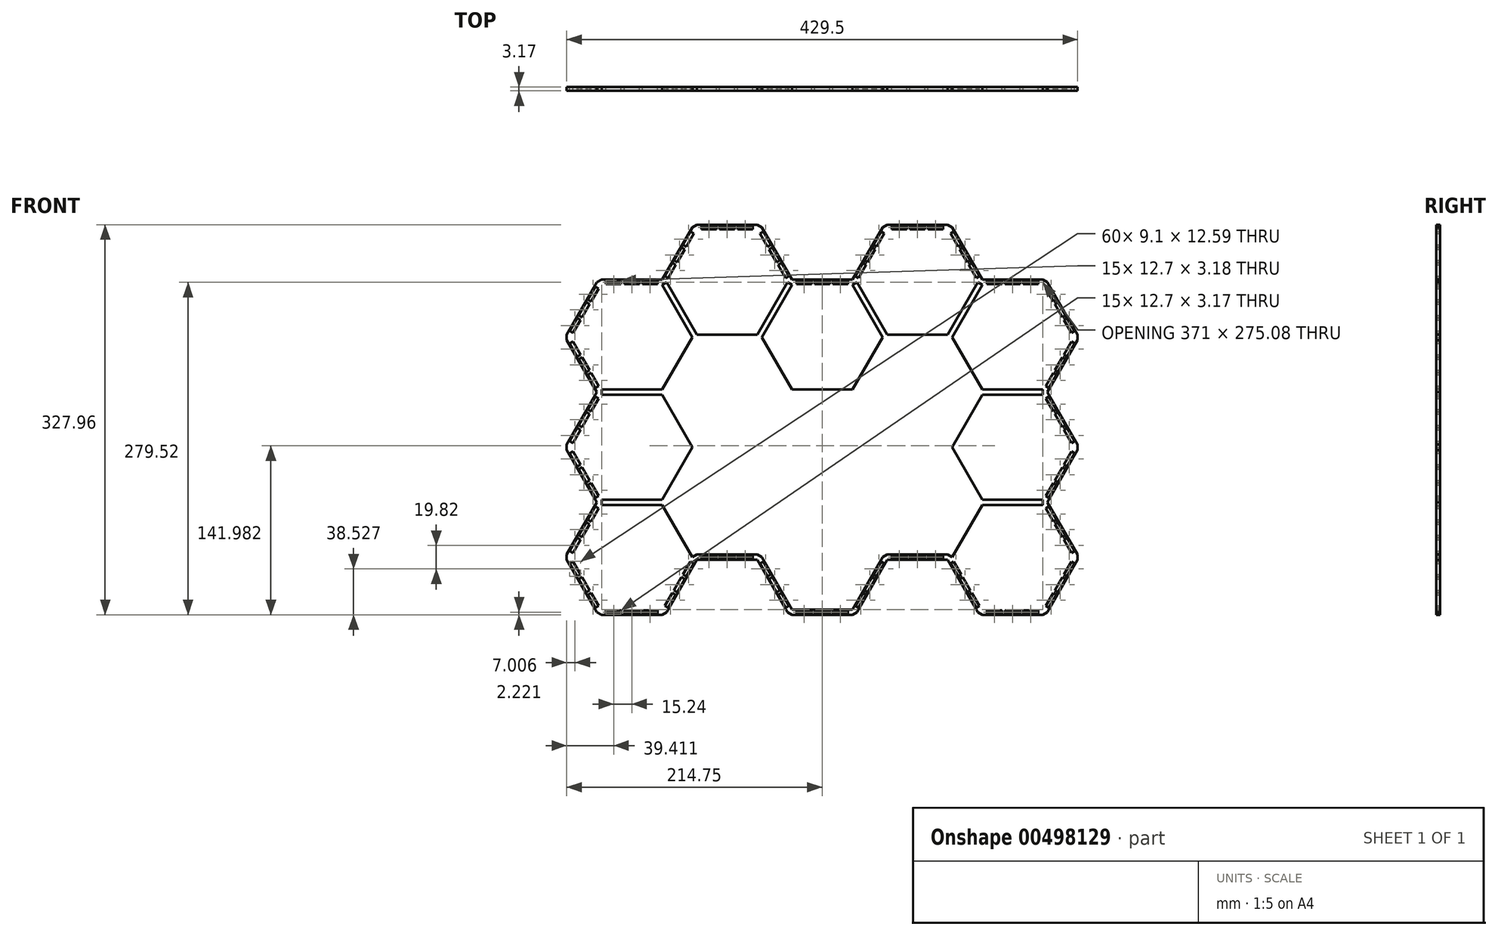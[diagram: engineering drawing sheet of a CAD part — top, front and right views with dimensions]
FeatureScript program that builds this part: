
annotation { "Feature Type Name" : "Feature", "Feature Type Description" : "" }
export const myFeature = defineFeature(function(context is Context, id is Id, definition is map)
    precondition{}
    {
        {
            var Q0;
            Q0=qCreatedBy(makeId("Front.planeOp"),FACE);
            var sketch = newSketch(context, id + "F0", { "sketchPlane" : qUnion([Q0])});
            skLineSegment(sketch, "E0", {"start": v(-1207.39, 88.12) * mm, "end": v(-1156.59, 88.12) * mm});
            skLineSegment(sketch, "E1", {"start": v(-1207.39, 92.57) * mm, "end": v(-1207.39, 88.12) * mm});
            skLineSegment(sketch, "E2", {"start": v(-1156.59, 92.57) * mm, "end": v(-1156.59, 88.12) * mm});
            skLineSegment(sketch, "E3", {"start": v(-1232.79, 44.13) * mm, "end": v(-1131.19, 44.13) * mm, "construction": true});
            skPoint(sketch, "E4.endSnap0", {"position": v(-1156.59, 90.34) * mm});
            skLineSegment(sketch, "E5", {"start": v(-1207.39, 90.34) * mm, "end": v(-1156.59, 90.34) * mm, "construction": true});
            skLineSegment(sketch, "E6", {"start": v(-1207.39, 92.57) * mm, "end": v(-1156.59, 92.57) * mm});
            skLineSegment(sketch, "E7", {"start": v(-1236.64, 46.35) * mm, "end": v(-1232.79, 44.13) * mm});
            skLineSegment(sketch, "E8.left", {"start": v(-1160.4, 88.76) * mm, "end": v(-1160.4, 91.93) * mm});
            skLineSegment(sketch, "E8.right", {"start": v(-1203.58, 88.76) * mm, "end": v(-1203.58, 91.93) * mm});
            skPoint(sketch, "E8.middle", {"position": v(-1181.99, 90.34) * mm});
            skLineSegment(sketch, "E9", {"start": v(-1181.99, 91.93) * mm, "end": v(-1181.99, 88.76) * mm, "construction": true});
            skLineSegment(sketch, "E10", {"start": v(-1190.88, 91.93) * mm, "end": v(-1190.88, 88.76) * mm});
            skLineSegment(sketch, "E11.MirrorCS", {"start": v(-1173.1, 91.93) * mm, "end": v(-1173.1, 88.76) * mm});
            skLineSegment(sketch, "E12", {"start": v(-1188.34, 91.93) * mm, "end": v(-1188.34, 88.76) * mm});
            skLineSegment(sketch, "E13.MirrorCS", {"start": v(-1175.64, 91.93) * mm, "end": v(-1175.64, 88.76) * mm});
            skLineSegment(sketch, "E14", {"start": v(-1203.58, 91.93) * mm, "end": v(-1190.88, 91.93) * mm});
            skLineSegment(sketch, "E15", {"start": v(-1203.58, 88.76) * mm, "end": v(-1190.88, 88.76) * mm});
            skLineSegment(sketch, "E16", {"start": v(-1188.34, 88.76) * mm, "end": v(-1181.99, 88.76) * mm});
            skLineSegment(sketch, "E17", {"start": v(-1188.34, 91.93) * mm, "end": v(-1181.99, 91.93) * mm});
            skLineSegment(sketch, "E18", {"start": v(-1181.99, 91.93) * mm, "end": v(-1175.64, 91.93) * mm});
            skLineSegment(sketch, "E19", {"start": v(-1181.99, 88.76) * mm, "end": v(-1175.64, 88.76) * mm});
            skLineSegment(sketch, "E20", {"start": v(-1173.1, 91.93) * mm, "end": v(-1160.4, 91.93) * mm});
            skLineSegment(sketch, "E21", {"start": v(-1173.1, 88.76) * mm, "end": v(-1160.4, 88.76) * mm});
            skLineSegment(sketch, "E22", {"start": v(-1156.59, 88.12) * mm, "end": v(-1131.19, 44.13) * mm});
            skLineSegment(sketch, "E23", {"start": v(-1152.74, 90.34) * mm, "end": v(-1156.59, 88.12) * mm});
            skPoint(sketch, "E24.endSnap0", {"position": v(-1129.26, 45.24) * mm});
            skLineSegment(sketch, "E25", {"start": v(-1152.74, 90.34) * mm, "end": v(-1127.34, 46.35) * mm});
            skLineSegment(sketch, "E26.left", {"start": v(-1132.54, 47.74) * mm, "end": v(-1129.8, 49.33) * mm});
            skLineSegment(sketch, "E26.right", {"start": v(-1154.13, 85.14) * mm, "end": v(-1151.38, 86.73) * mm});
            skPoint(sketch, "E26.middle", {"position": v(-1141.96, 67.24) * mm});
            skLineSegment(sketch, "E27", {"start": v(-1140.59, 68.03) * mm, "end": v(-1143.34, 66.44) * mm, "construction": true});
            skLineSegment(sketch, "E28", {"start": v(-1145.03, 75.73) * mm, "end": v(-1147.78, 74.14) * mm});
            skLineSegment(sketch, "E29.MirrorCS", {"start": v(-1136.14, 60.33) * mm, "end": v(-1138.9, 58.74) * mm});
            skLineSegment(sketch, "E30", {"start": v(-1143.76, 73.53) * mm, "end": v(-1146.51, 71.94) * mm});
            skLineSegment(sketch, "E31.MirrorCS", {"start": v(-1137.41, 62.53) * mm, "end": v(-1140.16, 60.94) * mm});
            skLineSegment(sketch, "E32", {"start": v(-1151.38, 86.73) * mm, "end": v(-1145.03, 75.73) * mm});
            skLineSegment(sketch, "E33", {"start": v(-1154.13, 85.14) * mm, "end": v(-1147.78, 74.14) * mm});
            skLineSegment(sketch, "E34", {"start": v(-1146.51, 71.94) * mm, "end": v(-1143.34, 66.44) * mm});
            skLineSegment(sketch, "E35", {"start": v(-1143.76, 73.53) * mm, "end": v(-1140.59, 68.03) * mm});
            skLineSegment(sketch, "E36", {"start": v(-1140.59, 68.03) * mm, "end": v(-1137.41, 62.53) * mm});
            skLineSegment(sketch, "E37", {"start": v(-1143.34, 66.44) * mm, "end": v(-1140.16, 60.94) * mm});
            skLineSegment(sketch, "E38", {"start": v(-1136.14, 60.33) * mm, "end": v(-1129.8, 49.33) * mm});
            skLineSegment(sketch, "E39", {"start": v(-1138.9, 58.74) * mm, "end": v(-1132.54, 47.74) * mm});
            skLineSegment(sketch, "E40", {"start": v(-1232.79, 44.13) * mm, "end": v(-1207.39, 88.12) * mm});
            skLineSegment(sketch, "E41", {"start": v(-1211.24, 90.34) * mm, "end": v(-1207.39, 88.12) * mm});
            skPoint(sketch, "E42.endSnap0", {"position": v(-1209.31, 89.23) * mm});
            skLineSegment(sketch, "E43", {"start": v(-1236.64, 46.35) * mm, "end": v(-1211.24, 90.34) * mm});
            skLineSegment(sketch, "E44.left", {"start": v(-1209.84, 85.14) * mm, "end": v(-1212.6, 86.73) * mm});
            skLineSegment(sketch, "E44.right", {"start": v(-1231.43, 47.74) * mm, "end": v(-1234.18, 49.33) * mm});
            skPoint(sketch, "E44.middle", {"position": v(-1222.01, 67.24) * mm});
            skLineSegment(sketch, "E45", {"start": v(-1223.39, 68.03) * mm, "end": v(-1220.64, 66.44) * mm, "construction": true});
            skLineSegment(sketch, "E46", {"start": v(-1227.83, 60.33) * mm, "end": v(-1225.08, 58.74) * mm});
            skLineSegment(sketch, "E47.MirrorCS", {"start": v(-1218.94, 75.73) * mm, "end": v(-1216.2, 74.14) * mm});
            skLineSegment(sketch, "E48", {"start": v(-1226.56, 62.53) * mm, "end": v(-1223.81, 60.94) * mm});
            skLineSegment(sketch, "E49.MirrorCS", {"start": v(-1220.21, 73.53) * mm, "end": v(-1217.46, 71.94) * mm});
            skLineSegment(sketch, "E50", {"start": v(-1234.18, 49.33) * mm, "end": v(-1227.83, 60.33) * mm});
            skLineSegment(sketch, "E51", {"start": v(-1231.43, 47.74) * mm, "end": v(-1225.08, 58.74) * mm});
            skLineSegment(sketch, "E52", {"start": v(-1223.81, 60.94) * mm, "end": v(-1220.64, 66.44) * mm});
            skLineSegment(sketch, "E53", {"start": v(-1226.56, 62.53) * mm, "end": v(-1223.39, 68.03) * mm});
            skLineSegment(sketch, "E54", {"start": v(-1223.39, 68.03) * mm, "end": v(-1220.21, 73.53) * mm});
            skLineSegment(sketch, "E55", {"start": v(-1220.64, 66.44) * mm, "end": v(-1217.46, 71.94) * mm});
            skLineSegment(sketch, "E56", {"start": v(-1218.94, 75.73) * mm, "end": v(-1212.6, 86.73) * mm});
            skLineSegment(sketch, "E57", {"start": v(-1216.2, 74.14) * mm, "end": v(-1209.84, 85.14) * mm});
            skLineSegment(sketch, "E58.0", {"start": v(-1207.39, 88.12) * mm, "end": v(-1211.24, 90.34) * mm, "construction": true});
            skLineSegment(sketch, "E59", {"start": v(-1131.19, 44.13) * mm, "end": v(-1127.34, 46.35) * mm});
            skLineSegment(sketch, "E60.MirrorCS", {"start": v(-1211.24, -2.09) * mm, "end": v(-1207.39, 0.13) * mm});
            skLineSegment(sketch, "E61.MirrorCS", {"start": v(-1140.59, 20.23) * mm, "end": v(-1143.34, 21.81) * mm, "construction": true});
            skLineSegment(sketch, "E62.MirrorCS", {"start": v(-1223.39, 20.23) * mm, "end": v(-1220.64, 21.81) * mm, "construction": true});
            skLineSegment(sketch, "E63.MirrorCS", {"start": v(-1181.99, -3.68) * mm, "end": v(-1181.99, -0.5) * mm, "construction": true});
            skLineSegment(sketch, "E64.MirrorCS", {"start": v(-1207.39, 0.13) * mm, "end": v(-1211.24, -2.09) * mm, "construction": true});
            skLineSegment(sketch, "E65.MirrorCS", {"start": v(-1152.74, -2.09) * mm, "end": v(-1156.59, 0.13) * mm});
            skLineSegment(sketch, "E66.MirrorCS", {"start": v(-1154.13, 3.12) * mm, "end": v(-1151.38, 1.53) * mm});
            skLineSegment(sketch, "E67.MirrorCS", {"start": v(-1220.21, 14.73) * mm, "end": v(-1217.46, 16.31) * mm});
            skLineSegment(sketch, "E68.MirrorCS", {"start": v(-1175.64, -3.68) * mm, "end": v(-1175.64, -0.5) * mm});
            skLineSegment(sketch, "E69.MirrorCS", {"start": v(-1156.59, -4.31) * mm, "end": v(-1156.59, 0.13) * mm});
            skLineSegment(sketch, "E70.MirrorCS", {"start": v(-1190.88, -3.68) * mm, "end": v(-1190.88, -0.5) * mm});
            skLineSegment(sketch, "E71.MirrorCS", {"start": v(-1145.03, 12.53) * mm, "end": v(-1147.78, 14.11) * mm});
            skLineSegment(sketch, "E72.MirrorCS", {"start": v(-1188.34, -3.68) * mm, "end": v(-1188.34, -0.5) * mm});
            skLineSegment(sketch, "E73.MirrorCS", {"start": v(-1209.84, 3.12) * mm, "end": v(-1212.6, 1.53) * mm});
            skLineSegment(sketch, "E74.MirrorCS", {"start": v(-1231.43, 40.51) * mm, "end": v(-1234.18, 38.92) * mm});
            skLineSegment(sketch, "E75.MirrorCS", {"start": v(-1226.56, 25.72) * mm, "end": v(-1223.81, 27.31) * mm});
            skLineSegment(sketch, "E76.MirrorCS", {"start": v(-1236.64, 41.9) * mm, "end": v(-1232.79, 44.13) * mm});
            skLineSegment(sketch, "E77.MirrorCS", {"start": v(-1143.76, 14.73) * mm, "end": v(-1146.51, 16.31) * mm});
            skLineSegment(sketch, "E78.MirrorCS", {"start": v(-1173.1, -3.68) * mm, "end": v(-1173.1, -0.5) * mm});
            skLineSegment(sketch, "E79.MirrorCS", {"start": v(-1227.83, 27.92) * mm, "end": v(-1225.08, 29.51) * mm});
            skLineSegment(sketch, "E80.MirrorCS", {"start": v(-1132.54, 40.51) * mm, "end": v(-1129.8, 38.92) * mm});
            skLineSegment(sketch, "E81.MirrorCS", {"start": v(-1203.58, -0.5) * mm, "end": v(-1203.58, -3.68) * mm});
            skLineSegment(sketch, "E82.MirrorCS", {"start": v(-1136.14, 27.92) * mm, "end": v(-1138.9, 29.51) * mm});
            skLineSegment(sketch, "E83.MirrorCS", {"start": v(-1131.19, 44.13) * mm, "end": v(-1127.34, 41.9) * mm});
            skLineSegment(sketch, "E84.MirrorCS", {"start": v(-1137.41, 25.72) * mm, "end": v(-1140.16, 27.31) * mm});
            skLineSegment(sketch, "E85.MirrorCS", {"start": v(-1218.94, 12.53) * mm, "end": v(-1216.2, 14.11) * mm});
            skLineSegment(sketch, "E86.MirrorCS", {"start": v(-1160.4, -0.5) * mm, "end": v(-1160.4, -3.68) * mm});
            skLineSegment(sketch, "E87.MirrorCS", {"start": v(-1146.51, 16.31) * mm, "end": v(-1143.34, 21.81) * mm});
            skLineSegment(sketch, "E88.MirrorCS", {"start": v(-1188.34, -0.5) * mm, "end": v(-1181.99, -0.5) * mm});
            skLineSegment(sketch, "E89.MirrorCS", {"start": v(-1223.81, 27.31) * mm, "end": v(-1220.64, 21.81) * mm});
            skLineSegment(sketch, "E90.MirrorCS", {"start": v(-1140.59, 20.23) * mm, "end": v(-1137.41, 25.72) * mm});
            skLineSegment(sketch, "E91.MirrorCS", {"start": v(-1207.39, -4.31) * mm, "end": v(-1207.39, 0.13) * mm});
            skLineSegment(sketch, "E92.MirrorCS", {"start": v(-1181.99, -3.68) * mm, "end": v(-1175.64, -3.68) * mm});
            skLineSegment(sketch, "E93.MirrorCS", {"start": v(-1143.34, 21.81) * mm, "end": v(-1140.16, 27.31) * mm});
            skPoint(sketch, "E94.MirrorP", {"position": v(-1181.99, -2.09) * mm});
            skLineSegment(sketch, "E95.MirrorCS", {"start": v(-1181.99, -0.5) * mm, "end": v(-1175.64, -0.5) * mm});
            skLineSegment(sketch, "E96.MirrorCS", {"start": v(-1143.76, 14.73) * mm, "end": v(-1140.59, 20.23) * mm});
            skLineSegment(sketch, "E97.MirrorCS", {"start": v(-1220.64, 21.81) * mm, "end": v(-1217.46, 16.31) * mm});
            skLineSegment(sketch, "E98.MirrorCS", {"start": v(-1188.34, -3.68) * mm, "end": v(-1181.99, -3.68) * mm});
            skLineSegment(sketch, "E99.MirrorCS", {"start": v(-1138.9, 29.51) * mm, "end": v(-1132.54, 40.51) * mm});
            skLineSegment(sketch, "E100.MirrorCS", {"start": v(-1236.64, 41.9) * mm, "end": v(-1211.24, -2.09) * mm});
            skLineSegment(sketch, "E101.MirrorCS", {"start": v(-1173.1, -3.68) * mm, "end": v(-1160.4, -3.68) * mm});
            skLineSegment(sketch, "E102.MirrorCS", {"start": v(-1156.59, 0.13) * mm, "end": v(-1131.19, 44.13) * mm});
            skLineSegment(sketch, "E103.MirrorCS", {"start": v(-1151.38, 1.53) * mm, "end": v(-1145.03, 12.53) * mm});
            skLineSegment(sketch, "E104.MirrorCS", {"start": v(-1231.43, 40.51) * mm, "end": v(-1225.08, 29.51) * mm});
            skLineSegment(sketch, "E105.MirrorCS", {"start": v(-1216.2, 14.11) * mm, "end": v(-1209.84, 3.12) * mm});
            skLineSegment(sketch, "E106.MirrorCS", {"start": v(-1173.1, -0.5) * mm, "end": v(-1160.4, -0.5) * mm});
            skPoint(sketch, "E107.MirrorP", {"position": v(-1141.96, 21.02) * mm});
            skLineSegment(sketch, "E108.MirrorCS", {"start": v(-1136.14, 27.92) * mm, "end": v(-1129.8, 38.92) * mm});
            skLineSegment(sketch, "E109.MirrorCS", {"start": v(-1207.39, 0.13) * mm, "end": v(-1156.59, 0.13) * mm});
            skPoint(sketch, "E110.MirrorP", {"position": v(-1156.59, -2.09) * mm});
            skPoint(sketch, "E111.MirrorP", {"position": v(-1209.31, -0.98) * mm});
            skLineSegment(sketch, "E112.MirrorCS", {"start": v(-1226.56, 25.72) * mm, "end": v(-1223.39, 20.23) * mm});
            skLineSegment(sketch, "E113.MirrorCS", {"start": v(-1207.39, -4.31) * mm, "end": v(-1156.59, -4.31) * mm});
            skLineSegment(sketch, "E114.MirrorCS", {"start": v(-1203.58, -0.5) * mm, "end": v(-1190.88, -0.5) * mm});
            skPoint(sketch, "E115.MirrorP", {"position": v(-1222.01, 21.02) * mm});
            skLineSegment(sketch, "E116.MirrorCS", {"start": v(-1207.39, -2.09) * mm, "end": v(-1156.59, -2.09) * mm, "construction": true});
            skLineSegment(sketch, "E117.MirrorCS", {"start": v(-1154.13, 3.12) * mm, "end": v(-1147.78, 14.11) * mm});
            skLineSegment(sketch, "E118.MirrorCS", {"start": v(-1152.74, -2.09) * mm, "end": v(-1127.34, 41.9) * mm});
            skLineSegment(sketch, "E119.MirrorCS", {"start": v(-1203.58, -3.68) * mm, "end": v(-1190.88, -3.68) * mm});
            skLineSegment(sketch, "E120.MirrorCS", {"start": v(-1232.79, 44.13) * mm, "end": v(-1207.39, 0.13) * mm});
            skLineSegment(sketch, "E121.MirrorCS", {"start": v(-1218.94, 12.53) * mm, "end": v(-1212.6, 1.53) * mm});
            skLineSegment(sketch, "E122.MirrorCS", {"start": v(-1234.18, 38.92) * mm, "end": v(-1227.83, 27.92) * mm});
            skLineSegment(sketch, "E123.MirrorCS", {"start": v(-1223.39, 20.23) * mm, "end": v(-1220.21, 14.73) * mm});
            skPoint(sketch, "E124.MirrorP", {"position": v(-1129.26, 43.02) * mm});
            skLineSegment(sketch, "E125", {"start": v(-1207.39, 180.55) * mm, "end": v(-1156.59, 180.55) * mm});
            skLineSegment(sketch, "E126", {"start": v(-1207.39, 185) * mm, "end": v(-1207.39, 180.55) * mm});
            skLineSegment(sketch, "E127", {"start": v(-1156.59, 185) * mm, "end": v(-1156.59, 180.55) * mm});
            skLineSegment(sketch, "E128", {"start": v(-1232.79, 136.56) * mm, "end": v(-1131.19, 136.56) * mm, "construction": true});
            skPoint(sketch, "E129.endSnap0", {"position": v(-1156.59, 182.78) * mm});
            skLineSegment(sketch, "E130", {"start": v(-1207.39, 182.78) * mm, "end": v(-1156.59, 182.78) * mm, "construction": true});
            skLineSegment(sketch, "E131", {"start": v(-1207.39, 185) * mm, "end": v(-1156.59, 185) * mm});
            skLineSegment(sketch, "E132", {"start": v(-1236.64, 138.78) * mm, "end": v(-1232.79, 136.56) * mm});
            skLineSegment(sketch, "E133.left", {"start": v(-1160.4, 181.19) * mm, "end": v(-1160.4, 184.36) * mm});
            skLineSegment(sketch, "E133.right", {"start": v(-1203.58, 181.19) * mm, "end": v(-1203.58, 184.36) * mm});
            skPoint(sketch, "E133.middle", {"position": v(-1181.99, 182.78) * mm});
            skLineSegment(sketch, "E134", {"start": v(-1181.99, 184.36) * mm, "end": v(-1181.99, 181.19) * mm, "construction": true});
            skLineSegment(sketch, "E135", {"start": v(-1190.88, 184.36) * mm, "end": v(-1190.88, 181.19) * mm});
            skLineSegment(sketch, "E136.MirrorCS", {"start": v(-1173.1, 184.36) * mm, "end": v(-1173.1, 181.19) * mm});
            skLineSegment(sketch, "E137", {"start": v(-1188.34, 184.36) * mm, "end": v(-1188.34, 181.19) * mm});
            skLineSegment(sketch, "E138.MirrorCS", {"start": v(-1175.64, 184.36) * mm, "end": v(-1175.64, 181.19) * mm});
            skLineSegment(sketch, "E139", {"start": v(-1203.58, 184.36) * mm, "end": v(-1190.88, 184.36) * mm});
            skLineSegment(sketch, "E140", {"start": v(-1203.58, 181.19) * mm, "end": v(-1190.88, 181.19) * mm});
            skLineSegment(sketch, "E141", {"start": v(-1188.34, 181.19) * mm, "end": v(-1181.99, 181.19) * mm});
            skLineSegment(sketch, "E142", {"start": v(-1188.34, 184.36) * mm, "end": v(-1181.99, 184.36) * mm});
            skLineSegment(sketch, "E143", {"start": v(-1181.99, 184.36) * mm, "end": v(-1175.64, 184.36) * mm});
            skLineSegment(sketch, "E144", {"start": v(-1181.99, 181.19) * mm, "end": v(-1175.64, 181.19) * mm});
            skLineSegment(sketch, "E145", {"start": v(-1173.1, 184.36) * mm, "end": v(-1160.4, 184.36) * mm});
            skLineSegment(sketch, "E146", {"start": v(-1173.1, 181.19) * mm, "end": v(-1160.4, 181.19) * mm});
            skLineSegment(sketch, "E147", {"start": v(-1156.59, 180.55) * mm, "end": v(-1131.19, 136.56) * mm});
            skLineSegment(sketch, "E148", {"start": v(-1152.74, 182.78) * mm, "end": v(-1156.59, 180.55) * mm});
            skPoint(sketch, "E149.endSnap0", {"position": v(-1129.26, 137.67) * mm});
            skLineSegment(sketch, "E150", {"start": v(-1152.74, 182.78) * mm, "end": v(-1127.34, 138.78) * mm});
            skLineSegment(sketch, "E151.left", {"start": v(-1132.54, 140.18) * mm, "end": v(-1129.8, 141.76) * mm});
            skLineSegment(sketch, "E151.right", {"start": v(-1154.13, 177.57) * mm, "end": v(-1151.38, 179.16) * mm});
            skPoint(sketch, "E151.middle", {"position": v(-1141.96, 159.67) * mm});
            skLineSegment(sketch, "E152", {"start": v(-1140.59, 160.46) * mm, "end": v(-1143.34, 158.87) * mm, "construction": true});
            skLineSegment(sketch, "E153", {"start": v(-1145.03, 168.16) * mm, "end": v(-1147.78, 166.57) * mm});
            skLineSegment(sketch, "E154.MirrorCS", {"start": v(-1136.14, 152.76) * mm, "end": v(-1138.9, 151.18) * mm});
            skLineSegment(sketch, "E155", {"start": v(-1143.76, 165.96) * mm, "end": v(-1146.51, 164.37) * mm});
            skLineSegment(sketch, "E156.MirrorCS", {"start": v(-1137.41, 154.96) * mm, "end": v(-1140.16, 153.38) * mm});
            skLineSegment(sketch, "E157", {"start": v(-1151.38, 179.16) * mm, "end": v(-1145.03, 168.16) * mm});
            skLineSegment(sketch, "E158", {"start": v(-1154.13, 177.57) * mm, "end": v(-1147.78, 166.57) * mm});
            skLineSegment(sketch, "E159", {"start": v(-1146.51, 164.37) * mm, "end": v(-1143.34, 158.87) * mm});
            skLineSegment(sketch, "E160", {"start": v(-1143.76, 165.96) * mm, "end": v(-1140.59, 160.46) * mm});
            skLineSegment(sketch, "E161", {"start": v(-1140.59, 160.46) * mm, "end": v(-1137.41, 154.96) * mm});
            skLineSegment(sketch, "E162", {"start": v(-1143.34, 158.87) * mm, "end": v(-1140.16, 153.38) * mm});
            skLineSegment(sketch, "E163", {"start": v(-1136.14, 152.76) * mm, "end": v(-1129.8, 141.76) * mm});
            skLineSegment(sketch, "E164", {"start": v(-1138.9, 151.18) * mm, "end": v(-1132.54, 140.18) * mm});
            skLineSegment(sketch, "E165", {"start": v(-1232.79, 136.56) * mm, "end": v(-1207.39, 180.55) * mm});
            skLineSegment(sketch, "E166", {"start": v(-1211.24, 182.78) * mm, "end": v(-1207.39, 180.55) * mm});
            skPoint(sketch, "E167.endSnap0", {"position": v(-1209.31, 181.67) * mm});
            skLineSegment(sketch, "E168", {"start": v(-1236.64, 138.78) * mm, "end": v(-1211.24, 182.78) * mm});
            skLineSegment(sketch, "E169.left", {"start": v(-1209.84, 177.57) * mm, "end": v(-1212.6, 179.16) * mm});
            skLineSegment(sketch, "E169.right", {"start": v(-1231.43, 140.18) * mm, "end": v(-1234.18, 141.76) * mm});
            skPoint(sketch, "E169.middle", {"position": v(-1222.01, 159.67) * mm});
            skLineSegment(sketch, "E170", {"start": v(-1223.39, 160.46) * mm, "end": v(-1220.64, 158.87) * mm, "construction": true});
            skLineSegment(sketch, "E171", {"start": v(-1227.83, 152.76) * mm, "end": v(-1225.08, 151.18) * mm});
            skLineSegment(sketch, "E172.MirrorCS", {"start": v(-1218.94, 168.16) * mm, "end": v(-1216.2, 166.57) * mm});
            skLineSegment(sketch, "E173", {"start": v(-1226.56, 154.96) * mm, "end": v(-1223.81, 153.38) * mm});
            skLineSegment(sketch, "E174.MirrorCS", {"start": v(-1220.21, 165.96) * mm, "end": v(-1217.46, 164.37) * mm});
            skLineSegment(sketch, "E175", {"start": v(-1234.18, 141.76) * mm, "end": v(-1227.83, 152.76) * mm});
            skLineSegment(sketch, "E176", {"start": v(-1231.43, 140.18) * mm, "end": v(-1225.08, 151.18) * mm});
            skLineSegment(sketch, "E177", {"start": v(-1223.81, 153.38) * mm, "end": v(-1220.64, 158.87) * mm});
            skLineSegment(sketch, "E178", {"start": v(-1226.56, 154.96) * mm, "end": v(-1223.39, 160.46) * mm});
            skLineSegment(sketch, "E179", {"start": v(-1223.39, 160.46) * mm, "end": v(-1220.21, 165.96) * mm});
            skLineSegment(sketch, "E180", {"start": v(-1220.64, 158.87) * mm, "end": v(-1217.46, 164.37) * mm});
            skLineSegment(sketch, "E181", {"start": v(-1218.94, 168.16) * mm, "end": v(-1212.6, 179.16) * mm});
            skLineSegment(sketch, "E182", {"start": v(-1216.2, 166.57) * mm, "end": v(-1209.84, 177.57) * mm});
            skLineSegment(sketch, "E183.0", {"start": v(-1207.39, 180.55) * mm, "end": v(-1211.24, 182.78) * mm, "construction": true});
            skLineSegment(sketch, "E184", {"start": v(-1131.19, 136.56) * mm, "end": v(-1127.34, 138.78) * mm});
            skLineSegment(sketch, "E185.MirrorCS", {"start": v(-1211.24, 90.34) * mm, "end": v(-1207.39, 92.57) * mm});
            skLineSegment(sketch, "E186.MirrorCS", {"start": v(-1140.59, 112.66) * mm, "end": v(-1143.34, 114.25) * mm, "construction": true});
            skLineSegment(sketch, "E187.MirrorCS", {"start": v(-1223.39, 112.66) * mm, "end": v(-1220.64, 114.25) * mm, "construction": true});
            skLineSegment(sketch, "E188.MirrorCS", {"start": v(-1181.99, 88.76) * mm, "end": v(-1181.99, 91.93) * mm, "construction": true});
            skLineSegment(sketch, "E189.MirrorCS", {"start": v(-1207.39, 92.57) * mm, "end": v(-1211.24, 90.34) * mm, "construction": true});
            skLineSegment(sketch, "E190.MirrorCS", {"start": v(-1152.74, 90.34) * mm, "end": v(-1156.59, 92.57) * mm});
            skLineSegment(sketch, "E191.MirrorCS", {"start": v(-1154.13, 95.55) * mm, "end": v(-1151.38, 93.96) * mm});
            skLineSegment(sketch, "E192.MirrorCS", {"start": v(-1220.21, 107.16) * mm, "end": v(-1217.46, 108.75) * mm});
            skLineSegment(sketch, "E193.MirrorCS", {"start": v(-1175.64, 88.76) * mm, "end": v(-1175.64, 91.93) * mm});
            skLineSegment(sketch, "E194.MirrorCS", {"start": v(-1156.59, 88.12) * mm, "end": v(-1156.59, 92.57) * mm});
            skLineSegment(sketch, "E195.MirrorCS", {"start": v(-1190.88, 88.76) * mm, "end": v(-1190.88, 91.93) * mm});
            skLineSegment(sketch, "E196.MirrorCS", {"start": v(-1145.03, 104.96) * mm, "end": v(-1147.78, 106.55) * mm});
            skLineSegment(sketch, "E197.MirrorCS", {"start": v(-1188.34, 88.76) * mm, "end": v(-1188.34, 91.93) * mm});
            skLineSegment(sketch, "E198.MirrorCS", {"start": v(-1209.84, 95.55) * mm, "end": v(-1212.6, 93.96) * mm});
            skLineSegment(sketch, "E199.MirrorCS", {"start": v(-1231.43, 132.94) * mm, "end": v(-1234.18, 131.36) * mm});
            skLineSegment(sketch, "E200.MirrorCS", {"start": v(-1226.56, 118.16) * mm, "end": v(-1223.81, 119.75) * mm});
            skLineSegment(sketch, "E201.MirrorCS", {"start": v(-1236.64, 134.34) * mm, "end": v(-1232.79, 136.56) * mm});
            skLineSegment(sketch, "E202.MirrorCS", {"start": v(-1143.76, 107.16) * mm, "end": v(-1146.51, 108.75) * mm});
            skLineSegment(sketch, "E203.MirrorCS", {"start": v(-1173.1, 88.76) * mm, "end": v(-1173.1, 91.93) * mm});
            skLineSegment(sketch, "E204.MirrorCS", {"start": v(-1227.83, 120.36) * mm, "end": v(-1225.08, 121.94) * mm});
            skLineSegment(sketch, "E205.MirrorCS", {"start": v(-1132.54, 132.94) * mm, "end": v(-1129.8, 131.36) * mm});
            skLineSegment(sketch, "E206.MirrorCS", {"start": v(-1203.58, 91.93) * mm, "end": v(-1203.58, 88.76) * mm});
            skLineSegment(sketch, "E207.MirrorCS", {"start": v(-1136.14, 120.36) * mm, "end": v(-1138.9, 121.94) * mm});
            skLineSegment(sketch, "E208.MirrorCS", {"start": v(-1131.19, 136.56) * mm, "end": v(-1127.34, 134.34) * mm});
            skLineSegment(sketch, "E209.MirrorCS", {"start": v(-1137.41, 118.16) * mm, "end": v(-1140.16, 119.75) * mm});
            skLineSegment(sketch, "E210.MirrorCS", {"start": v(-1218.94, 104.96) * mm, "end": v(-1216.2, 106.55) * mm});
            skLineSegment(sketch, "E211.MirrorCS", {"start": v(-1160.4, 91.93) * mm, "end": v(-1160.4, 88.76) * mm});
            skLineSegment(sketch, "E212.MirrorCS", {"start": v(-1146.51, 108.75) * mm, "end": v(-1143.34, 114.25) * mm});
            skLineSegment(sketch, "E213.MirrorCS", {"start": v(-1223.81, 119.75) * mm, "end": v(-1220.64, 114.25) * mm});
            skLineSegment(sketch, "E214.MirrorCS", {"start": v(-1140.59, 112.66) * mm, "end": v(-1137.41, 118.16) * mm});
            skLineSegment(sketch, "E215.MirrorCS", {"start": v(-1207.39, 88.12) * mm, "end": v(-1207.39, 92.57) * mm});
            skLineSegment(sketch, "E216.MirrorCS", {"start": v(-1143.34, 114.25) * mm, "end": v(-1140.16, 119.75) * mm});
            skLineSegment(sketch, "E217.MirrorCS", {"start": v(-1143.76, 107.16) * mm, "end": v(-1140.59, 112.66) * mm});
            skLineSegment(sketch, "E218.MirrorCS", {"start": v(-1220.64, 114.25) * mm, "end": v(-1217.46, 108.75) * mm});
            skLineSegment(sketch, "E219.MirrorCS", {"start": v(-1138.9, 121.94) * mm, "end": v(-1132.54, 132.94) * mm});
            skLineSegment(sketch, "E220.MirrorCS", {"start": v(-1236.64, 134.34) * mm, "end": v(-1211.24, 90.34) * mm});
            skLineSegment(sketch, "E221.MirrorCS", {"start": v(-1156.59, 92.57) * mm, "end": v(-1131.19, 136.56) * mm});
            skLineSegment(sketch, "E222.MirrorCS", {"start": v(-1151.38, 93.96) * mm, "end": v(-1145.03, 104.96) * mm});
            skLineSegment(sketch, "E223.MirrorCS", {"start": v(-1231.43, 132.94) * mm, "end": v(-1225.08, 121.94) * mm});
            skLineSegment(sketch, "E224.MirrorCS", {"start": v(-1216.2, 106.55) * mm, "end": v(-1209.84, 95.55) * mm});
            skPoint(sketch, "E225.MirrorP", {"position": v(-1141.96, 113.45) * mm});
            skLineSegment(sketch, "E226.MirrorCS", {"start": v(-1136.14, 120.36) * mm, "end": v(-1129.8, 131.36) * mm});
            skPoint(sketch, "E227.MirrorP", {"position": v(-1209.31, 91.45) * mm});
            skLineSegment(sketch, "E228.MirrorCS", {"start": v(-1226.56, 118.16) * mm, "end": v(-1223.39, 112.66) * mm});
            skPoint(sketch, "E229.MirrorP", {"position": v(-1222.01, 113.45) * mm});
            skLineSegment(sketch, "E230.MirrorCS", {"start": v(-1154.13, 95.55) * mm, "end": v(-1147.78, 106.55) * mm});
            skLineSegment(sketch, "E231.MirrorCS", {"start": v(-1152.74, 90.34) * mm, "end": v(-1127.34, 134.34) * mm});
            skLineSegment(sketch, "E232.MirrorCS", {"start": v(-1232.79, 136.56) * mm, "end": v(-1207.39, 92.57) * mm});
            skLineSegment(sketch, "E233.MirrorCS", {"start": v(-1218.94, 104.96) * mm, "end": v(-1212.6, 93.96) * mm});
            skLineSegment(sketch, "E234.MirrorCS", {"start": v(-1234.18, 131.36) * mm, "end": v(-1227.83, 120.36) * mm});
            skLineSegment(sketch, "E235.MirrorCS", {"start": v(-1223.39, 112.66) * mm, "end": v(-1220.21, 107.16) * mm});
            skPoint(sketch, "E236.MirrorP", {"position": v(-1129.26, 135.45) * mm});
            skLineSegment(sketch, "E237", {"start": v(-1207.39, 272.99) * mm, "end": v(-1156.59, 272.99) * mm});
            skLineSegment(sketch, "E238", {"start": v(-1207.39, 277.43) * mm, "end": v(-1207.39, 272.99) * mm});
            skLineSegment(sketch, "E239", {"start": v(-1156.59, 277.43) * mm, "end": v(-1156.59, 272.99) * mm});
            skLineSegment(sketch, "E240", {"start": v(-1232.79, 229) * mm, "end": v(-1131.19, 229) * mm, "construction": true});
            skPoint(sketch, "E241.endSnap0", {"position": v(-1156.59, 275.21) * mm});
            skLineSegment(sketch, "E242", {"start": v(-1207.39, 275.21) * mm, "end": v(-1156.59, 275.21) * mm, "construction": true});
            skLineSegment(sketch, "E243", {"start": v(-1207.39, 277.43) * mm, "end": v(-1156.59, 277.43) * mm});
            skLineSegment(sketch, "E244", {"start": v(-1236.64, 231.22) * mm, "end": v(-1232.79, 229) * mm});
            skLineSegment(sketch, "E245.left", {"start": v(-1160.4, 273.62) * mm, "end": v(-1160.4, 276.8) * mm});
            skLineSegment(sketch, "E245.right", {"start": v(-1203.58, 273.62) * mm, "end": v(-1203.58, 276.8) * mm});
            skPoint(sketch, "E245.middle", {"position": v(-1181.99, 275.21) * mm});
            skLineSegment(sketch, "E246", {"start": v(-1181.99, 276.8) * mm, "end": v(-1181.99, 273.62) * mm, "construction": true});
            skLineSegment(sketch, "E247", {"start": v(-1190.88, 276.8) * mm, "end": v(-1190.88, 273.62) * mm});
            skLineSegment(sketch, "E248.MirrorCS", {"start": v(-1173.1, 276.8) * mm, "end": v(-1173.1, 273.62) * mm});
            skLineSegment(sketch, "E249", {"start": v(-1188.34, 276.8) * mm, "end": v(-1188.34, 273.62) * mm});
            skLineSegment(sketch, "E250.MirrorCS", {"start": v(-1175.64, 276.8) * mm, "end": v(-1175.64, 273.62) * mm});
            skLineSegment(sketch, "E251", {"start": v(-1203.58, 276.8) * mm, "end": v(-1190.88, 276.8) * mm});
            skLineSegment(sketch, "E252", {"start": v(-1203.58, 273.62) * mm, "end": v(-1190.88, 273.62) * mm});
            skLineSegment(sketch, "E253", {"start": v(-1188.34, 273.62) * mm, "end": v(-1181.99, 273.62) * mm});
            skLineSegment(sketch, "E254", {"start": v(-1188.34, 276.8) * mm, "end": v(-1181.99, 276.8) * mm});
            skLineSegment(sketch, "E255", {"start": v(-1181.99, 276.8) * mm, "end": v(-1175.64, 276.8) * mm});
            skLineSegment(sketch, "E256", {"start": v(-1181.99, 273.62) * mm, "end": v(-1175.64, 273.62) * mm});
            skLineSegment(sketch, "E257", {"start": v(-1173.1, 276.8) * mm, "end": v(-1160.4, 276.8) * mm});
            skLineSegment(sketch, "E258", {"start": v(-1173.1, 273.62) * mm, "end": v(-1160.4, 273.62) * mm});
            skLineSegment(sketch, "E259", {"start": v(-1156.59, 272.99) * mm, "end": v(-1131.19, 229) * mm});
            skLineSegment(sketch, "E260", {"start": v(-1152.74, 275.21) * mm, "end": v(-1156.59, 272.99) * mm});
            skPoint(sketch, "E261.endSnap0", {"position": v(-1129.26, 230.1) * mm});
            skLineSegment(sketch, "E262", {"start": v(-1152.74, 275.21) * mm, "end": v(-1127.34, 231.22) * mm});
            skLineSegment(sketch, "E263.left", {"start": v(-1132.54, 232.61) * mm, "end": v(-1129.8, 234.2) * mm});
            skLineSegment(sketch, "E263.right", {"start": v(-1154.13, 270) * mm, "end": v(-1151.38, 271.6) * mm});
            skPoint(sketch, "E263.middle", {"position": v(-1141.96, 252.1) * mm});
            skLineSegment(sketch, "E264", {"start": v(-1140.59, 252.9) * mm, "end": v(-1143.34, 251.3) * mm, "construction": true});
            skLineSegment(sketch, "E265", {"start": v(-1145.03, 260.6) * mm, "end": v(-1147.78, 259) * mm});
            skLineSegment(sketch, "E266.MirrorCS", {"start": v(-1136.14, 245.2) * mm, "end": v(-1138.9, 243.6) * mm});
            skLineSegment(sketch, "E267", {"start": v(-1143.76, 258.4) * mm, "end": v(-1146.51, 256.8) * mm});
            skLineSegment(sketch, "E268.MirrorCS", {"start": v(-1137.41, 247.4) * mm, "end": v(-1140.16, 245.8) * mm});
            skLineSegment(sketch, "E269", {"start": v(-1151.38, 271.6) * mm, "end": v(-1145.03, 260.6) * mm});
            skLineSegment(sketch, "E270", {"start": v(-1154.13, 270) * mm, "end": v(-1147.78, 259) * mm});
            skLineSegment(sketch, "E271", {"start": v(-1146.51, 256.8) * mm, "end": v(-1143.34, 251.3) * mm});
            skLineSegment(sketch, "E272", {"start": v(-1143.76, 258.4) * mm, "end": v(-1140.59, 252.9) * mm});
            skLineSegment(sketch, "E273", {"start": v(-1140.59, 252.9) * mm, "end": v(-1137.41, 247.4) * mm});
            skLineSegment(sketch, "E274", {"start": v(-1143.34, 251.3) * mm, "end": v(-1140.16, 245.8) * mm});
            skLineSegment(sketch, "E275", {"start": v(-1136.14, 245.2) * mm, "end": v(-1129.8, 234.2) * mm});
            skLineSegment(sketch, "E276", {"start": v(-1138.9, 243.6) * mm, "end": v(-1132.54, 232.61) * mm});
            skLineSegment(sketch, "E277", {"start": v(-1232.79, 229) * mm, "end": v(-1207.39, 272.99) * mm});
            skLineSegment(sketch, "E278", {"start": v(-1211.24, 275.21) * mm, "end": v(-1207.39, 272.99) * mm});
            skPoint(sketch, "E279.endSnap0", {"position": v(-1209.31, 274.1) * mm});
            skLineSegment(sketch, "E280", {"start": v(-1236.64, 231.22) * mm, "end": v(-1211.24, 275.21) * mm});
            skLineSegment(sketch, "E281.left", {"start": v(-1209.84, 270) * mm, "end": v(-1212.6, 271.6) * mm});
            skLineSegment(sketch, "E281.right", {"start": v(-1231.43, 232.61) * mm, "end": v(-1234.18, 234.2) * mm});
            skPoint(sketch, "E281.middle", {"position": v(-1222.01, 252.1) * mm});
            skLineSegment(sketch, "E282", {"start": v(-1223.39, 252.9) * mm, "end": v(-1220.64, 251.3) * mm, "construction": true});
            skLineSegment(sketch, "E283", {"start": v(-1227.83, 245.2) * mm, "end": v(-1225.08, 243.6) * mm});
            skLineSegment(sketch, "E284.MirrorCS", {"start": v(-1218.94, 260.6) * mm, "end": v(-1216.2, 259) * mm});
            skLineSegment(sketch, "E285", {"start": v(-1226.56, 247.4) * mm, "end": v(-1223.81, 245.8) * mm});
            skLineSegment(sketch, "E286.MirrorCS", {"start": v(-1220.21, 258.4) * mm, "end": v(-1217.46, 256.8) * mm});
            skLineSegment(sketch, "E287", {"start": v(-1234.18, 234.2) * mm, "end": v(-1227.83, 245.2) * mm});
            skLineSegment(sketch, "E288", {"start": v(-1231.43, 232.61) * mm, "end": v(-1225.08, 243.6) * mm});
            skLineSegment(sketch, "E289", {"start": v(-1223.81, 245.8) * mm, "end": v(-1220.64, 251.3) * mm});
            skLineSegment(sketch, "E290", {"start": v(-1226.56, 247.4) * mm, "end": v(-1223.39, 252.9) * mm});
            skLineSegment(sketch, "E291", {"start": v(-1223.39, 252.9) * mm, "end": v(-1220.21, 258.4) * mm});
            skLineSegment(sketch, "E292", {"start": v(-1220.64, 251.3) * mm, "end": v(-1217.46, 256.8) * mm});
            skLineSegment(sketch, "E293", {"start": v(-1218.94, 260.6) * mm, "end": v(-1212.6, 271.6) * mm});
            skLineSegment(sketch, "E294", {"start": v(-1216.2, 259) * mm, "end": v(-1209.84, 270) * mm});
            skLineSegment(sketch, "E295.0", {"start": v(-1207.39, 272.99) * mm, "end": v(-1211.24, 275.21) * mm, "construction": true});
            skLineSegment(sketch, "E296", {"start": v(-1131.19, 229) * mm, "end": v(-1127.34, 231.22) * mm});
            skLineSegment(sketch, "E297.MirrorCS", {"start": v(-1211.24, 182.78) * mm, "end": v(-1207.39, 185) * mm});
            skLineSegment(sketch, "E298.MirrorCS", {"start": v(-1140.59, 205.1) * mm, "end": v(-1143.34, 206.68) * mm, "construction": true});
            skLineSegment(sketch, "E299.MirrorCS", {"start": v(-1223.39, 205.1) * mm, "end": v(-1220.64, 206.68) * mm, "construction": true});
            skLineSegment(sketch, "E300.MirrorCS", {"start": v(-1181.99, 181.19) * mm, "end": v(-1181.99, 184.36) * mm, "construction": true});
            skLineSegment(sketch, "E301.MirrorCS", {"start": v(-1207.39, 185) * mm, "end": v(-1211.24, 182.78) * mm, "construction": true});
            skLineSegment(sketch, "E302.MirrorCS", {"start": v(-1152.74, 182.78) * mm, "end": v(-1156.59, 185) * mm});
            skLineSegment(sketch, "E303.MirrorCS", {"start": v(-1154.13, 187.98) * mm, "end": v(-1151.38, 186.4) * mm});
            skLineSegment(sketch, "E304.MirrorCS", {"start": v(-1220.21, 199.6) * mm, "end": v(-1217.46, 201.18) * mm});
            skLineSegment(sketch, "E305.MirrorCS", {"start": v(-1175.64, 181.19) * mm, "end": v(-1175.64, 184.36) * mm});
            skLineSegment(sketch, "E306.MirrorCS", {"start": v(-1156.59, 180.55) * mm, "end": v(-1156.59, 185) * mm});
            skLineSegment(sketch, "E307.MirrorCS", {"start": v(-1190.88, 181.19) * mm, "end": v(-1190.88, 184.36) * mm});
            skLineSegment(sketch, "E308.MirrorCS", {"start": v(-1145.03, 197.4) * mm, "end": v(-1147.78, 198.98) * mm});
            skLineSegment(sketch, "E309.MirrorCS", {"start": v(-1188.34, 181.19) * mm, "end": v(-1188.34, 184.36) * mm});
            skLineSegment(sketch, "E310.MirrorCS", {"start": v(-1209.84, 187.98) * mm, "end": v(-1212.6, 186.4) * mm});
            skLineSegment(sketch, "E311.MirrorCS", {"start": v(-1231.43, 225.38) * mm, "end": v(-1234.18, 223.79) * mm});
            skLineSegment(sketch, "E312.MirrorCS", {"start": v(-1226.56, 210.6) * mm, "end": v(-1223.81, 212.18) * mm});
            skLineSegment(sketch, "E313.MirrorCS", {"start": v(-1236.64, 226.77) * mm, "end": v(-1232.79, 229) * mm});
            skLineSegment(sketch, "E314.MirrorCS", {"start": v(-1143.76, 199.6) * mm, "end": v(-1146.51, 201.18) * mm});
            skLineSegment(sketch, "E315.MirrorCS", {"start": v(-1173.1, 181.19) * mm, "end": v(-1173.1, 184.36) * mm});
            skLineSegment(sketch, "E316.MirrorCS", {"start": v(-1227.83, 212.8) * mm, "end": v(-1225.08, 214.38) * mm});
            skLineSegment(sketch, "E317.MirrorCS", {"start": v(-1132.54, 225.38) * mm, "end": v(-1129.8, 223.79) * mm});
            skLineSegment(sketch, "E318.MirrorCS", {"start": v(-1203.58, 184.36) * mm, "end": v(-1203.58, 181.19) * mm});
            skLineSegment(sketch, "E319.MirrorCS", {"start": v(-1136.14, 212.8) * mm, "end": v(-1138.9, 214.38) * mm});
            skLineSegment(sketch, "E320.MirrorCS", {"start": v(-1131.19, 229) * mm, "end": v(-1127.34, 226.77) * mm});
            skLineSegment(sketch, "E321.MirrorCS", {"start": v(-1137.41, 210.6) * mm, "end": v(-1140.16, 212.18) * mm});
            skLineSegment(sketch, "E322.MirrorCS", {"start": v(-1218.94, 197.4) * mm, "end": v(-1216.2, 198.98) * mm});
            skLineSegment(sketch, "E323.MirrorCS", {"start": v(-1160.4, 184.36) * mm, "end": v(-1160.4, 181.19) * mm});
            skLineSegment(sketch, "E324.MirrorCS", {"start": v(-1146.51, 201.18) * mm, "end": v(-1143.34, 206.68) * mm});
            skLineSegment(sketch, "E325.MirrorCS", {"start": v(-1223.81, 212.18) * mm, "end": v(-1220.64, 206.68) * mm});
            skLineSegment(sketch, "E326.MirrorCS", {"start": v(-1140.59, 205.1) * mm, "end": v(-1137.41, 210.6) * mm});
            skLineSegment(sketch, "E327.MirrorCS", {"start": v(-1207.39, 180.55) * mm, "end": v(-1207.39, 185) * mm});
            skLineSegment(sketch, "E328.MirrorCS", {"start": v(-1143.34, 206.68) * mm, "end": v(-1140.16, 212.18) * mm});
            skLineSegment(sketch, "E329.MirrorCS", {"start": v(-1143.76, 199.6) * mm, "end": v(-1140.59, 205.1) * mm});
            skLineSegment(sketch, "E330.MirrorCS", {"start": v(-1220.64, 206.68) * mm, "end": v(-1217.46, 201.18) * mm});
            skLineSegment(sketch, "E331.MirrorCS", {"start": v(-1138.9, 214.38) * mm, "end": v(-1132.54, 225.38) * mm});
            skLineSegment(sketch, "E332.MirrorCS", {"start": v(-1236.64, 226.77) * mm, "end": v(-1211.24, 182.78) * mm});
            skLineSegment(sketch, "E333.MirrorCS", {"start": v(-1156.59, 185) * mm, "end": v(-1131.19, 229) * mm});
            skLineSegment(sketch, "E334.MirrorCS", {"start": v(-1151.38, 186.4) * mm, "end": v(-1145.03, 197.4) * mm});
            skLineSegment(sketch, "E335.MirrorCS", {"start": v(-1231.43, 225.38) * mm, "end": v(-1225.08, 214.38) * mm});
            skLineSegment(sketch, "E336.MirrorCS", {"start": v(-1216.2, 198.98) * mm, "end": v(-1209.84, 187.98) * mm});
            skPoint(sketch, "E337.MirrorP", {"position": v(-1141.96, 205.89) * mm});
            skLineSegment(sketch, "E338.MirrorCS", {"start": v(-1136.14, 212.8) * mm, "end": v(-1129.8, 223.79) * mm});
            skPoint(sketch, "E339.MirrorP", {"position": v(-1209.31, 183.89) * mm});
            skLineSegment(sketch, "E340.MirrorCS", {"start": v(-1226.56, 210.6) * mm, "end": v(-1223.39, 205.1) * mm});
            skPoint(sketch, "E341.MirrorP", {"position": v(-1222.01, 205.89) * mm});
            skLineSegment(sketch, "E342.MirrorCS", {"start": v(-1154.13, 187.98) * mm, "end": v(-1147.78, 198.98) * mm});
            skLineSegment(sketch, "E343.MirrorCS", {"start": v(-1152.74, 182.78) * mm, "end": v(-1127.34, 226.77) * mm});
            skLineSegment(sketch, "E344.MirrorCS", {"start": v(-1232.79, 229) * mm, "end": v(-1207.39, 185) * mm});
            skLineSegment(sketch, "E345.MirrorCS", {"start": v(-1218.94, 197.4) * mm, "end": v(-1212.6, 186.4) * mm});
            skLineSegment(sketch, "E346.MirrorCS", {"start": v(-1234.18, 223.79) * mm, "end": v(-1227.83, 212.8) * mm});
            skLineSegment(sketch, "E347.MirrorCS", {"start": v(-1223.39, 205.1) * mm, "end": v(-1220.21, 199.6) * mm});
            skPoint(sketch, "E348.MirrorP", {"position": v(-1129.26, 227.88) * mm});
            skLineSegment(sketch, "E349", {"start": v(-1127.34, 134.34) * mm, "end": v(-1076.54, 134.34) * mm});
            skLineSegment(sketch, "E350", {"start": v(-1127.34, 138.78) * mm, "end": v(-1127.34, 134.34) * mm});
            skLineSegment(sketch, "E351", {"start": v(-1076.54, 138.78) * mm, "end": v(-1076.54, 134.34) * mm});
            skLineSegment(sketch, "E352", {"start": v(-1152.74, 90.34) * mm, "end": v(-1051.14, 90.34) * mm, "construction": true});
            skPoint(sketch, "E353.endSnap0", {"position": v(-1076.54, 136.56) * mm});
            skLineSegment(sketch, "E354", {"start": v(-1127.34, 136.56) * mm, "end": v(-1076.54, 136.56) * mm, "construction": true});
            skLineSegment(sketch, "E355", {"start": v(-1127.34, 138.78) * mm, "end": v(-1076.54, 138.78) * mm});
            skLineSegment(sketch, "E356", {"start": v(-1156.59, 92.57) * mm, "end": v(-1152.74, 90.34) * mm});
            skLineSegment(sketch, "E357.left", {"start": v(-1080.35, 134.97) * mm, "end": v(-1080.35, 138.15) * mm});
            skLineSegment(sketch, "E357.right", {"start": v(-1123.53, 134.97) * mm, "end": v(-1123.53, 138.15) * mm});
            skPoint(sketch, "E357.middle", {"position": v(-1101.94, 136.56) * mm});
            skLineSegment(sketch, "E358", {"start": v(-1101.94, 138.15) * mm, "end": v(-1101.94, 134.97) * mm, "construction": true});
            skLineSegment(sketch, "E359", {"start": v(-1110.83, 138.15) * mm, "end": v(-1110.83, 134.97) * mm});
            skLineSegment(sketch, "E360.MirrorCS", {"start": v(-1093.05, 138.15) * mm, "end": v(-1093.05, 134.97) * mm});
            skLineSegment(sketch, "E361", {"start": v(-1108.29, 138.15) * mm, "end": v(-1108.29, 134.97) * mm});
            skLineSegment(sketch, "E362.MirrorCS", {"start": v(-1095.59, 138.15) * mm, "end": v(-1095.59, 134.97) * mm});
            skLineSegment(sketch, "E363", {"start": v(-1123.53, 138.15) * mm, "end": v(-1110.83, 138.15) * mm});
            skLineSegment(sketch, "E364", {"start": v(-1123.53, 134.97) * mm, "end": v(-1110.83, 134.97) * mm});
            skLineSegment(sketch, "E365", {"start": v(-1108.29, 134.97) * mm, "end": v(-1101.94, 134.97) * mm});
            skLineSegment(sketch, "E366", {"start": v(-1108.29, 138.15) * mm, "end": v(-1101.94, 138.15) * mm});
            skLineSegment(sketch, "E367", {"start": v(-1101.94, 138.15) * mm, "end": v(-1095.59, 138.15) * mm});
            skLineSegment(sketch, "E368", {"start": v(-1101.94, 134.97) * mm, "end": v(-1095.59, 134.97) * mm});
            skLineSegment(sketch, "E369", {"start": v(-1093.05, 138.15) * mm, "end": v(-1080.35, 138.15) * mm});
            skLineSegment(sketch, "E370", {"start": v(-1093.05, 134.97) * mm, "end": v(-1080.35, 134.97) * mm});
            skLineSegment(sketch, "E371", {"start": v(-1076.54, 134.34) * mm, "end": v(-1051.14, 90.34) * mm});
            skLineSegment(sketch, "E372", {"start": v(-1072.69, 136.56) * mm, "end": v(-1076.54, 134.34) * mm});
            skPoint(sketch, "E373.endSnap0", {"position": v(-1049.21, 91.45) * mm});
            skLineSegment(sketch, "E374", {"start": v(-1072.69, 136.56) * mm, "end": v(-1047.29, 92.57) * mm});
            skLineSegment(sketch, "E375.left", {"start": v(-1052.5, 93.96) * mm, "end": v(-1049.74, 95.55) * mm});
            skLineSegment(sketch, "E375.right", {"start": v(-1074.08, 131.36) * mm, "end": v(-1071.33, 132.94) * mm});
            skPoint(sketch, "E375.middle", {"position": v(-1061.91, 113.45) * mm});
            skLineSegment(sketch, "E376", {"start": v(-1060.54, 114.25) * mm, "end": v(-1063.29, 112.66) * mm, "construction": true});
            skLineSegment(sketch, "E377", {"start": v(-1064.98, 121.94) * mm, "end": v(-1067.73, 120.36) * mm});
            skLineSegment(sketch, "E378.MirrorCS", {"start": v(-1056.1, 106.55) * mm, "end": v(-1058.84, 104.96) * mm});
            skLineSegment(sketch, "E379", {"start": v(-1063.71, 119.75) * mm, "end": v(-1066.46, 118.16) * mm});
            skLineSegment(sketch, "E380.MirrorCS", {"start": v(-1057.36, 108.75) * mm, "end": v(-1060.11, 107.16) * mm});
            skLineSegment(sketch, "E381", {"start": v(-1071.33, 132.94) * mm, "end": v(-1064.98, 121.94) * mm});
            skLineSegment(sketch, "E382", {"start": v(-1074.08, 131.36) * mm, "end": v(-1067.73, 120.36) * mm});
            skLineSegment(sketch, "E383", {"start": v(-1066.46, 118.16) * mm, "end": v(-1063.29, 112.66) * mm});
            skLineSegment(sketch, "E384", {"start": v(-1063.71, 119.75) * mm, "end": v(-1060.54, 114.25) * mm});
            skLineSegment(sketch, "E385", {"start": v(-1060.54, 114.25) * mm, "end": v(-1057.36, 108.75) * mm});
            skLineSegment(sketch, "E386", {"start": v(-1063.29, 112.66) * mm, "end": v(-1060.11, 107.16) * mm});
            skLineSegment(sketch, "E387", {"start": v(-1056.1, 106.55) * mm, "end": v(-1049.74, 95.55) * mm});
            skLineSegment(sketch, "E388", {"start": v(-1058.84, 104.96) * mm, "end": v(-1052.5, 93.96) * mm});
            skLineSegment(sketch, "E389.left", {"start": v(-1129.8, 131.36) * mm, "end": v(-1132.54, 132.94) * mm});
            skLineSegment(sketch, "E389.right", {"start": v(-1151.38, 93.96) * mm, "end": v(-1154.13, 95.55) * mm});
            skLineSegment(sketch, "E390", {"start": v(-1143.34, 114.25) * mm, "end": v(-1140.59, 112.66) * mm, "construction": true});
            skLineSegment(sketch, "E391", {"start": v(-1147.78, 106.55) * mm, "end": v(-1145.03, 104.96) * mm});
            skLineSegment(sketch, "E392.MirrorCS", {"start": v(-1138.9, 121.94) * mm, "end": v(-1136.14, 120.36) * mm});
            skLineSegment(sketch, "E393", {"start": v(-1146.51, 108.75) * mm, "end": v(-1143.76, 107.16) * mm});
            skLineSegment(sketch, "E394.MirrorCS", {"start": v(-1140.16, 119.75) * mm, "end": v(-1137.41, 118.16) * mm});
            skLineSegment(sketch, "E395.0", {"start": v(-1127.34, 134.34) * mm, "end": v(-1131.19, 136.56) * mm, "construction": true});
            skLineSegment(sketch, "E396", {"start": v(-1051.14, 90.34) * mm, "end": v(-1047.29, 92.57) * mm});
            skLineSegment(sketch, "E397.MirrorCS", {"start": v(-1060.54, 66.44) * mm, "end": v(-1063.29, 68.03) * mm, "construction": true});
            skLineSegment(sketch, "E398.MirrorCS", {"start": v(-1143.34, 66.44) * mm, "end": v(-1140.59, 68.03) * mm, "construction": true});
            skLineSegment(sketch, "E399.MirrorCS", {"start": v(-1101.94, 42.54) * mm, "end": v(-1101.94, 45.71) * mm, "construction": true});
            skLineSegment(sketch, "E400.MirrorCS", {"start": v(-1127.34, 46.35) * mm, "end": v(-1131.19, 44.13) * mm, "construction": true});
            skLineSegment(sketch, "E401.MirrorCS", {"start": v(-1072.69, 44.13) * mm, "end": v(-1076.54, 46.35) * mm});
            skLineSegment(sketch, "E402.MirrorCS", {"start": v(-1074.08, 49.33) * mm, "end": v(-1071.33, 47.74) * mm});
            skLineSegment(sketch, "E403.MirrorCS", {"start": v(-1140.16, 60.94) * mm, "end": v(-1137.41, 62.53) * mm});
            skLineSegment(sketch, "E404.MirrorCS", {"start": v(-1095.59, 42.54) * mm, "end": v(-1095.59, 45.71) * mm});
            skLineSegment(sketch, "E405.MirrorCS", {"start": v(-1076.54, 41.9) * mm, "end": v(-1076.54, 46.35) * mm});
            skLineSegment(sketch, "E406.MirrorCS", {"start": v(-1110.83, 42.54) * mm, "end": v(-1110.83, 45.71) * mm});
            skLineSegment(sketch, "E407.MirrorCS", {"start": v(-1064.98, 58.74) * mm, "end": v(-1067.73, 60.33) * mm});
            skLineSegment(sketch, "E408.MirrorCS", {"start": v(-1108.29, 42.54) * mm, "end": v(-1108.29, 45.71) * mm});
            skLineSegment(sketch, "E409.MirrorCS", {"start": v(-1129.8, 49.33) * mm, "end": v(-1132.54, 47.74) * mm});
            skLineSegment(sketch, "E410.MirrorCS", {"start": v(-1151.38, 86.73) * mm, "end": v(-1154.13, 85.14) * mm});
            skLineSegment(sketch, "E411.MirrorCS", {"start": v(-1146.51, 71.94) * mm, "end": v(-1143.76, 73.53) * mm});
            skLineSegment(sketch, "E412.MirrorCS", {"start": v(-1156.59, 88.12) * mm, "end": v(-1152.74, 90.34) * mm});
            skLineSegment(sketch, "E413.MirrorCS", {"start": v(-1063.71, 60.94) * mm, "end": v(-1066.46, 62.53) * mm});
            skLineSegment(sketch, "E414.MirrorCS", {"start": v(-1093.05, 42.54) * mm, "end": v(-1093.05, 45.71) * mm});
            skLineSegment(sketch, "E415.MirrorCS", {"start": v(-1147.78, 74.14) * mm, "end": v(-1145.03, 75.73) * mm});
            skLineSegment(sketch, "E416.MirrorCS", {"start": v(-1052.5, 86.73) * mm, "end": v(-1049.74, 85.14) * mm});
            skLineSegment(sketch, "E417.MirrorCS", {"start": v(-1123.53, 45.71) * mm, "end": v(-1123.53, 42.54) * mm});
            skLineSegment(sketch, "E418.MirrorCS", {"start": v(-1056.1, 74.14) * mm, "end": v(-1058.84, 75.73) * mm});
            skLineSegment(sketch, "E419.MirrorCS", {"start": v(-1051.14, 90.34) * mm, "end": v(-1047.29, 88.12) * mm});
            skLineSegment(sketch, "E420.MirrorCS", {"start": v(-1057.36, 71.94) * mm, "end": v(-1060.11, 73.53) * mm});
            skLineSegment(sketch, "E421.MirrorCS", {"start": v(-1138.9, 58.74) * mm, "end": v(-1136.14, 60.33) * mm});
            skLineSegment(sketch, "E422.MirrorCS", {"start": v(-1080.35, 45.71) * mm, "end": v(-1080.35, 42.54) * mm});
            skLineSegment(sketch, "E423.MirrorCS", {"start": v(-1066.46, 62.53) * mm, "end": v(-1063.29, 68.03) * mm});
            skLineSegment(sketch, "E424.MirrorCS", {"start": v(-1108.29, 45.71) * mm, "end": v(-1101.94, 45.71) * mm});
            skLineSegment(sketch, "E425.MirrorCS", {"start": v(-1060.54, 66.44) * mm, "end": v(-1057.36, 71.94) * mm});
            skLineSegment(sketch, "E426.MirrorCS", {"start": v(-1127.34, 41.9) * mm, "end": v(-1127.34, 46.35) * mm});
            skLineSegment(sketch, "E427.MirrorCS", {"start": v(-1101.94, 42.54) * mm, "end": v(-1095.59, 42.54) * mm});
            skLineSegment(sketch, "E428.MirrorCS", {"start": v(-1063.29, 68.03) * mm, "end": v(-1060.11, 73.53) * mm});
            skPoint(sketch, "E429.MirrorP", {"position": v(-1101.94, 44.13) * mm});
            skLineSegment(sketch, "E430.MirrorCS", {"start": v(-1101.94, 45.71) * mm, "end": v(-1095.59, 45.71) * mm});
            skLineSegment(sketch, "E431.MirrorCS", {"start": v(-1063.71, 60.94) * mm, "end": v(-1060.54, 66.44) * mm});
            skLineSegment(sketch, "E432.MirrorCS", {"start": v(-1108.29, 42.54) * mm, "end": v(-1101.94, 42.54) * mm});
            skLineSegment(sketch, "E433.MirrorCS", {"start": v(-1058.84, 75.73) * mm, "end": v(-1052.5, 86.73) * mm});
            skLineSegment(sketch, "E434.MirrorCS", {"start": v(-1093.05, 42.54) * mm, "end": v(-1080.35, 42.54) * mm});
            skLineSegment(sketch, "E435.MirrorCS", {"start": v(-1076.54, 46.35) * mm, "end": v(-1051.14, 90.34) * mm});
            skLineSegment(sketch, "E436.MirrorCS", {"start": v(-1071.33, 47.74) * mm, "end": v(-1064.98, 58.74) * mm});
            skLineSegment(sketch, "E437.MirrorCS", {"start": v(-1093.05, 45.71) * mm, "end": v(-1080.35, 45.71) * mm});
            skPoint(sketch, "E438.MirrorP", {"position": v(-1061.91, 67.24) * mm});
            skLineSegment(sketch, "E439.MirrorCS", {"start": v(-1056.1, 74.14) * mm, "end": v(-1049.74, 85.14) * mm});
            skLineSegment(sketch, "E440.MirrorCS", {"start": v(-1127.34, 46.35) * mm, "end": v(-1076.54, 46.35) * mm});
            skPoint(sketch, "E441.MirrorP", {"position": v(-1076.54, 44.13) * mm});
            skLineSegment(sketch, "E442.MirrorCS", {"start": v(-1127.34, 41.9) * mm, "end": v(-1076.54, 41.9) * mm});
            skLineSegment(sketch, "E443.MirrorCS", {"start": v(-1123.53, 45.71) * mm, "end": v(-1110.83, 45.71) * mm});
            skLineSegment(sketch, "E444.MirrorCS", {"start": v(-1127.34, 44.13) * mm, "end": v(-1076.54, 44.13) * mm, "construction": true});
            skLineSegment(sketch, "E445.MirrorCS", {"start": v(-1074.08, 49.33) * mm, "end": v(-1067.73, 60.33) * mm});
            skLineSegment(sketch, "E446.MirrorCS", {"start": v(-1072.69, 44.13) * mm, "end": v(-1047.29, 88.12) * mm});
            skLineSegment(sketch, "E447.MirrorCS", {"start": v(-1123.53, 42.54) * mm, "end": v(-1110.83, 42.54) * mm});
            skPoint(sketch, "E448.MirrorP", {"position": v(-1049.21, 89.23) * mm});
            skLineSegment(sketch, "E449", {"start": v(-1127.34, 226.77) * mm, "end": v(-1076.54, 226.77) * mm});
            skLineSegment(sketch, "E450", {"start": v(-1127.34, 231.22) * mm, "end": v(-1127.34, 226.77) * mm});
            skLineSegment(sketch, "E451", {"start": v(-1076.54, 231.22) * mm, "end": v(-1076.54, 226.77) * mm});
            skLineSegment(sketch, "E452", {"start": v(-1152.74, 182.78) * mm, "end": v(-1051.14, 182.78) * mm, "construction": true});
            skPoint(sketch, "E453.endSnap0", {"position": v(-1076.54, 229) * mm});
            skLineSegment(sketch, "E454", {"start": v(-1127.34, 229) * mm, "end": v(-1076.54, 229) * mm, "construction": true});
            skLineSegment(sketch, "E455", {"start": v(-1127.34, 231.22) * mm, "end": v(-1076.54, 231.22) * mm});
            skLineSegment(sketch, "E456", {"start": v(-1156.59, 185) * mm, "end": v(-1152.74, 182.78) * mm});
            skLineSegment(sketch, "E457.left", {"start": v(-1080.35, 227.4) * mm, "end": v(-1080.35, 230.58) * mm});
            skLineSegment(sketch, "E457.right", {"start": v(-1123.53, 227.4) * mm, "end": v(-1123.53, 230.58) * mm});
            skPoint(sketch, "E457.middle", {"position": v(-1101.94, 229) * mm});
            skLineSegment(sketch, "E458", {"start": v(-1101.94, 230.58) * mm, "end": v(-1101.94, 227.4) * mm, "construction": true});
            skLineSegment(sketch, "E459", {"start": v(-1110.83, 230.58) * mm, "end": v(-1110.83, 227.4) * mm});
            skLineSegment(sketch, "E460.MirrorCS", {"start": v(-1093.05, 230.58) * mm, "end": v(-1093.05, 227.4) * mm});
            skLineSegment(sketch, "E461", {"start": v(-1108.29, 230.58) * mm, "end": v(-1108.29, 227.4) * mm});
            skLineSegment(sketch, "E462.MirrorCS", {"start": v(-1095.59, 230.58) * mm, "end": v(-1095.59, 227.4) * mm});
            skLineSegment(sketch, "E463", {"start": v(-1123.53, 230.58) * mm, "end": v(-1110.83, 230.58) * mm});
            skLineSegment(sketch, "E464", {"start": v(-1123.53, 227.4) * mm, "end": v(-1110.83, 227.4) * mm});
            skLineSegment(sketch, "E465", {"start": v(-1108.29, 227.4) * mm, "end": v(-1101.94, 227.4) * mm});
            skLineSegment(sketch, "E466", {"start": v(-1108.29, 230.58) * mm, "end": v(-1101.94, 230.58) * mm});
            skLineSegment(sketch, "E467", {"start": v(-1101.94, 230.58) * mm, "end": v(-1095.59, 230.58) * mm});
            skLineSegment(sketch, "E468", {"start": v(-1101.94, 227.4) * mm, "end": v(-1095.59, 227.4) * mm});
            skLineSegment(sketch, "E469", {"start": v(-1093.05, 230.58) * mm, "end": v(-1080.35, 230.58) * mm});
            skLineSegment(sketch, "E470", {"start": v(-1093.05, 227.4) * mm, "end": v(-1080.35, 227.4) * mm});
            skLineSegment(sketch, "E471", {"start": v(-1076.54, 226.77) * mm, "end": v(-1051.14, 182.78) * mm});
            skLineSegment(sketch, "E472", {"start": v(-1072.69, 229) * mm, "end": v(-1076.54, 226.77) * mm});
            skPoint(sketch, "E473.endSnap0", {"position": v(-1049.21, 183.89) * mm});
            skLineSegment(sketch, "E474", {"start": v(-1072.69, 229) * mm, "end": v(-1047.29, 185) * mm});
            skLineSegment(sketch, "E475.left", {"start": v(-1052.5, 186.4) * mm, "end": v(-1049.74, 187.98) * mm});
            skLineSegment(sketch, "E475.right", {"start": v(-1074.08, 223.79) * mm, "end": v(-1071.33, 225.38) * mm});
            skPoint(sketch, "E475.middle", {"position": v(-1061.91, 205.89) * mm});
            skLineSegment(sketch, "E476", {"start": v(-1060.54, 206.68) * mm, "end": v(-1063.29, 205.1) * mm, "construction": true});
            skLineSegment(sketch, "E477", {"start": v(-1064.98, 214.38) * mm, "end": v(-1067.73, 212.8) * mm});
            skLineSegment(sketch, "E478.MirrorCS", {"start": v(-1056.1, 198.98) * mm, "end": v(-1058.84, 197.4) * mm});
            skLineSegment(sketch, "E479", {"start": v(-1063.71, 212.18) * mm, "end": v(-1066.46, 210.6) * mm});
            skLineSegment(sketch, "E480.MirrorCS", {"start": v(-1057.36, 201.18) * mm, "end": v(-1060.11, 199.6) * mm});
            skLineSegment(sketch, "E481", {"start": v(-1071.33, 225.38) * mm, "end": v(-1064.98, 214.38) * mm});
            skLineSegment(sketch, "E482", {"start": v(-1074.08, 223.79) * mm, "end": v(-1067.73, 212.8) * mm});
            skLineSegment(sketch, "E483", {"start": v(-1066.46, 210.6) * mm, "end": v(-1063.29, 205.1) * mm});
            skLineSegment(sketch, "E484", {"start": v(-1063.71, 212.18) * mm, "end": v(-1060.54, 206.68) * mm});
            skLineSegment(sketch, "E485", {"start": v(-1060.54, 206.68) * mm, "end": v(-1057.36, 201.18) * mm});
            skLineSegment(sketch, "E486", {"start": v(-1063.29, 205.1) * mm, "end": v(-1060.11, 199.6) * mm});
            skLineSegment(sketch, "E487", {"start": v(-1056.1, 198.98) * mm, "end": v(-1049.74, 187.98) * mm});
            skLineSegment(sketch, "E488", {"start": v(-1058.84, 197.4) * mm, "end": v(-1052.5, 186.4) * mm});
            skLineSegment(sketch, "E489.left", {"start": v(-1129.8, 223.79) * mm, "end": v(-1132.54, 225.38) * mm});
            skLineSegment(sketch, "E489.right", {"start": v(-1151.38, 186.4) * mm, "end": v(-1154.13, 187.98) * mm});
            skLineSegment(sketch, "E490", {"start": v(-1143.34, 206.68) * mm, "end": v(-1140.59, 205.1) * mm, "construction": true});
            skLineSegment(sketch, "E491", {"start": v(-1147.78, 198.98) * mm, "end": v(-1145.03, 197.4) * mm});
            skLineSegment(sketch, "E492.MirrorCS", {"start": v(-1138.9, 214.38) * mm, "end": v(-1136.14, 212.8) * mm});
            skLineSegment(sketch, "E493", {"start": v(-1146.51, 201.18) * mm, "end": v(-1143.76, 199.6) * mm});
            skLineSegment(sketch, "E494.MirrorCS", {"start": v(-1140.16, 212.18) * mm, "end": v(-1137.41, 210.6) * mm});
            skLineSegment(sketch, "E495.0", {"start": v(-1127.34, 226.77) * mm, "end": v(-1131.19, 229) * mm, "construction": true});
            skLineSegment(sketch, "E496", {"start": v(-1051.14, 182.78) * mm, "end": v(-1047.29, 185) * mm});
            skLineSegment(sketch, "E497.MirrorCS", {"start": v(-1060.54, 158.87) * mm, "end": v(-1063.29, 160.46) * mm, "construction": true});
            skLineSegment(sketch, "E498.MirrorCS", {"start": v(-1143.34, 158.87) * mm, "end": v(-1140.59, 160.46) * mm, "construction": true});
            skLineSegment(sketch, "E499.MirrorCS", {"start": v(-1101.94, 134.97) * mm, "end": v(-1101.94, 138.15) * mm, "construction": true});
            skLineSegment(sketch, "E500.MirrorCS", {"start": v(-1127.34, 138.78) * mm, "end": v(-1131.19, 136.56) * mm, "construction": true});
            skLineSegment(sketch, "E501.MirrorCS", {"start": v(-1072.69, 136.56) * mm, "end": v(-1076.54, 138.78) * mm});
            skLineSegment(sketch, "E502.MirrorCS", {"start": v(-1074.08, 141.76) * mm, "end": v(-1071.33, 140.18) * mm});
            skLineSegment(sketch, "E503.MirrorCS", {"start": v(-1140.16, 153.38) * mm, "end": v(-1137.41, 154.96) * mm});
            skLineSegment(sketch, "E504.MirrorCS", {"start": v(-1095.59, 134.97) * mm, "end": v(-1095.59, 138.15) * mm});
            skLineSegment(sketch, "E505.MirrorCS", {"start": v(-1076.54, 134.34) * mm, "end": v(-1076.54, 138.78) * mm});
            skLineSegment(sketch, "E506.MirrorCS", {"start": v(-1110.83, 134.97) * mm, "end": v(-1110.83, 138.15) * mm});
            skLineSegment(sketch, "E507.MirrorCS", {"start": v(-1064.98, 151.18) * mm, "end": v(-1067.73, 152.76) * mm});
            skLineSegment(sketch, "E508.MirrorCS", {"start": v(-1108.29, 134.97) * mm, "end": v(-1108.29, 138.15) * mm});
            skLineSegment(sketch, "E509.MirrorCS", {"start": v(-1129.8, 141.76) * mm, "end": v(-1132.54, 140.18) * mm});
            skLineSegment(sketch, "E510.MirrorCS", {"start": v(-1151.38, 179.16) * mm, "end": v(-1154.13, 177.57) * mm});
            skLineSegment(sketch, "E511.MirrorCS", {"start": v(-1146.51, 164.37) * mm, "end": v(-1143.76, 165.96) * mm});
            skLineSegment(sketch, "E512.MirrorCS", {"start": v(-1156.59, 180.55) * mm, "end": v(-1152.74, 182.78) * mm});
            skLineSegment(sketch, "E513.MirrorCS", {"start": v(-1063.71, 153.38) * mm, "end": v(-1066.46, 154.96) * mm});
            skLineSegment(sketch, "E514.MirrorCS", {"start": v(-1093.05, 134.97) * mm, "end": v(-1093.05, 138.15) * mm});
            skLineSegment(sketch, "E515.MirrorCS", {"start": v(-1147.78, 166.57) * mm, "end": v(-1145.03, 168.16) * mm});
            skLineSegment(sketch, "E516.MirrorCS", {"start": v(-1052.5, 179.16) * mm, "end": v(-1049.74, 177.57) * mm});
            skLineSegment(sketch, "E517.MirrorCS", {"start": v(-1123.53, 138.15) * mm, "end": v(-1123.53, 134.97) * mm});
            skLineSegment(sketch, "E518.MirrorCS", {"start": v(-1056.1, 166.57) * mm, "end": v(-1058.84, 168.16) * mm});
            skLineSegment(sketch, "E519.MirrorCS", {"start": v(-1051.14, 182.78) * mm, "end": v(-1047.29, 180.55) * mm});
            skLineSegment(sketch, "E520.MirrorCS", {"start": v(-1057.36, 164.37) * mm, "end": v(-1060.11, 165.96) * mm});
            skLineSegment(sketch, "E521.MirrorCS", {"start": v(-1138.9, 151.18) * mm, "end": v(-1136.14, 152.76) * mm});
            skLineSegment(sketch, "E522.MirrorCS", {"start": v(-1080.35, 138.15) * mm, "end": v(-1080.35, 134.97) * mm});
            skLineSegment(sketch, "E523.MirrorCS", {"start": v(-1066.46, 154.96) * mm, "end": v(-1063.29, 160.46) * mm});
            skLineSegment(sketch, "E524.MirrorCS", {"start": v(-1060.54, 158.87) * mm, "end": v(-1057.36, 164.37) * mm});
            skLineSegment(sketch, "E525.MirrorCS", {"start": v(-1127.34, 134.34) * mm, "end": v(-1127.34, 138.78) * mm});
            skLineSegment(sketch, "E526.MirrorCS", {"start": v(-1063.29, 160.46) * mm, "end": v(-1060.11, 165.96) * mm});
            skLineSegment(sketch, "E527.MirrorCS", {"start": v(-1063.71, 153.38) * mm, "end": v(-1060.54, 158.87) * mm});
            skLineSegment(sketch, "E528.MirrorCS", {"start": v(-1058.84, 168.16) * mm, "end": v(-1052.5, 179.16) * mm});
            skLineSegment(sketch, "E529.MirrorCS", {"start": v(-1076.54, 138.78) * mm, "end": v(-1051.14, 182.78) * mm});
            skLineSegment(sketch, "E530.MirrorCS", {"start": v(-1071.33, 140.18) * mm, "end": v(-1064.98, 151.18) * mm});
            skPoint(sketch, "E531.MirrorP", {"position": v(-1061.91, 159.67) * mm});
            skLineSegment(sketch, "E532.MirrorCS", {"start": v(-1056.1, 166.57) * mm, "end": v(-1049.74, 177.57) * mm});
            skLineSegment(sketch, "E533.MirrorCS", {"start": v(-1074.08, 141.76) * mm, "end": v(-1067.73, 152.76) * mm});
            skLineSegment(sketch, "E534.MirrorCS", {"start": v(-1072.69, 136.56) * mm, "end": v(-1047.29, 180.55) * mm});
            skPoint(sketch, "E535.MirrorP", {"position": v(-1049.21, 181.67) * mm});
            skLineSegment(sketch, "E536", {"start": v(-1127.34, 319.2) * mm, "end": v(-1076.54, 319.2) * mm});
            skLineSegment(sketch, "E537", {"start": v(-1127.34, 323.65) * mm, "end": v(-1127.34, 319.2) * mm});
            skLineSegment(sketch, "E538", {"start": v(-1076.54, 323.65) * mm, "end": v(-1076.54, 319.2) * mm});
            skLineSegment(sketch, "E539", {"start": v(-1152.74, 275.21) * mm, "end": v(-1051.14, 275.21) * mm, "construction": true});
            skPoint(sketch, "E540.endSnap0", {"position": v(-1076.54, 321.43) * mm});
            skLineSegment(sketch, "E541", {"start": v(-1127.34, 321.43) * mm, "end": v(-1076.54, 321.43) * mm, "construction": true});
            skLineSegment(sketch, "E542", {"start": v(-1127.34, 323.65) * mm, "end": v(-1076.54, 323.65) * mm});
            skLineSegment(sketch, "E543", {"start": v(-1156.59, 277.43) * mm, "end": v(-1152.74, 275.21) * mm});
            skLineSegment(sketch, "E544.left", {"start": v(-1080.35, 319.84) * mm, "end": v(-1080.35, 323.01) * mm});
            skLineSegment(sketch, "E544.right", {"start": v(-1123.53, 319.84) * mm, "end": v(-1123.53, 323.01) * mm});
            skPoint(sketch, "E544.middle", {"position": v(-1101.94, 321.43) * mm});
            skLineSegment(sketch, "E545", {"start": v(-1101.94, 323.01) * mm, "end": v(-1101.94, 319.84) * mm, "construction": true});
            skLineSegment(sketch, "E546", {"start": v(-1110.83, 323.01) * mm, "end": v(-1110.83, 319.84) * mm});
            skLineSegment(sketch, "E547.MirrorCS", {"start": v(-1093.05, 323.01) * mm, "end": v(-1093.05, 319.84) * mm});
            skLineSegment(sketch, "E548", {"start": v(-1108.29, 323.01) * mm, "end": v(-1108.29, 319.84) * mm});
            skLineSegment(sketch, "E549.MirrorCS", {"start": v(-1095.59, 323.01) * mm, "end": v(-1095.59, 319.84) * mm});
            skLineSegment(sketch, "E550", {"start": v(-1123.53, 323.01) * mm, "end": v(-1110.83, 323.01) * mm});
            skLineSegment(sketch, "E551", {"start": v(-1123.53, 319.84) * mm, "end": v(-1110.83, 319.84) * mm});
            skLineSegment(sketch, "E552", {"start": v(-1108.29, 319.84) * mm, "end": v(-1101.94, 319.84) * mm});
            skLineSegment(sketch, "E553", {"start": v(-1108.29, 323.01) * mm, "end": v(-1101.94, 323.01) * mm});
            skLineSegment(sketch, "E554", {"start": v(-1101.94, 323.01) * mm, "end": v(-1095.59, 323.01) * mm});
            skLineSegment(sketch, "E555", {"start": v(-1101.94, 319.84) * mm, "end": v(-1095.59, 319.84) * mm});
            skLineSegment(sketch, "E556", {"start": v(-1093.05, 323.01) * mm, "end": v(-1080.35, 323.01) * mm});
            skLineSegment(sketch, "E557", {"start": v(-1093.05, 319.84) * mm, "end": v(-1080.35, 319.84) * mm});
            skLineSegment(sketch, "E558", {"start": v(-1076.54, 319.2) * mm, "end": v(-1051.14, 275.21) * mm});
            skLineSegment(sketch, "E559", {"start": v(-1072.69, 321.43) * mm, "end": v(-1076.54, 319.2) * mm});
            skPoint(sketch, "E560.endSnap0", {"position": v(-1049.21, 276.32) * mm});
            skLineSegment(sketch, "E561", {"start": v(-1072.69, 321.43) * mm, "end": v(-1047.29, 277.43) * mm});
            skLineSegment(sketch, "E562.left", {"start": v(-1052.5, 278.83) * mm, "end": v(-1049.74, 280.41) * mm});
            skLineSegment(sketch, "E562.right", {"start": v(-1074.08, 316.22) * mm, "end": v(-1071.33, 317.8) * mm});
            skPoint(sketch, "E562.middle", {"position": v(-1061.91, 298.32) * mm});
            skLineSegment(sketch, "E563", {"start": v(-1060.54, 299.11) * mm, "end": v(-1063.29, 297.52) * mm, "construction": true});
            skLineSegment(sketch, "E564", {"start": v(-1064.98, 306.81) * mm, "end": v(-1067.73, 305.22) * mm});
            skLineSegment(sketch, "E565.MirrorCS", {"start": v(-1056.1, 291.41) * mm, "end": v(-1058.84, 289.83) * mm});
            skLineSegment(sketch, "E566", {"start": v(-1063.71, 304.61) * mm, "end": v(-1066.46, 303.02) * mm});
            skLineSegment(sketch, "E567.MirrorCS", {"start": v(-1057.36, 293.61) * mm, "end": v(-1060.11, 292.03) * mm});
            skLineSegment(sketch, "E568", {"start": v(-1071.33, 317.8) * mm, "end": v(-1064.98, 306.81) * mm});
            skLineSegment(sketch, "E569", {"start": v(-1074.08, 316.22) * mm, "end": v(-1067.73, 305.22) * mm});
            skLineSegment(sketch, "E570", {"start": v(-1066.46, 303.02) * mm, "end": v(-1063.29, 297.52) * mm});
            skLineSegment(sketch, "E571", {"start": v(-1063.71, 304.61) * mm, "end": v(-1060.54, 299.11) * mm});
            skLineSegment(sketch, "E572", {"start": v(-1060.54, 299.11) * mm, "end": v(-1057.36, 293.61) * mm});
            skLineSegment(sketch, "E573", {"start": v(-1063.29, 297.52) * mm, "end": v(-1060.11, 292.03) * mm});
            skLineSegment(sketch, "E574", {"start": v(-1056.1, 291.41) * mm, "end": v(-1049.74, 280.41) * mm});
            skLineSegment(sketch, "E575", {"start": v(-1058.84, 289.83) * mm, "end": v(-1052.5, 278.83) * mm});
            skLineSegment(sketch, "E576", {"start": v(-1152.74, 275.21) * mm, "end": v(-1127.34, 319.2) * mm});
            skLineSegment(sketch, "E577", {"start": v(-1131.19, 321.43) * mm, "end": v(-1127.34, 319.2) * mm});
            skPoint(sketch, "E578.endSnap0", {"position": v(-1129.26, 320.32) * mm});
            skLineSegment(sketch, "E579", {"start": v(-1156.59, 277.43) * mm, "end": v(-1131.19, 321.43) * mm});
            skLineSegment(sketch, "E580.left", {"start": v(-1129.8, 316.22) * mm, "end": v(-1132.54, 317.8) * mm});
            skLineSegment(sketch, "E580.right", {"start": v(-1151.38, 278.83) * mm, "end": v(-1154.13, 280.41) * mm});
            skPoint(sketch, "E580.middle", {"position": v(-1141.96, 298.32) * mm});
            skLineSegment(sketch, "E581", {"start": v(-1143.34, 299.11) * mm, "end": v(-1140.59, 297.52) * mm, "construction": true});
            skLineSegment(sketch, "E582", {"start": v(-1147.78, 291.41) * mm, "end": v(-1145.03, 289.83) * mm});
            skLineSegment(sketch, "E583.MirrorCS", {"start": v(-1138.9, 306.81) * mm, "end": v(-1136.14, 305.22) * mm});
            skLineSegment(sketch, "E584", {"start": v(-1146.51, 293.61) * mm, "end": v(-1143.76, 292.03) * mm});
            skLineSegment(sketch, "E585.MirrorCS", {"start": v(-1140.16, 304.61) * mm, "end": v(-1137.41, 303.02) * mm});
            skLineSegment(sketch, "E586", {"start": v(-1154.13, 280.41) * mm, "end": v(-1147.78, 291.41) * mm});
            skLineSegment(sketch, "E587", {"start": v(-1151.38, 278.83) * mm, "end": v(-1145.03, 289.83) * mm});
            skLineSegment(sketch, "E588", {"start": v(-1143.76, 292.03) * mm, "end": v(-1140.59, 297.52) * mm});
            skLineSegment(sketch, "E589", {"start": v(-1146.51, 293.61) * mm, "end": v(-1143.34, 299.11) * mm});
            skLineSegment(sketch, "E590", {"start": v(-1143.34, 299.11) * mm, "end": v(-1140.16, 304.61) * mm});
            skLineSegment(sketch, "E591", {"start": v(-1140.59, 297.52) * mm, "end": v(-1137.41, 303.02) * mm});
            skLineSegment(sketch, "E592", {"start": v(-1138.9, 306.81) * mm, "end": v(-1132.54, 317.8) * mm});
            skLineSegment(sketch, "E593", {"start": v(-1136.14, 305.22) * mm, "end": v(-1129.8, 316.22) * mm});
            skLineSegment(sketch, "E594.0", {"start": v(-1127.34, 319.2) * mm, "end": v(-1131.19, 321.43) * mm, "construction": true});
            skLineSegment(sketch, "E595", {"start": v(-1051.14, 275.21) * mm, "end": v(-1047.29, 277.43) * mm});
            skLineSegment(sketch, "E596.MirrorCS", {"start": v(-1060.54, 251.3) * mm, "end": v(-1063.29, 252.9) * mm, "construction": true});
            skLineSegment(sketch, "E597.MirrorCS", {"start": v(-1143.34, 251.3) * mm, "end": v(-1140.59, 252.9) * mm, "construction": true});
            skLineSegment(sketch, "E598.MirrorCS", {"start": v(-1101.94, 227.4) * mm, "end": v(-1101.94, 230.58) * mm, "construction": true});
            skLineSegment(sketch, "E599.MirrorCS", {"start": v(-1127.34, 231.22) * mm, "end": v(-1131.19, 229) * mm, "construction": true});
            skLineSegment(sketch, "E600.MirrorCS", {"start": v(-1072.69, 229) * mm, "end": v(-1076.54, 231.22) * mm});
            skLineSegment(sketch, "E601.MirrorCS", {"start": v(-1074.08, 234.2) * mm, "end": v(-1071.33, 232.61) * mm});
            skLineSegment(sketch, "E602.MirrorCS", {"start": v(-1140.16, 245.8) * mm, "end": v(-1137.41, 247.4) * mm});
            skLineSegment(sketch, "E603.MirrorCS", {"start": v(-1095.59, 227.4) * mm, "end": v(-1095.59, 230.58) * mm});
            skLineSegment(sketch, "E604.MirrorCS", {"start": v(-1076.54, 226.77) * mm, "end": v(-1076.54, 231.22) * mm});
            skLineSegment(sketch, "E605.MirrorCS", {"start": v(-1110.83, 227.4) * mm, "end": v(-1110.83, 230.58) * mm});
            skLineSegment(sketch, "E606.MirrorCS", {"start": v(-1064.98, 243.6) * mm, "end": v(-1067.73, 245.2) * mm});
            skLineSegment(sketch, "E607.MirrorCS", {"start": v(-1108.29, 227.4) * mm, "end": v(-1108.29, 230.58) * mm});
            skLineSegment(sketch, "E608.MirrorCS", {"start": v(-1129.8, 234.2) * mm, "end": v(-1132.54, 232.61) * mm});
            skLineSegment(sketch, "E609.MirrorCS", {"start": v(-1151.38, 271.6) * mm, "end": v(-1154.13, 270) * mm});
            skLineSegment(sketch, "E610.MirrorCS", {"start": v(-1146.51, 256.8) * mm, "end": v(-1143.76, 258.4) * mm});
            skLineSegment(sketch, "E611.MirrorCS", {"start": v(-1156.59, 272.99) * mm, "end": v(-1152.74, 275.21) * mm});
            skLineSegment(sketch, "E612.MirrorCS", {"start": v(-1063.71, 245.8) * mm, "end": v(-1066.46, 247.4) * mm});
            skLineSegment(sketch, "E613.MirrorCS", {"start": v(-1093.05, 227.4) * mm, "end": v(-1093.05, 230.58) * mm});
            skLineSegment(sketch, "E614.MirrorCS", {"start": v(-1147.78, 259) * mm, "end": v(-1145.03, 260.6) * mm});
            skLineSegment(sketch, "E615.MirrorCS", {"start": v(-1052.5, 271.6) * mm, "end": v(-1049.74, 270) * mm});
            skLineSegment(sketch, "E616.MirrorCS", {"start": v(-1123.53, 230.58) * mm, "end": v(-1123.53, 227.4) * mm});
            skLineSegment(sketch, "E617.MirrorCS", {"start": v(-1056.1, 259) * mm, "end": v(-1058.84, 260.6) * mm});
            skLineSegment(sketch, "E618.MirrorCS", {"start": v(-1051.14, 275.21) * mm, "end": v(-1047.29, 272.99) * mm});
            skLineSegment(sketch, "E619.MirrorCS", {"start": v(-1057.36, 256.8) * mm, "end": v(-1060.11, 258.4) * mm});
            skLineSegment(sketch, "E620.MirrorCS", {"start": v(-1138.9, 243.6) * mm, "end": v(-1136.14, 245.2) * mm});
            skLineSegment(sketch, "E621.MirrorCS", {"start": v(-1080.35, 230.58) * mm, "end": v(-1080.35, 227.4) * mm});
            skLineSegment(sketch, "E622.MirrorCS", {"start": v(-1066.46, 247.4) * mm, "end": v(-1063.29, 252.9) * mm});
            skLineSegment(sketch, "E623.MirrorCS", {"start": v(-1060.54, 251.3) * mm, "end": v(-1057.36, 256.8) * mm});
            skLineSegment(sketch, "E624.MirrorCS", {"start": v(-1127.34, 226.77) * mm, "end": v(-1127.34, 231.22) * mm});
            skLineSegment(sketch, "E625.MirrorCS", {"start": v(-1063.29, 252.9) * mm, "end": v(-1060.11, 258.4) * mm});
            skLineSegment(sketch, "E626.MirrorCS", {"start": v(-1063.71, 245.8) * mm, "end": v(-1060.54, 251.3) * mm});
            skLineSegment(sketch, "E627.MirrorCS", {"start": v(-1058.84, 260.6) * mm, "end": v(-1052.5, 271.6) * mm});
            skLineSegment(sketch, "E628.MirrorCS", {"start": v(-1076.54, 231.22) * mm, "end": v(-1051.14, 275.21) * mm});
            skLineSegment(sketch, "E629.MirrorCS", {"start": v(-1071.33, 232.61) * mm, "end": v(-1064.98, 243.6) * mm});
            skPoint(sketch, "E630.MirrorP", {"position": v(-1061.91, 252.1) * mm});
            skLineSegment(sketch, "E631.MirrorCS", {"start": v(-1056.1, 259) * mm, "end": v(-1049.74, 270) * mm});
            skLineSegment(sketch, "E632.MirrorCS", {"start": v(-1074.08, 234.2) * mm, "end": v(-1067.73, 245.2) * mm});
            skLineSegment(sketch, "E633.MirrorCS", {"start": v(-1072.69, 229) * mm, "end": v(-1047.29, 272.99) * mm});
            skPoint(sketch, "E634.MirrorP", {"position": v(-1049.21, 274.1) * mm});
            skLineSegment(sketch, "E635", {"start": v(-1047.29, 88.12) * mm, "end": v(-996.49, 88.12) * mm});
            skLineSegment(sketch, "E636", {"start": v(-1047.29, 92.57) * mm, "end": v(-1047.29, 88.12) * mm});
            skLineSegment(sketch, "E637", {"start": v(-996.49, 92.57) * mm, "end": v(-996.49, 88.12) * mm});
            skLineSegment(sketch, "E638", {"start": v(-1072.69, 44.13) * mm, "end": v(-971.09, 44.13) * mm, "construction": true});
            skPoint(sketch, "E639.endSnap0", {"position": v(-996.49, 90.34) * mm});
            skLineSegment(sketch, "E640", {"start": v(-1047.29, 90.34) * mm, "end": v(-996.49, 90.34) * mm, "construction": true});
            skLineSegment(sketch, "E641", {"start": v(-1047.29, 92.57) * mm, "end": v(-996.49, 92.57) * mm});
            skLineSegment(sketch, "E642", {"start": v(-1076.54, 46.35) * mm, "end": v(-1072.69, 44.13) * mm});
            skLineSegment(sketch, "E643.left", {"start": v(-1000.3, 88.76) * mm, "end": v(-1000.3, 91.93) * mm});
            skLineSegment(sketch, "E643.right", {"start": v(-1043.48, 88.76) * mm, "end": v(-1043.48, 91.93) * mm});
            skPoint(sketch, "E643.middle", {"position": v(-1021.89, 90.34) * mm});
            skLineSegment(sketch, "E644", {"start": v(-1021.89, 91.93) * mm, "end": v(-1021.89, 88.76) * mm, "construction": true});
            skLineSegment(sketch, "E645", {"start": v(-1030.78, 91.93) * mm, "end": v(-1030.78, 88.76) * mm});
            skLineSegment(sketch, "E646.MirrorCS", {"start": v(-1013, 91.93) * mm, "end": v(-1013, 88.76) * mm});
            skLineSegment(sketch, "E647", {"start": v(-1028.24, 91.93) * mm, "end": v(-1028.24, 88.76) * mm});
            skLineSegment(sketch, "E648.MirrorCS", {"start": v(-1015.54, 91.93) * mm, "end": v(-1015.54, 88.76) * mm});
            skLineSegment(sketch, "E649", {"start": v(-1043.48, 91.93) * mm, "end": v(-1030.78, 91.93) * mm});
            skLineSegment(sketch, "E650", {"start": v(-1043.48, 88.76) * mm, "end": v(-1030.78, 88.76) * mm});
            skLineSegment(sketch, "E651", {"start": v(-1028.24, 88.76) * mm, "end": v(-1021.89, 88.76) * mm});
            skLineSegment(sketch, "E652", {"start": v(-1028.24, 91.93) * mm, "end": v(-1021.89, 91.93) * mm});
            skLineSegment(sketch, "E653", {"start": v(-1021.89, 91.93) * mm, "end": v(-1015.54, 91.93) * mm});
            skLineSegment(sketch, "E654", {"start": v(-1021.89, 88.76) * mm, "end": v(-1015.54, 88.76) * mm});
            skLineSegment(sketch, "E655", {"start": v(-1013, 91.93) * mm, "end": v(-1000.3, 91.93) * mm});
            skLineSegment(sketch, "E656", {"start": v(-1013, 88.76) * mm, "end": v(-1000.3, 88.76) * mm});
            skLineSegment(sketch, "E657", {"start": v(-996.49, 88.12) * mm, "end": v(-971.09, 44.13) * mm});
            skLineSegment(sketch, "E658", {"start": v(-992.64, 90.34) * mm, "end": v(-996.49, 88.12) * mm});
            skPoint(sketch, "E659.endSnap0", {"position": v(-969.17, 45.24) * mm});
            skLineSegment(sketch, "E660", {"start": v(-992.64, 90.34) * mm, "end": v(-967.24, 46.35) * mm});
            skLineSegment(sketch, "E661.left", {"start": v(-972.44, 47.74) * mm, "end": v(-969.7, 49.33) * mm});
            skLineSegment(sketch, "E661.right", {"start": v(-994.03, 85.14) * mm, "end": v(-991.29, 86.73) * mm});
            skPoint(sketch, "E661.middle", {"position": v(-981.87, 67.24) * mm});
            skLineSegment(sketch, "E662", {"start": v(-980.5, 68.03) * mm, "end": v(-983.24, 66.44) * mm, "construction": true});
            skLineSegment(sketch, "E663", {"start": v(-984.94, 75.73) * mm, "end": v(-987.68, 74.14) * mm});
            skLineSegment(sketch, "E664.MirrorCS", {"start": v(-976.05, 60.33) * mm, "end": v(-978.8, 58.74) * mm});
            skLineSegment(sketch, "E665", {"start": v(-983.67, 73.53) * mm, "end": v(-986.41, 71.94) * mm});
            skLineSegment(sketch, "E666.MirrorCS", {"start": v(-977.32, 62.53) * mm, "end": v(-980.06, 60.94) * mm});
            skLineSegment(sketch, "E667", {"start": v(-991.29, 86.73) * mm, "end": v(-984.94, 75.73) * mm});
            skLineSegment(sketch, "E668", {"start": v(-994.03, 85.14) * mm, "end": v(-987.68, 74.14) * mm});
            skLineSegment(sketch, "E669", {"start": v(-986.41, 71.94) * mm, "end": v(-983.24, 66.44) * mm});
            skLineSegment(sketch, "E670", {"start": v(-983.67, 73.53) * mm, "end": v(-980.5, 68.03) * mm});
            skLineSegment(sketch, "E671", {"start": v(-980.5, 68.03) * mm, "end": v(-977.32, 62.53) * mm});
            skLineSegment(sketch, "E672", {"start": v(-983.24, 66.44) * mm, "end": v(-980.06, 60.94) * mm});
            skLineSegment(sketch, "E673", {"start": v(-976.05, 60.33) * mm, "end": v(-969.7, 49.33) * mm});
            skLineSegment(sketch, "E674", {"start": v(-978.8, 58.74) * mm, "end": v(-972.44, 47.74) * mm});
            skLineSegment(sketch, "E675.left", {"start": v(-1049.74, 85.14) * mm, "end": v(-1052.5, 86.73) * mm});
            skLineSegment(sketch, "E675.right", {"start": v(-1071.33, 47.74) * mm, "end": v(-1074.08, 49.33) * mm});
            skLineSegment(sketch, "E676", {"start": v(-1063.29, 68.03) * mm, "end": v(-1060.54, 66.44) * mm, "construction": true});
            skLineSegment(sketch, "E677", {"start": v(-1067.73, 60.33) * mm, "end": v(-1064.98, 58.74) * mm});
            skLineSegment(sketch, "E678.MirrorCS", {"start": v(-1058.84, 75.73) * mm, "end": v(-1056.1, 74.14) * mm});
            skLineSegment(sketch, "E679", {"start": v(-1066.46, 62.53) * mm, "end": v(-1063.71, 60.94) * mm});
            skLineSegment(sketch, "E680.MirrorCS", {"start": v(-1060.11, 73.53) * mm, "end": v(-1057.36, 71.94) * mm});
            skLineSegment(sketch, "E681.0", {"start": v(-1047.29, 88.12) * mm, "end": v(-1051.14, 90.34) * mm, "construction": true});
            skLineSegment(sketch, "E682", {"start": v(-971.09, 44.13) * mm, "end": v(-967.24, 46.35) * mm});
            skLineSegment(sketch, "E683.MirrorCS", {"start": v(-1051.14, -2.09) * mm, "end": v(-1047.29, 0.13) * mm});
            skLineSegment(sketch, "E684.MirrorCS", {"start": v(-980.5, 20.23) * mm, "end": v(-983.24, 21.81) * mm, "construction": true});
            skLineSegment(sketch, "E685.MirrorCS", {"start": v(-1063.29, 20.23) * mm, "end": v(-1060.54, 21.81) * mm, "construction": true});
            skLineSegment(sketch, "E686.MirrorCS", {"start": v(-1021.89, -3.68) * mm, "end": v(-1021.89, -0.5) * mm, "construction": true});
            skLineSegment(sketch, "E687.MirrorCS", {"start": v(-1047.29, 0.13) * mm, "end": v(-1051.14, -2.09) * mm, "construction": true});
            skLineSegment(sketch, "E688.MirrorCS", {"start": v(-992.64, -2.09) * mm, "end": v(-996.49, 0.13) * mm});
            skLineSegment(sketch, "E689.MirrorCS", {"start": v(-994.03, 3.12) * mm, "end": v(-991.29, 1.53) * mm});
            skLineSegment(sketch, "E690.MirrorCS", {"start": v(-1060.11, 14.73) * mm, "end": v(-1057.36, 16.31) * mm});
            skLineSegment(sketch, "E691.MirrorCS", {"start": v(-1015.54, -3.68) * mm, "end": v(-1015.54, -0.5) * mm});
            skLineSegment(sketch, "E692.MirrorCS", {"start": v(-996.49, -4.31) * mm, "end": v(-996.49, 0.13) * mm});
            skLineSegment(sketch, "E693.MirrorCS", {"start": v(-1030.78, -3.68) * mm, "end": v(-1030.78, -0.5) * mm});
            skLineSegment(sketch, "E694.MirrorCS", {"start": v(-984.94, 12.53) * mm, "end": v(-987.68, 14.11) * mm});
            skLineSegment(sketch, "E695.MirrorCS", {"start": v(-1028.24, -3.68) * mm, "end": v(-1028.24, -0.5) * mm});
            skLineSegment(sketch, "E696.MirrorCS", {"start": v(-1049.74, 3.12) * mm, "end": v(-1052.5, 1.53) * mm});
            skLineSegment(sketch, "E697.MirrorCS", {"start": v(-1071.33, 40.51) * mm, "end": v(-1074.08, 38.92) * mm});
            skLineSegment(sketch, "E698.MirrorCS", {"start": v(-1066.46, 25.72) * mm, "end": v(-1063.71, 27.31) * mm});
            skLineSegment(sketch, "E699.MirrorCS", {"start": v(-1076.54, 41.9) * mm, "end": v(-1072.69, 44.13) * mm});
            skLineSegment(sketch, "E700.MirrorCS", {"start": v(-983.67, 14.73) * mm, "end": v(-986.41, 16.31) * mm});
            skLineSegment(sketch, "E701.MirrorCS", {"start": v(-1013, -3.68) * mm, "end": v(-1013, -0.5) * mm});
            skLineSegment(sketch, "E702.MirrorCS", {"start": v(-1067.73, 27.92) * mm, "end": v(-1064.98, 29.51) * mm});
            skLineSegment(sketch, "E703.MirrorCS", {"start": v(-972.44, 40.51) * mm, "end": v(-969.7, 38.92) * mm});
            skLineSegment(sketch, "E704.MirrorCS", {"start": v(-1043.48, -0.5) * mm, "end": v(-1043.48, -3.68) * mm});
            skLineSegment(sketch, "E705.MirrorCS", {"start": v(-976.05, 27.92) * mm, "end": v(-978.8, 29.51) * mm});
            skLineSegment(sketch, "E706.MirrorCS", {"start": v(-971.09, 44.13) * mm, "end": v(-967.24, 41.9) * mm});
            skLineSegment(sketch, "E707.MirrorCS", {"start": v(-977.32, 25.72) * mm, "end": v(-980.06, 27.31) * mm});
            skLineSegment(sketch, "E708.MirrorCS", {"start": v(-1058.84, 12.53) * mm, "end": v(-1056.1, 14.11) * mm});
            skLineSegment(sketch, "E709.MirrorCS", {"start": v(-1000.3, -0.5) * mm, "end": v(-1000.3, -3.68) * mm});
            skLineSegment(sketch, "E710.MirrorCS", {"start": v(-986.41, 16.31) * mm, "end": v(-983.24, 21.81) * mm});
            skLineSegment(sketch, "E711.MirrorCS", {"start": v(-1028.24, -0.5) * mm, "end": v(-1021.89, -0.5) * mm});
            skLineSegment(sketch, "E712.MirrorCS", {"start": v(-1063.71, 27.31) * mm, "end": v(-1060.54, 21.81) * mm});
            skLineSegment(sketch, "E713.MirrorCS", {"start": v(-980.5, 20.23) * mm, "end": v(-977.32, 25.72) * mm});
            skLineSegment(sketch, "E714.MirrorCS", {"start": v(-1047.29, -4.31) * mm, "end": v(-1047.29, 0.13) * mm});
            skLineSegment(sketch, "E715.MirrorCS", {"start": v(-1021.89, -3.68) * mm, "end": v(-1015.54, -3.68) * mm});
            skLineSegment(sketch, "E716.MirrorCS", {"start": v(-983.24, 21.81) * mm, "end": v(-980.06, 27.31) * mm});
            skPoint(sketch, "E717.MirrorP", {"position": v(-1021.89, -2.09) * mm});
            skLineSegment(sketch, "E718.MirrorCS", {"start": v(-1021.89, -0.5) * mm, "end": v(-1015.54, -0.5) * mm});
            skLineSegment(sketch, "E719.MirrorCS", {"start": v(-983.67, 14.73) * mm, "end": v(-980.5, 20.23) * mm});
            skLineSegment(sketch, "E720.MirrorCS", {"start": v(-1060.54, 21.81) * mm, "end": v(-1057.36, 16.31) * mm});
            skLineSegment(sketch, "E721.MirrorCS", {"start": v(-1028.24, -3.68) * mm, "end": v(-1021.89, -3.68) * mm});
            skLineSegment(sketch, "E722.MirrorCS", {"start": v(-978.8, 29.51) * mm, "end": v(-972.44, 40.51) * mm});
            skLineSegment(sketch, "E723.MirrorCS", {"start": v(-1076.54, 41.9) * mm, "end": v(-1051.14, -2.09) * mm});
            skLineSegment(sketch, "E724.MirrorCS", {"start": v(-1013, -3.68) * mm, "end": v(-1000.3, -3.68) * mm});
            skLineSegment(sketch, "E725.MirrorCS", {"start": v(-996.49, 0.13) * mm, "end": v(-971.09, 44.13) * mm});
            skLineSegment(sketch, "E726.MirrorCS", {"start": v(-991.29, 1.53) * mm, "end": v(-984.94, 12.53) * mm});
            skLineSegment(sketch, "E727.MirrorCS", {"start": v(-1071.33, 40.51) * mm, "end": v(-1064.98, 29.51) * mm});
            skLineSegment(sketch, "E728.MirrorCS", {"start": v(-1056.1, 14.11) * mm, "end": v(-1049.74, 3.12) * mm});
            skLineSegment(sketch, "E729.MirrorCS", {"start": v(-1013, -0.5) * mm, "end": v(-1000.3, -0.5) * mm});
            skPoint(sketch, "E730.MirrorP", {"position": v(-981.87, 21.02) * mm});
            skLineSegment(sketch, "E731.MirrorCS", {"start": v(-976.05, 27.92) * mm, "end": v(-969.7, 38.92) * mm});
            skLineSegment(sketch, "E732.MirrorCS", {"start": v(-1047.29, 0.13) * mm, "end": v(-996.49, 0.13) * mm});
            skPoint(sketch, "E733.MirrorP", {"position": v(-996.49, -2.09) * mm});
            skPoint(sketch, "E734.MirrorP", {"position": v(-1049.21, -0.98) * mm});
            skLineSegment(sketch, "E735.MirrorCS", {"start": v(-1066.46, 25.72) * mm, "end": v(-1063.29, 20.23) * mm});
            skLineSegment(sketch, "E736.MirrorCS", {"start": v(-1047.29, -4.31) * mm, "end": v(-996.49, -4.31) * mm});
            skLineSegment(sketch, "E737.MirrorCS", {"start": v(-1043.48, -0.5) * mm, "end": v(-1030.78, -0.5) * mm});
            skPoint(sketch, "E738.MirrorP", {"position": v(-1061.91, 21.02) * mm});
            skLineSegment(sketch, "E739.MirrorCS", {"start": v(-1047.29, -2.09) * mm, "end": v(-996.49, -2.09) * mm, "construction": true});
            skLineSegment(sketch, "E740.MirrorCS", {"start": v(-994.03, 3.12) * mm, "end": v(-987.68, 14.11) * mm});
            skLineSegment(sketch, "E741.MirrorCS", {"start": v(-992.64, -2.09) * mm, "end": v(-967.24, 41.9) * mm});
            skLineSegment(sketch, "E742.MirrorCS", {"start": v(-1043.48, -3.68) * mm, "end": v(-1030.78, -3.68) * mm});
            skLineSegment(sketch, "E743.MirrorCS", {"start": v(-1072.69, 44.13) * mm, "end": v(-1047.29, 0.13) * mm});
            skLineSegment(sketch, "E744.MirrorCS", {"start": v(-1058.84, 12.53) * mm, "end": v(-1052.5, 1.53) * mm});
            skLineSegment(sketch, "E745.MirrorCS", {"start": v(-1074.08, 38.92) * mm, "end": v(-1067.73, 27.92) * mm});
            skLineSegment(sketch, "E746.MirrorCS", {"start": v(-1063.29, 20.23) * mm, "end": v(-1060.11, 14.73) * mm});
            skPoint(sketch, "E747.MirrorP", {"position": v(-969.17, 43.02) * mm});
            skLineSegment(sketch, "E748", {"start": v(-1047.29, 180.55) * mm, "end": v(-996.49, 180.55) * mm});
            skLineSegment(sketch, "E749", {"start": v(-1047.29, 185) * mm, "end": v(-1047.29, 180.55) * mm});
            skLineSegment(sketch, "E750", {"start": v(-996.49, 185) * mm, "end": v(-996.49, 180.55) * mm});
            skLineSegment(sketch, "E751", {"start": v(-1072.69, 136.56) * mm, "end": v(-971.09, 136.56) * mm, "construction": true});
            skPoint(sketch, "E752.endSnap0", {"position": v(-996.49, 182.78) * mm});
            skLineSegment(sketch, "E753", {"start": v(-1047.29, 182.78) * mm, "end": v(-996.49, 182.78) * mm, "construction": true});
            skLineSegment(sketch, "E754", {"start": v(-1047.29, 185) * mm, "end": v(-996.49, 185) * mm});
            skLineSegment(sketch, "E755", {"start": v(-1076.54, 138.78) * mm, "end": v(-1072.69, 136.56) * mm});
            skLineSegment(sketch, "E756.left", {"start": v(-1000.3, 181.19) * mm, "end": v(-1000.3, 184.36) * mm});
            skLineSegment(sketch, "E756.right", {"start": v(-1043.48, 181.19) * mm, "end": v(-1043.48, 184.36) * mm});
            skPoint(sketch, "E756.middle", {"position": v(-1021.89, 182.78) * mm});
            skLineSegment(sketch, "E757", {"start": v(-1021.89, 184.36) * mm, "end": v(-1021.89, 181.19) * mm, "construction": true});
            skLineSegment(sketch, "E758", {"start": v(-1030.78, 184.36) * mm, "end": v(-1030.78, 181.19) * mm});
            skLineSegment(sketch, "E759.MirrorCS", {"start": v(-1013, 184.36) * mm, "end": v(-1013, 181.19) * mm});
            skLineSegment(sketch, "E760", {"start": v(-1028.24, 184.36) * mm, "end": v(-1028.24, 181.19) * mm});
            skLineSegment(sketch, "E761.MirrorCS", {"start": v(-1015.54, 184.36) * mm, "end": v(-1015.54, 181.19) * mm});
            skLineSegment(sketch, "E762", {"start": v(-1043.48, 184.36) * mm, "end": v(-1030.78, 184.36) * mm});
            skLineSegment(sketch, "E763", {"start": v(-1043.48, 181.19) * mm, "end": v(-1030.78, 181.19) * mm});
            skLineSegment(sketch, "E764", {"start": v(-1028.24, 181.19) * mm, "end": v(-1021.89, 181.19) * mm});
            skLineSegment(sketch, "E765", {"start": v(-1028.24, 184.36) * mm, "end": v(-1021.89, 184.36) * mm});
            skLineSegment(sketch, "E766", {"start": v(-1021.89, 184.36) * mm, "end": v(-1015.54, 184.36) * mm});
            skLineSegment(sketch, "E767", {"start": v(-1021.89, 181.19) * mm, "end": v(-1015.54, 181.19) * mm});
            skLineSegment(sketch, "E768", {"start": v(-1013, 184.36) * mm, "end": v(-1000.3, 184.36) * mm});
            skLineSegment(sketch, "E769", {"start": v(-1013, 181.19) * mm, "end": v(-1000.3, 181.19) * mm});
            skLineSegment(sketch, "E770", {"start": v(-996.49, 180.55) * mm, "end": v(-971.09, 136.56) * mm});
            skLineSegment(sketch, "E771", {"start": v(-992.64, 182.78) * mm, "end": v(-996.49, 180.55) * mm});
            skPoint(sketch, "E772.endSnap0", {"position": v(-969.17, 137.67) * mm});
            skLineSegment(sketch, "E773", {"start": v(-992.64, 182.78) * mm, "end": v(-967.24, 138.78) * mm});
            skLineSegment(sketch, "E774.left", {"start": v(-972.44, 140.18) * mm, "end": v(-969.7, 141.76) * mm});
            skLineSegment(sketch, "E774.right", {"start": v(-994.03, 177.57) * mm, "end": v(-991.29, 179.16) * mm});
            skPoint(sketch, "E774.middle", {"position": v(-981.87, 159.67) * mm});
            skLineSegment(sketch, "E775", {"start": v(-980.5, 160.46) * mm, "end": v(-983.24, 158.87) * mm, "construction": true});
            skLineSegment(sketch, "E776", {"start": v(-984.94, 168.16) * mm, "end": v(-987.68, 166.57) * mm});
            skLineSegment(sketch, "E777.MirrorCS", {"start": v(-976.05, 152.76) * mm, "end": v(-978.8, 151.18) * mm});
            skLineSegment(sketch, "E778", {"start": v(-983.67, 165.96) * mm, "end": v(-986.41, 164.37) * mm});
            skLineSegment(sketch, "E779.MirrorCS", {"start": v(-977.32, 154.96) * mm, "end": v(-980.06, 153.38) * mm});
            skLineSegment(sketch, "E780", {"start": v(-991.29, 179.16) * mm, "end": v(-984.94, 168.16) * mm});
            skLineSegment(sketch, "E781", {"start": v(-994.03, 177.57) * mm, "end": v(-987.68, 166.57) * mm});
            skLineSegment(sketch, "E782", {"start": v(-986.41, 164.37) * mm, "end": v(-983.24, 158.87) * mm});
            skLineSegment(sketch, "E783", {"start": v(-983.67, 165.96) * mm, "end": v(-980.5, 160.46) * mm});
            skLineSegment(sketch, "E784", {"start": v(-980.5, 160.46) * mm, "end": v(-977.32, 154.96) * mm});
            skLineSegment(sketch, "E785", {"start": v(-983.24, 158.87) * mm, "end": v(-980.06, 153.38) * mm});
            skLineSegment(sketch, "E786", {"start": v(-976.05, 152.76) * mm, "end": v(-969.7, 141.76) * mm});
            skLineSegment(sketch, "E787", {"start": v(-978.8, 151.18) * mm, "end": v(-972.44, 140.18) * mm});
            skLineSegment(sketch, "E788.left", {"start": v(-1049.74, 177.57) * mm, "end": v(-1052.5, 179.16) * mm});
            skLineSegment(sketch, "E788.right", {"start": v(-1071.33, 140.18) * mm, "end": v(-1074.08, 141.76) * mm});
            skLineSegment(sketch, "E789", {"start": v(-1063.29, 160.46) * mm, "end": v(-1060.54, 158.87) * mm, "construction": true});
            skLineSegment(sketch, "E790", {"start": v(-1067.73, 152.76) * mm, "end": v(-1064.98, 151.18) * mm});
            skLineSegment(sketch, "E791.MirrorCS", {"start": v(-1058.84, 168.16) * mm, "end": v(-1056.1, 166.57) * mm});
            skLineSegment(sketch, "E792", {"start": v(-1066.46, 154.96) * mm, "end": v(-1063.71, 153.38) * mm});
            skLineSegment(sketch, "E793.MirrorCS", {"start": v(-1060.11, 165.96) * mm, "end": v(-1057.36, 164.37) * mm});
            skLineSegment(sketch, "E794.0", {"start": v(-1047.29, 180.55) * mm, "end": v(-1051.14, 182.78) * mm, "construction": true});
            skLineSegment(sketch, "E795", {"start": v(-971.09, 136.56) * mm, "end": v(-967.24, 138.78) * mm});
            skLineSegment(sketch, "E796.MirrorCS", {"start": v(-980.5, 112.66) * mm, "end": v(-983.24, 114.25) * mm, "construction": true});
            skLineSegment(sketch, "E797.MirrorCS", {"start": v(-1063.29, 112.66) * mm, "end": v(-1060.54, 114.25) * mm, "construction": true});
            skLineSegment(sketch, "E798.MirrorCS", {"start": v(-1021.89, 88.76) * mm, "end": v(-1021.89, 91.93) * mm, "construction": true});
            skLineSegment(sketch, "E799.MirrorCS", {"start": v(-1047.29, 92.57) * mm, "end": v(-1051.14, 90.34) * mm, "construction": true});
            skLineSegment(sketch, "E800.MirrorCS", {"start": v(-992.64, 90.34) * mm, "end": v(-996.49, 92.57) * mm});
            skLineSegment(sketch, "E801.MirrorCS", {"start": v(-994.03, 95.55) * mm, "end": v(-991.29, 93.96) * mm});
            skLineSegment(sketch, "E802.MirrorCS", {"start": v(-1060.11, 107.16) * mm, "end": v(-1057.36, 108.75) * mm});
            skLineSegment(sketch, "E803.MirrorCS", {"start": v(-1015.54, 88.76) * mm, "end": v(-1015.54, 91.93) * mm});
            skLineSegment(sketch, "E804.MirrorCS", {"start": v(-996.49, 88.12) * mm, "end": v(-996.49, 92.57) * mm});
            skLineSegment(sketch, "E805.MirrorCS", {"start": v(-1030.78, 88.76) * mm, "end": v(-1030.78, 91.93) * mm});
            skLineSegment(sketch, "E806.MirrorCS", {"start": v(-984.94, 104.96) * mm, "end": v(-987.68, 106.55) * mm});
            skLineSegment(sketch, "E807.MirrorCS", {"start": v(-1028.24, 88.76) * mm, "end": v(-1028.24, 91.93) * mm});
            skLineSegment(sketch, "E808.MirrorCS", {"start": v(-1049.74, 95.55) * mm, "end": v(-1052.5, 93.96) * mm});
            skLineSegment(sketch, "E809.MirrorCS", {"start": v(-1071.33, 132.94) * mm, "end": v(-1074.08, 131.36) * mm});
            skLineSegment(sketch, "E810.MirrorCS", {"start": v(-1066.46, 118.16) * mm, "end": v(-1063.71, 119.75) * mm});
            skLineSegment(sketch, "E811.MirrorCS", {"start": v(-1076.54, 134.34) * mm, "end": v(-1072.69, 136.56) * mm});
            skLineSegment(sketch, "E812.MirrorCS", {"start": v(-983.67, 107.16) * mm, "end": v(-986.41, 108.75) * mm});
            skLineSegment(sketch, "E813.MirrorCS", {"start": v(-1013, 88.76) * mm, "end": v(-1013, 91.93) * mm});
            skLineSegment(sketch, "E814.MirrorCS", {"start": v(-1067.73, 120.36) * mm, "end": v(-1064.98, 121.94) * mm});
            skLineSegment(sketch, "E815.MirrorCS", {"start": v(-972.44, 132.94) * mm, "end": v(-969.7, 131.36) * mm});
            skLineSegment(sketch, "E816.MirrorCS", {"start": v(-1043.48, 91.93) * mm, "end": v(-1043.48, 88.76) * mm});
            skLineSegment(sketch, "E817.MirrorCS", {"start": v(-976.05, 120.36) * mm, "end": v(-978.8, 121.94) * mm});
            skLineSegment(sketch, "E818.MirrorCS", {"start": v(-971.09, 136.56) * mm, "end": v(-967.24, 134.34) * mm});
            skLineSegment(sketch, "E819.MirrorCS", {"start": v(-977.32, 118.16) * mm, "end": v(-980.06, 119.75) * mm});
            skLineSegment(sketch, "E820.MirrorCS", {"start": v(-1058.84, 104.96) * mm, "end": v(-1056.1, 106.55) * mm});
            skLineSegment(sketch, "E821.MirrorCS", {"start": v(-1000.3, 91.93) * mm, "end": v(-1000.3, 88.76) * mm});
            skLineSegment(sketch, "E822.MirrorCS", {"start": v(-986.41, 108.75) * mm, "end": v(-983.24, 114.25) * mm});
            skLineSegment(sketch, "E823.MirrorCS", {"start": v(-980.5, 112.66) * mm, "end": v(-977.32, 118.16) * mm});
            skLineSegment(sketch, "E824.MirrorCS", {"start": v(-1047.29, 88.12) * mm, "end": v(-1047.29, 92.57) * mm});
            skLineSegment(sketch, "E825.MirrorCS", {"start": v(-983.24, 114.25) * mm, "end": v(-980.06, 119.75) * mm});
            skLineSegment(sketch, "E826.MirrorCS", {"start": v(-983.67, 107.16) * mm, "end": v(-980.5, 112.66) * mm});
            skLineSegment(sketch, "E827.MirrorCS", {"start": v(-978.8, 121.94) * mm, "end": v(-972.44, 132.94) * mm});
            skLineSegment(sketch, "E828.MirrorCS", {"start": v(-996.49, 92.57) * mm, "end": v(-971.09, 136.56) * mm});
            skLineSegment(sketch, "E829.MirrorCS", {"start": v(-991.29, 93.96) * mm, "end": v(-984.94, 104.96) * mm});
            skPoint(sketch, "E830.MirrorP", {"position": v(-981.87, 113.45) * mm});
            skLineSegment(sketch, "E831.MirrorCS", {"start": v(-976.05, 120.36) * mm, "end": v(-969.7, 131.36) * mm});
            skLineSegment(sketch, "E832.MirrorCS", {"start": v(-994.03, 95.55) * mm, "end": v(-987.68, 106.55) * mm});
            skLineSegment(sketch, "E833.MirrorCS", {"start": v(-992.64, 90.34) * mm, "end": v(-967.24, 134.34) * mm});
            skPoint(sketch, "E834.MirrorP", {"position": v(-969.17, 135.45) * mm});
            skLineSegment(sketch, "E835", {"start": v(-1047.29, 272.99) * mm, "end": v(-996.49, 272.99) * mm});
            skLineSegment(sketch, "E836", {"start": v(-1047.29, 277.43) * mm, "end": v(-1047.29, 272.99) * mm});
            skLineSegment(sketch, "E837", {"start": v(-996.49, 277.43) * mm, "end": v(-996.49, 272.99) * mm});
            skLineSegment(sketch, "E838", {"start": v(-1072.69, 229) * mm, "end": v(-971.09, 229) * mm, "construction": true});
            skPoint(sketch, "E839.endSnap0", {"position": v(-996.49, 275.21) * mm});
            skLineSegment(sketch, "E840", {"start": v(-1047.29, 275.21) * mm, "end": v(-996.49, 275.21) * mm, "construction": true});
            skLineSegment(sketch, "E841", {"start": v(-1047.29, 277.43) * mm, "end": v(-996.49, 277.43) * mm});
            skLineSegment(sketch, "E842", {"start": v(-1076.54, 231.22) * mm, "end": v(-1072.69, 229) * mm});
            skLineSegment(sketch, "E843.left", {"start": v(-1000.3, 273.62) * mm, "end": v(-1000.3, 276.8) * mm});
            skLineSegment(sketch, "E843.right", {"start": v(-1043.48, 273.62) * mm, "end": v(-1043.48, 276.8) * mm});
            skPoint(sketch, "E843.middle", {"position": v(-1021.89, 275.21) * mm});
            skLineSegment(sketch, "E844", {"start": v(-1021.89, 276.8) * mm, "end": v(-1021.89, 273.62) * mm, "construction": true});
            skLineSegment(sketch, "E845", {"start": v(-1030.78, 276.8) * mm, "end": v(-1030.78, 273.62) * mm});
            skLineSegment(sketch, "E846.MirrorCS", {"start": v(-1013, 276.8) * mm, "end": v(-1013, 273.62) * mm});
            skLineSegment(sketch, "E847", {"start": v(-1028.24, 276.8) * mm, "end": v(-1028.24, 273.62) * mm});
            skLineSegment(sketch, "E848.MirrorCS", {"start": v(-1015.54, 276.8) * mm, "end": v(-1015.54, 273.62) * mm});
            skLineSegment(sketch, "E849", {"start": v(-1043.48, 276.8) * mm, "end": v(-1030.78, 276.8) * mm});
            skLineSegment(sketch, "E850", {"start": v(-1043.48, 273.62) * mm, "end": v(-1030.78, 273.62) * mm});
            skLineSegment(sketch, "E851", {"start": v(-1028.24, 273.62) * mm, "end": v(-1021.89, 273.62) * mm});
            skLineSegment(sketch, "E852", {"start": v(-1028.24, 276.8) * mm, "end": v(-1021.89, 276.8) * mm});
            skLineSegment(sketch, "E853", {"start": v(-1021.89, 276.8) * mm, "end": v(-1015.54, 276.8) * mm});
            skLineSegment(sketch, "E854", {"start": v(-1021.89, 273.62) * mm, "end": v(-1015.54, 273.62) * mm});
            skLineSegment(sketch, "E855", {"start": v(-1013, 276.8) * mm, "end": v(-1000.3, 276.8) * mm});
            skLineSegment(sketch, "E856", {"start": v(-1013, 273.62) * mm, "end": v(-1000.3, 273.62) * mm});
            skLineSegment(sketch, "E857", {"start": v(-996.49, 272.99) * mm, "end": v(-971.09, 229) * mm});
            skLineSegment(sketch, "E858", {"start": v(-992.64, 275.21) * mm, "end": v(-996.49, 272.99) * mm});
            skPoint(sketch, "E859.endSnap0", {"position": v(-969.17, 230.1) * mm});
            skLineSegment(sketch, "E860", {"start": v(-992.64, 275.21) * mm, "end": v(-967.24, 231.22) * mm});
            skLineSegment(sketch, "E861.left", {"start": v(-972.44, 232.61) * mm, "end": v(-969.7, 234.2) * mm});
            skLineSegment(sketch, "E861.right", {"start": v(-994.03, 270) * mm, "end": v(-991.29, 271.6) * mm});
            skPoint(sketch, "E861.middle", {"position": v(-981.87, 252.1) * mm});
            skLineSegment(sketch, "E862", {"start": v(-980.5, 252.9) * mm, "end": v(-983.24, 251.3) * mm, "construction": true});
            skLineSegment(sketch, "E863", {"start": v(-984.94, 260.6) * mm, "end": v(-987.68, 259) * mm});
            skLineSegment(sketch, "E864.MirrorCS", {"start": v(-976.05, 245.2) * mm, "end": v(-978.8, 243.6) * mm});
            skLineSegment(sketch, "E865", {"start": v(-983.67, 258.4) * mm, "end": v(-986.41, 256.8) * mm});
            skLineSegment(sketch, "E866.MirrorCS", {"start": v(-977.32, 247.4) * mm, "end": v(-980.06, 245.8) * mm});
            skLineSegment(sketch, "E867", {"start": v(-991.29, 271.6) * mm, "end": v(-984.94, 260.6) * mm});
            skLineSegment(sketch, "E868", {"start": v(-994.03, 270) * mm, "end": v(-987.68, 259) * mm});
            skLineSegment(sketch, "E869", {"start": v(-986.41, 256.8) * mm, "end": v(-983.24, 251.3) * mm});
            skLineSegment(sketch, "E870", {"start": v(-983.67, 258.4) * mm, "end": v(-980.5, 252.9) * mm});
            skLineSegment(sketch, "E871", {"start": v(-980.5, 252.9) * mm, "end": v(-977.32, 247.4) * mm});
            skLineSegment(sketch, "E872", {"start": v(-983.24, 251.3) * mm, "end": v(-980.06, 245.8) * mm});
            skLineSegment(sketch, "E873", {"start": v(-976.05, 245.2) * mm, "end": v(-969.7, 234.2) * mm});
            skLineSegment(sketch, "E874", {"start": v(-978.8, 243.6) * mm, "end": v(-972.44, 232.61) * mm});
            skLineSegment(sketch, "E875.left", {"start": v(-1049.74, 270) * mm, "end": v(-1052.5, 271.6) * mm});
            skLineSegment(sketch, "E875.right", {"start": v(-1071.33, 232.61) * mm, "end": v(-1074.08, 234.2) * mm});
            skLineSegment(sketch, "E876", {"start": v(-1063.29, 252.9) * mm, "end": v(-1060.54, 251.3) * mm, "construction": true});
            skLineSegment(sketch, "E877", {"start": v(-1067.73, 245.2) * mm, "end": v(-1064.98, 243.6) * mm});
            skLineSegment(sketch, "E878.MirrorCS", {"start": v(-1058.84, 260.6) * mm, "end": v(-1056.1, 259) * mm});
            skLineSegment(sketch, "E879", {"start": v(-1066.46, 247.4) * mm, "end": v(-1063.71, 245.8) * mm});
            skLineSegment(sketch, "E880.MirrorCS", {"start": v(-1060.11, 258.4) * mm, "end": v(-1057.36, 256.8) * mm});
            skLineSegment(sketch, "E881.0", {"start": v(-1047.29, 272.99) * mm, "end": v(-1051.14, 275.21) * mm, "construction": true});
            skLineSegment(sketch, "E882", {"start": v(-971.09, 229) * mm, "end": v(-967.24, 231.22) * mm});
            skLineSegment(sketch, "E883.MirrorCS", {"start": v(-980.5, 205.1) * mm, "end": v(-983.24, 206.68) * mm, "construction": true});
            skLineSegment(sketch, "E884.MirrorCS", {"start": v(-1063.29, 205.1) * mm, "end": v(-1060.54, 206.68) * mm, "construction": true});
            skLineSegment(sketch, "E885.MirrorCS", {"start": v(-1021.89, 181.19) * mm, "end": v(-1021.89, 184.36) * mm, "construction": true});
            skLineSegment(sketch, "E886.MirrorCS", {"start": v(-1047.29, 185) * mm, "end": v(-1051.14, 182.78) * mm, "construction": true});
            skLineSegment(sketch, "E887.MirrorCS", {"start": v(-992.64, 182.78) * mm, "end": v(-996.49, 185) * mm});
            skLineSegment(sketch, "E888.MirrorCS", {"start": v(-994.03, 187.98) * mm, "end": v(-991.29, 186.4) * mm});
            skLineSegment(sketch, "E889.MirrorCS", {"start": v(-1060.11, 199.6) * mm, "end": v(-1057.36, 201.18) * mm});
            skLineSegment(sketch, "E890.MirrorCS", {"start": v(-1015.54, 181.19) * mm, "end": v(-1015.54, 184.36) * mm});
            skLineSegment(sketch, "E891.MirrorCS", {"start": v(-996.49, 180.55) * mm, "end": v(-996.49, 185) * mm});
            skLineSegment(sketch, "E892.MirrorCS", {"start": v(-1030.78, 181.19) * mm, "end": v(-1030.78, 184.36) * mm});
            skLineSegment(sketch, "E893.MirrorCS", {"start": v(-984.94, 197.4) * mm, "end": v(-987.68, 198.98) * mm});
            skLineSegment(sketch, "E894.MirrorCS", {"start": v(-1028.24, 181.19) * mm, "end": v(-1028.24, 184.36) * mm});
            skLineSegment(sketch, "E895.MirrorCS", {"start": v(-1049.74, 187.98) * mm, "end": v(-1052.5, 186.4) * mm});
            skLineSegment(sketch, "E896.MirrorCS", {"start": v(-1071.33, 225.38) * mm, "end": v(-1074.08, 223.79) * mm});
            skLineSegment(sketch, "E897.MirrorCS", {"start": v(-1066.46, 210.6) * mm, "end": v(-1063.71, 212.18) * mm});
            skLineSegment(sketch, "E898.MirrorCS", {"start": v(-1076.54, 226.77) * mm, "end": v(-1072.69, 229) * mm});
            skLineSegment(sketch, "E899.MirrorCS", {"start": v(-983.67, 199.6) * mm, "end": v(-986.41, 201.18) * mm});
            skLineSegment(sketch, "E900.MirrorCS", {"start": v(-1013, 181.19) * mm, "end": v(-1013, 184.36) * mm});
            skLineSegment(sketch, "E901.MirrorCS", {"start": v(-1067.73, 212.8) * mm, "end": v(-1064.98, 214.38) * mm});
            skLineSegment(sketch, "E902.MirrorCS", {"start": v(-972.44, 225.38) * mm, "end": v(-969.7, 223.79) * mm});
            skLineSegment(sketch, "E903.MirrorCS", {"start": v(-1043.48, 184.36) * mm, "end": v(-1043.48, 181.19) * mm});
            skLineSegment(sketch, "E904.MirrorCS", {"start": v(-976.05, 212.8) * mm, "end": v(-978.8, 214.38) * mm});
            skLineSegment(sketch, "E905.MirrorCS", {"start": v(-971.09, 229) * mm, "end": v(-967.24, 226.77) * mm});
            skLineSegment(sketch, "E906.MirrorCS", {"start": v(-977.32, 210.6) * mm, "end": v(-980.06, 212.18) * mm});
            skLineSegment(sketch, "E907.MirrorCS", {"start": v(-1058.84, 197.4) * mm, "end": v(-1056.1, 198.98) * mm});
            skLineSegment(sketch, "E908.MirrorCS", {"start": v(-1000.3, 184.36) * mm, "end": v(-1000.3, 181.19) * mm});
            skLineSegment(sketch, "E909.MirrorCS", {"start": v(-986.41, 201.18) * mm, "end": v(-983.24, 206.68) * mm});
            skLineSegment(sketch, "E910.MirrorCS", {"start": v(-980.5, 205.1) * mm, "end": v(-977.32, 210.6) * mm});
            skLineSegment(sketch, "E911.MirrorCS", {"start": v(-1047.29, 180.55) * mm, "end": v(-1047.29, 185) * mm});
            skLineSegment(sketch, "E912.MirrorCS", {"start": v(-983.24, 206.68) * mm, "end": v(-980.06, 212.18) * mm});
            skLineSegment(sketch, "E913.MirrorCS", {"start": v(-983.67, 199.6) * mm, "end": v(-980.5, 205.1) * mm});
            skLineSegment(sketch, "E914.MirrorCS", {"start": v(-978.8, 214.38) * mm, "end": v(-972.44, 225.38) * mm});
            skLineSegment(sketch, "E915.MirrorCS", {"start": v(-996.49, 185) * mm, "end": v(-971.09, 229) * mm});
            skLineSegment(sketch, "E916.MirrorCS", {"start": v(-991.29, 186.4) * mm, "end": v(-984.94, 197.4) * mm});
            skPoint(sketch, "E917.MirrorP", {"position": v(-981.87, 205.89) * mm});
            skLineSegment(sketch, "E918.MirrorCS", {"start": v(-976.05, 212.8) * mm, "end": v(-969.7, 223.79) * mm});
            skLineSegment(sketch, "E919.MirrorCS", {"start": v(-994.03, 187.98) * mm, "end": v(-987.68, 198.98) * mm});
            skLineSegment(sketch, "E920.MirrorCS", {"start": v(-992.64, 182.78) * mm, "end": v(-967.24, 226.77) * mm});
            skPoint(sketch, "E921.MirrorP", {"position": v(-969.17, 227.88) * mm});
            skLineSegment(sketch, "E922", {"start": v(-967.24, 134.34) * mm, "end": v(-916.44, 134.34) * mm});
            skLineSegment(sketch, "E923", {"start": v(-967.24, 138.78) * mm, "end": v(-967.24, 134.34) * mm});
            skLineSegment(sketch, "E924", {"start": v(-916.44, 138.78) * mm, "end": v(-916.44, 134.34) * mm});
            skLineSegment(sketch, "E925", {"start": v(-992.64, 90.34) * mm, "end": v(-891.04, 90.34) * mm, "construction": true});
            skPoint(sketch, "E926.endSnap0", {"position": v(-916.44, 136.56) * mm});
            skLineSegment(sketch, "E927", {"start": v(-967.24, 136.56) * mm, "end": v(-916.44, 136.56) * mm, "construction": true});
            skLineSegment(sketch, "E928", {"start": v(-967.24, 138.78) * mm, "end": v(-916.44, 138.78) * mm});
            skLineSegment(sketch, "E929", {"start": v(-996.49, 92.57) * mm, "end": v(-992.64, 90.34) * mm});
            skLineSegment(sketch, "E930.left", {"start": v(-920.25, 134.97) * mm, "end": v(-920.25, 138.15) * mm});
            skLineSegment(sketch, "E930.right", {"start": v(-963.43, 134.97) * mm, "end": v(-963.43, 138.15) * mm});
            skPoint(sketch, "E930.middle", {"position": v(-941.84, 136.56) * mm});
            skLineSegment(sketch, "E931", {"start": v(-941.84, 138.15) * mm, "end": v(-941.84, 134.97) * mm, "construction": true});
            skLineSegment(sketch, "E932", {"start": v(-950.73, 138.15) * mm, "end": v(-950.73, 134.97) * mm});
            skLineSegment(sketch, "E933.MirrorCS", {"start": v(-932.95, 138.15) * mm, "end": v(-932.95, 134.97) * mm});
            skLineSegment(sketch, "E934", {"start": v(-948.2, 138.15) * mm, "end": v(-948.2, 134.97) * mm});
            skLineSegment(sketch, "E935.MirrorCS", {"start": v(-935.5, 138.15) * mm, "end": v(-935.5, 134.97) * mm});
            skLineSegment(sketch, "E936", {"start": v(-963.43, 138.15) * mm, "end": v(-950.73, 138.15) * mm});
            skLineSegment(sketch, "E937", {"start": v(-963.43, 134.97) * mm, "end": v(-950.73, 134.97) * mm});
            skLineSegment(sketch, "E938", {"start": v(-948.2, 134.97) * mm, "end": v(-941.84, 134.97) * mm});
            skLineSegment(sketch, "E939", {"start": v(-948.2, 138.15) * mm, "end": v(-941.84, 138.15) * mm});
            skLineSegment(sketch, "E940", {"start": v(-941.84, 138.15) * mm, "end": v(-935.5, 138.15) * mm});
            skLineSegment(sketch, "E941", {"start": v(-941.84, 134.97) * mm, "end": v(-935.5, 134.97) * mm});
            skLineSegment(sketch, "E942", {"start": v(-932.95, 138.15) * mm, "end": v(-920.25, 138.15) * mm});
            skLineSegment(sketch, "E943", {"start": v(-932.95, 134.97) * mm, "end": v(-920.25, 134.97) * mm});
            skLineSegment(sketch, "E944", {"start": v(-916.44, 134.34) * mm, "end": v(-891.04, 90.34) * mm});
            skLineSegment(sketch, "E945", {"start": v(-912.6, 136.56) * mm, "end": v(-916.44, 134.34) * mm});
            skPoint(sketch, "E946.endSnap0", {"position": v(-889.12, 91.45) * mm});
            skLineSegment(sketch, "E947", {"start": v(-912.6, 136.56) * mm, "end": v(-887.2, 92.57) * mm});
            skLineSegment(sketch, "E948.left", {"start": v(-892.4, 93.96) * mm, "end": v(-889.65, 95.55) * mm});
            skLineSegment(sketch, "E948.right", {"start": v(-913.99, 131.36) * mm, "end": v(-911.24, 132.94) * mm});
            skPoint(sketch, "E948.middle", {"position": v(-901.82, 113.45) * mm});
            skLineSegment(sketch, "E949", {"start": v(-900.44, 114.25) * mm, "end": v(-903.2, 112.66) * mm, "construction": true});
            skLineSegment(sketch, "E950", {"start": v(-904.89, 121.94) * mm, "end": v(-907.64, 120.36) * mm});
            skLineSegment(sketch, "E951.MirrorCS", {"start": v(-896, 106.55) * mm, "end": v(-898.75, 104.96) * mm});
            skLineSegment(sketch, "E952", {"start": v(-903.62, 119.75) * mm, "end": v(-906.37, 118.16) * mm});
            skLineSegment(sketch, "E953.MirrorCS", {"start": v(-897.27, 108.75) * mm, "end": v(-900.02, 107.16) * mm});
            skLineSegment(sketch, "E954", {"start": v(-911.24, 132.94) * mm, "end": v(-904.89, 121.94) * mm});
            skLineSegment(sketch, "E955", {"start": v(-913.99, 131.36) * mm, "end": v(-907.64, 120.36) * mm});
            skLineSegment(sketch, "E956", {"start": v(-906.37, 118.16) * mm, "end": v(-903.2, 112.66) * mm});
            skLineSegment(sketch, "E957", {"start": v(-903.62, 119.75) * mm, "end": v(-900.44, 114.25) * mm});
            skLineSegment(sketch, "E958", {"start": v(-900.44, 114.25) * mm, "end": v(-897.27, 108.75) * mm});
            skLineSegment(sketch, "E959", {"start": v(-903.2, 112.66) * mm, "end": v(-900.02, 107.16) * mm});
            skLineSegment(sketch, "E960", {"start": v(-896, 106.55) * mm, "end": v(-889.65, 95.55) * mm});
            skLineSegment(sketch, "E961", {"start": v(-898.75, 104.96) * mm, "end": v(-892.4, 93.96) * mm});
            skLineSegment(sketch, "E962.left", {"start": v(-969.7, 131.36) * mm, "end": v(-972.44, 132.94) * mm});
            skLineSegment(sketch, "E962.right", {"start": v(-991.29, 93.96) * mm, "end": v(-994.03, 95.55) * mm});
            skLineSegment(sketch, "E963", {"start": v(-983.24, 114.25) * mm, "end": v(-980.5, 112.66) * mm, "construction": true});
            skLineSegment(sketch, "E964", {"start": v(-987.68, 106.55) * mm, "end": v(-984.94, 104.96) * mm});
            skLineSegment(sketch, "E965.MirrorCS", {"start": v(-978.8, 121.94) * mm, "end": v(-976.05, 120.36) * mm});
            skLineSegment(sketch, "E966", {"start": v(-986.41, 108.75) * mm, "end": v(-983.67, 107.16) * mm});
            skLineSegment(sketch, "E967.MirrorCS", {"start": v(-980.06, 119.75) * mm, "end": v(-977.32, 118.16) * mm});
            skLineSegment(sketch, "E968.0", {"start": v(-967.24, 134.34) * mm, "end": v(-971.09, 136.56) * mm, "construction": true});
            skLineSegment(sketch, "E969", {"start": v(-891.04, 90.34) * mm, "end": v(-887.2, 92.57) * mm});
            skLineSegment(sketch, "E970.MirrorCS", {"start": v(-900.44, 66.44) * mm, "end": v(-903.2, 68.03) * mm, "construction": true});
            skLineSegment(sketch, "E971.MirrorCS", {"start": v(-983.24, 66.44) * mm, "end": v(-980.5, 68.03) * mm, "construction": true});
            skLineSegment(sketch, "E972.MirrorCS", {"start": v(-941.84, 42.54) * mm, "end": v(-941.84, 45.71) * mm, "construction": true});
            skLineSegment(sketch, "E973.MirrorCS", {"start": v(-967.24, 46.35) * mm, "end": v(-971.09, 44.13) * mm, "construction": true});
            skLineSegment(sketch, "E974.MirrorCS", {"start": v(-912.6, 44.13) * mm, "end": v(-916.44, 46.35) * mm});
            skLineSegment(sketch, "E975.MirrorCS", {"start": v(-913.99, 49.33) * mm, "end": v(-911.24, 47.74) * mm});
            skLineSegment(sketch, "E976.MirrorCS", {"start": v(-980.06, 60.94) * mm, "end": v(-977.32, 62.53) * mm});
            skLineSegment(sketch, "E977.MirrorCS", {"start": v(-935.5, 42.54) * mm, "end": v(-935.5, 45.71) * mm});
            skLineSegment(sketch, "E978.MirrorCS", {"start": v(-916.44, 41.9) * mm, "end": v(-916.44, 46.35) * mm});
            skLineSegment(sketch, "E979.MirrorCS", {"start": v(-950.73, 42.54) * mm, "end": v(-950.73, 45.71) * mm});
            skLineSegment(sketch, "E980.MirrorCS", {"start": v(-904.89, 58.74) * mm, "end": v(-907.64, 60.33) * mm});
            skLineSegment(sketch, "E981.MirrorCS", {"start": v(-948.2, 42.54) * mm, "end": v(-948.2, 45.71) * mm});
            skLineSegment(sketch, "E982.MirrorCS", {"start": v(-969.7, 49.33) * mm, "end": v(-972.44, 47.74) * mm});
            skLineSegment(sketch, "E983.MirrorCS", {"start": v(-991.29, 86.73) * mm, "end": v(-994.03, 85.14) * mm});
            skLineSegment(sketch, "E984.MirrorCS", {"start": v(-986.41, 71.94) * mm, "end": v(-983.67, 73.53) * mm});
            skLineSegment(sketch, "E985.MirrorCS", {"start": v(-996.49, 88.12) * mm, "end": v(-992.64, 90.34) * mm});
            skLineSegment(sketch, "E986.MirrorCS", {"start": v(-903.62, 60.94) * mm, "end": v(-906.37, 62.53) * mm});
            skLineSegment(sketch, "E987.MirrorCS", {"start": v(-932.95, 42.54) * mm, "end": v(-932.95, 45.71) * mm});
            skLineSegment(sketch, "E988.MirrorCS", {"start": v(-987.68, 74.14) * mm, "end": v(-984.94, 75.73) * mm});
            skLineSegment(sketch, "E989.MirrorCS", {"start": v(-892.4, 86.73) * mm, "end": v(-889.65, 85.14) * mm});
            skLineSegment(sketch, "E990.MirrorCS", {"start": v(-963.43, 45.71) * mm, "end": v(-963.43, 42.54) * mm});
            skLineSegment(sketch, "E991.MirrorCS", {"start": v(-896, 74.14) * mm, "end": v(-898.75, 75.73) * mm});
            skLineSegment(sketch, "E992.MirrorCS", {"start": v(-891.04, 90.34) * mm, "end": v(-887.2, 88.12) * mm});
            skLineSegment(sketch, "E993.MirrorCS", {"start": v(-897.27, 71.94) * mm, "end": v(-900.02, 73.53) * mm});
            skLineSegment(sketch, "E994.MirrorCS", {"start": v(-978.8, 58.74) * mm, "end": v(-976.05, 60.33) * mm});
            skLineSegment(sketch, "E995.MirrorCS", {"start": v(-920.25, 45.71) * mm, "end": v(-920.25, 42.54) * mm});
            skLineSegment(sketch, "E996.MirrorCS", {"start": v(-906.37, 62.53) * mm, "end": v(-903.2, 68.03) * mm});
            skLineSegment(sketch, "E997.MirrorCS", {"start": v(-948.2, 45.71) * mm, "end": v(-941.84, 45.71) * mm});
            skLineSegment(sketch, "E998.MirrorCS", {"start": v(-900.44, 66.44) * mm, "end": v(-897.27, 71.94) * mm});
            skLineSegment(sketch, "E999.MirrorCS", {"start": v(-967.24, 41.9) * mm, "end": v(-967.24, 46.35) * mm});
            skLineSegment(sketch, "E1000.MirrorCS", {"start": v(-941.84, 42.54) * mm, "end": v(-935.5, 42.54) * mm});
            skLineSegment(sketch, "E1001.MirrorCS", {"start": v(-903.2, 68.03) * mm, "end": v(-900.02, 73.53) * mm});
            skPoint(sketch, "E1002.MirrorP", {"position": v(-941.84, 44.13) * mm});
            skLineSegment(sketch, "E1003.MirrorCS", {"start": v(-941.84, 45.71) * mm, "end": v(-935.5, 45.71) * mm});
            skLineSegment(sketch, "E1004.MirrorCS", {"start": v(-903.62, 60.94) * mm, "end": v(-900.44, 66.44) * mm});
            skLineSegment(sketch, "E1005.MirrorCS", {"start": v(-948.2, 42.54) * mm, "end": v(-941.84, 42.54) * mm});
            skLineSegment(sketch, "E1006.MirrorCS", {"start": v(-898.75, 75.73) * mm, "end": v(-892.4, 86.73) * mm});
            skLineSegment(sketch, "E1007.MirrorCS", {"start": v(-932.95, 42.54) * mm, "end": v(-920.25, 42.54) * mm});
            skLineSegment(sketch, "E1008.MirrorCS", {"start": v(-916.44, 46.35) * mm, "end": v(-891.04, 90.34) * mm});
            skLineSegment(sketch, "E1009.MirrorCS", {"start": v(-911.24, 47.74) * mm, "end": v(-904.89, 58.74) * mm});
            skLineSegment(sketch, "E1010.MirrorCS", {"start": v(-932.95, 45.71) * mm, "end": v(-920.25, 45.71) * mm});
            skPoint(sketch, "E1011.MirrorP", {"position": v(-901.82, 67.24) * mm});
            skLineSegment(sketch, "E1012.MirrorCS", {"start": v(-896, 74.14) * mm, "end": v(-889.65, 85.14) * mm});
            skLineSegment(sketch, "E1013.MirrorCS", {"start": v(-967.24, 46.35) * mm, "end": v(-916.44, 46.35) * mm});
            skPoint(sketch, "E1014.MirrorP", {"position": v(-916.44, 44.13) * mm});
            skLineSegment(sketch, "E1015.MirrorCS", {"start": v(-967.24, 41.9) * mm, "end": v(-916.44, 41.9) * mm});
            skLineSegment(sketch, "E1016.MirrorCS", {"start": v(-963.43, 45.71) * mm, "end": v(-950.73, 45.71) * mm});
            skLineSegment(sketch, "E1017.MirrorCS", {"start": v(-967.24, 44.13) * mm, "end": v(-916.44, 44.13) * mm, "construction": true});
            skLineSegment(sketch, "E1018.MirrorCS", {"start": v(-913.99, 49.33) * mm, "end": v(-907.64, 60.33) * mm});
            skLineSegment(sketch, "E1019.MirrorCS", {"start": v(-912.6, 44.13) * mm, "end": v(-887.2, 88.12) * mm});
            skLineSegment(sketch, "E1020.MirrorCS", {"start": v(-963.43, 42.54) * mm, "end": v(-950.73, 42.54) * mm});
            skPoint(sketch, "E1021.MirrorP", {"position": v(-889.12, 89.23) * mm});
            skLineSegment(sketch, "E1022", {"start": v(-967.24, 226.77) * mm, "end": v(-916.44, 226.77) * mm});
            skLineSegment(sketch, "E1023", {"start": v(-967.24, 231.22) * mm, "end": v(-967.24, 226.77) * mm});
            skLineSegment(sketch, "E1024", {"start": v(-916.44, 231.22) * mm, "end": v(-916.44, 226.77) * mm});
            skLineSegment(sketch, "E1025", {"start": v(-992.64, 182.78) * mm, "end": v(-891.04, 182.78) * mm, "construction": true});
            skPoint(sketch, "E1026.endSnap0", {"position": v(-916.44, 229) * mm});
            skLineSegment(sketch, "E1027", {"start": v(-967.24, 229) * mm, "end": v(-916.44, 229) * mm, "construction": true});
            skLineSegment(sketch, "E1028", {"start": v(-967.24, 231.22) * mm, "end": v(-916.44, 231.22) * mm});
            skLineSegment(sketch, "E1029", {"start": v(-996.49, 185) * mm, "end": v(-992.64, 182.78) * mm});
            skLineSegment(sketch, "E1030.left", {"start": v(-920.25, 227.4) * mm, "end": v(-920.25, 230.58) * mm});
            skLineSegment(sketch, "E1030.right", {"start": v(-963.43, 227.4) * mm, "end": v(-963.43, 230.58) * mm});
            skPoint(sketch, "E1030.middle", {"position": v(-941.84, 229) * mm});
            skLineSegment(sketch, "E1031", {"start": v(-941.84, 230.58) * mm, "end": v(-941.84, 227.4) * mm, "construction": true});
            skLineSegment(sketch, "E1032", {"start": v(-950.73, 230.58) * mm, "end": v(-950.73, 227.4) * mm});
            skLineSegment(sketch, "E1033.MirrorCS", {"start": v(-932.95, 230.58) * mm, "end": v(-932.95, 227.4) * mm});
            skLineSegment(sketch, "E1034", {"start": v(-948.2, 230.58) * mm, "end": v(-948.2, 227.4) * mm});
            skLineSegment(sketch, "E1035.MirrorCS", {"start": v(-935.5, 230.58) * mm, "end": v(-935.5, 227.4) * mm});
            skLineSegment(sketch, "E1036", {"start": v(-963.43, 230.58) * mm, "end": v(-950.73, 230.58) * mm});
            skLineSegment(sketch, "E1037", {"start": v(-963.43, 227.4) * mm, "end": v(-950.73, 227.4) * mm});
            skLineSegment(sketch, "E1038", {"start": v(-948.2, 227.4) * mm, "end": v(-941.84, 227.4) * mm});
            skLineSegment(sketch, "E1039", {"start": v(-948.2, 230.58) * mm, "end": v(-941.84, 230.58) * mm});
            skLineSegment(sketch, "E1040", {"start": v(-941.84, 230.58) * mm, "end": v(-935.5, 230.58) * mm});
            skLineSegment(sketch, "E1041", {"start": v(-941.84, 227.4) * mm, "end": v(-935.5, 227.4) * mm});
            skLineSegment(sketch, "E1042", {"start": v(-932.95, 230.58) * mm, "end": v(-920.25, 230.58) * mm});
            skLineSegment(sketch, "E1043", {"start": v(-932.95, 227.4) * mm, "end": v(-920.25, 227.4) * mm});
            skLineSegment(sketch, "E1044", {"start": v(-916.44, 226.77) * mm, "end": v(-891.04, 182.78) * mm});
            skLineSegment(sketch, "E1045", {"start": v(-912.6, 229) * mm, "end": v(-916.44, 226.77) * mm});
            skPoint(sketch, "E1046.endSnap0", {"position": v(-889.12, 183.89) * mm});
            skLineSegment(sketch, "E1047", {"start": v(-912.6, 229) * mm, "end": v(-887.2, 185) * mm});
            skLineSegment(sketch, "E1048.left", {"start": v(-892.4, 186.4) * mm, "end": v(-889.65, 187.98) * mm});
            skLineSegment(sketch, "E1048.right", {"start": v(-913.99, 223.79) * mm, "end": v(-911.24, 225.38) * mm});
            skPoint(sketch, "E1048.middle", {"position": v(-901.82, 205.89) * mm});
            skLineSegment(sketch, "E1049", {"start": v(-900.44, 206.68) * mm, "end": v(-903.2, 205.1) * mm, "construction": true});
            skLineSegment(sketch, "E1050", {"start": v(-904.89, 214.38) * mm, "end": v(-907.64, 212.8) * mm});
            skLineSegment(sketch, "E1051.MirrorCS", {"start": v(-896, 198.98) * mm, "end": v(-898.75, 197.4) * mm});
            skLineSegment(sketch, "E1052", {"start": v(-903.62, 212.18) * mm, "end": v(-906.37, 210.6) * mm});
            skLineSegment(sketch, "E1053.MirrorCS", {"start": v(-897.27, 201.18) * mm, "end": v(-900.02, 199.6) * mm});
            skLineSegment(sketch, "E1054", {"start": v(-911.24, 225.38) * mm, "end": v(-904.89, 214.38) * mm});
            skLineSegment(sketch, "E1055", {"start": v(-913.99, 223.79) * mm, "end": v(-907.64, 212.8) * mm});
            skLineSegment(sketch, "E1056", {"start": v(-906.37, 210.6) * mm, "end": v(-903.2, 205.1) * mm});
            skLineSegment(sketch, "E1057", {"start": v(-903.62, 212.18) * mm, "end": v(-900.44, 206.68) * mm});
            skLineSegment(sketch, "E1058", {"start": v(-900.44, 206.68) * mm, "end": v(-897.27, 201.18) * mm});
            skLineSegment(sketch, "E1059", {"start": v(-903.2, 205.1) * mm, "end": v(-900.02, 199.6) * mm});
            skLineSegment(sketch, "E1060", {"start": v(-896, 198.98) * mm, "end": v(-889.65, 187.98) * mm});
            skLineSegment(sketch, "E1061", {"start": v(-898.75, 197.4) * mm, "end": v(-892.4, 186.4) * mm});
            skLineSegment(sketch, "E1062.left", {"start": v(-969.7, 223.79) * mm, "end": v(-972.44, 225.38) * mm});
            skLineSegment(sketch, "E1062.right", {"start": v(-991.29, 186.4) * mm, "end": v(-994.03, 187.98) * mm});
            skLineSegment(sketch, "E1063", {"start": v(-983.24, 206.68) * mm, "end": v(-980.5, 205.1) * mm, "construction": true});
            skLineSegment(sketch, "E1064", {"start": v(-987.68, 198.98) * mm, "end": v(-984.94, 197.4) * mm});
            skLineSegment(sketch, "E1065.MirrorCS", {"start": v(-978.8, 214.38) * mm, "end": v(-976.05, 212.8) * mm});
            skLineSegment(sketch, "E1066", {"start": v(-986.41, 201.18) * mm, "end": v(-983.67, 199.6) * mm});
            skLineSegment(sketch, "E1067.MirrorCS", {"start": v(-980.06, 212.18) * mm, "end": v(-977.32, 210.6) * mm});
            skLineSegment(sketch, "E1068.0", {"start": v(-967.24, 226.77) * mm, "end": v(-971.09, 229) * mm, "construction": true});
            skLineSegment(sketch, "E1069", {"start": v(-891.04, 182.78) * mm, "end": v(-887.2, 185) * mm});
            skLineSegment(sketch, "E1070.MirrorCS", {"start": v(-900.44, 158.87) * mm, "end": v(-903.2, 160.46) * mm, "construction": true});
            skLineSegment(sketch, "E1071.MirrorCS", {"start": v(-983.24, 158.87) * mm, "end": v(-980.5, 160.46) * mm, "construction": true});
            skLineSegment(sketch, "E1072.MirrorCS", {"start": v(-941.84, 134.97) * mm, "end": v(-941.84, 138.15) * mm, "construction": true});
            skLineSegment(sketch, "E1073.MirrorCS", {"start": v(-967.24, 138.78) * mm, "end": v(-971.09, 136.56) * mm, "construction": true});
            skLineSegment(sketch, "E1074.MirrorCS", {"start": v(-912.6, 136.56) * mm, "end": v(-916.44, 138.78) * mm});
            skLineSegment(sketch, "E1075.MirrorCS", {"start": v(-913.99, 141.76) * mm, "end": v(-911.24, 140.18) * mm});
            skLineSegment(sketch, "E1076.MirrorCS", {"start": v(-980.06, 153.38) * mm, "end": v(-977.32, 154.96) * mm});
            skLineSegment(sketch, "E1077.MirrorCS", {"start": v(-935.5, 134.97) * mm, "end": v(-935.5, 138.15) * mm});
            skLineSegment(sketch, "E1078.MirrorCS", {"start": v(-916.44, 134.34) * mm, "end": v(-916.44, 138.78) * mm});
            skLineSegment(sketch, "E1079.MirrorCS", {"start": v(-950.73, 134.97) * mm, "end": v(-950.73, 138.15) * mm});
            skLineSegment(sketch, "E1080.MirrorCS", {"start": v(-904.89, 151.18) * mm, "end": v(-907.64, 152.76) * mm});
            skLineSegment(sketch, "E1081.MirrorCS", {"start": v(-948.2, 134.97) * mm, "end": v(-948.2, 138.15) * mm});
            skLineSegment(sketch, "E1082.MirrorCS", {"start": v(-969.7, 141.76) * mm, "end": v(-972.44, 140.18) * mm});
            skLineSegment(sketch, "E1083.MirrorCS", {"start": v(-991.29, 179.16) * mm, "end": v(-994.03, 177.57) * mm});
            skLineSegment(sketch, "E1084.MirrorCS", {"start": v(-986.41, 164.37) * mm, "end": v(-983.67, 165.96) * mm});
            skLineSegment(sketch, "E1085.MirrorCS", {"start": v(-996.49, 180.55) * mm, "end": v(-992.64, 182.78) * mm});
            skLineSegment(sketch, "E1086.MirrorCS", {"start": v(-903.62, 153.38) * mm, "end": v(-906.37, 154.96) * mm});
            skLineSegment(sketch, "E1087.MirrorCS", {"start": v(-932.95, 134.97) * mm, "end": v(-932.95, 138.15) * mm});
            skLineSegment(sketch, "E1088.MirrorCS", {"start": v(-987.68, 166.57) * mm, "end": v(-984.94, 168.16) * mm});
            skLineSegment(sketch, "E1089.MirrorCS", {"start": v(-892.4, 179.16) * mm, "end": v(-889.65, 177.57) * mm});
            skLineSegment(sketch, "E1090.MirrorCS", {"start": v(-963.43, 138.15) * mm, "end": v(-963.43, 134.97) * mm});
            skLineSegment(sketch, "E1091.MirrorCS", {"start": v(-896, 166.57) * mm, "end": v(-898.75, 168.16) * mm});
            skLineSegment(sketch, "E1092.MirrorCS", {"start": v(-891.04, 182.78) * mm, "end": v(-887.2, 180.55) * mm});
            skLineSegment(sketch, "E1093.MirrorCS", {"start": v(-897.27, 164.37) * mm, "end": v(-900.02, 165.96) * mm});
            skLineSegment(sketch, "E1094.MirrorCS", {"start": v(-978.8, 151.18) * mm, "end": v(-976.05, 152.76) * mm});
            skLineSegment(sketch, "E1095.MirrorCS", {"start": v(-920.25, 138.15) * mm, "end": v(-920.25, 134.97) * mm});
            skLineSegment(sketch, "E1096.MirrorCS", {"start": v(-906.37, 154.96) * mm, "end": v(-903.2, 160.46) * mm});
            skLineSegment(sketch, "E1097.MirrorCS", {"start": v(-900.44, 158.87) * mm, "end": v(-897.27, 164.37) * mm});
            skLineSegment(sketch, "E1098.MirrorCS", {"start": v(-967.24, 134.34) * mm, "end": v(-967.24, 138.78) * mm});
            skLineSegment(sketch, "E1099.MirrorCS", {"start": v(-903.2, 160.46) * mm, "end": v(-900.02, 165.96) * mm});
            skLineSegment(sketch, "E1100.MirrorCS", {"start": v(-903.62, 153.38) * mm, "end": v(-900.44, 158.87) * mm});
            skLineSegment(sketch, "E1101.MirrorCS", {"start": v(-898.75, 168.16) * mm, "end": v(-892.4, 179.16) * mm});
            skLineSegment(sketch, "E1102.MirrorCS", {"start": v(-916.44, 138.78) * mm, "end": v(-891.04, 182.78) * mm});
            skLineSegment(sketch, "E1103.MirrorCS", {"start": v(-911.24, 140.18) * mm, "end": v(-904.89, 151.18) * mm});
            skPoint(sketch, "E1104.MirrorP", {"position": v(-901.82, 159.67) * mm});
            skLineSegment(sketch, "E1105.MirrorCS", {"start": v(-896, 166.57) * mm, "end": v(-889.65, 177.57) * mm});
            skLineSegment(sketch, "E1106.MirrorCS", {"start": v(-913.99, 141.76) * mm, "end": v(-907.64, 152.76) * mm});
            skLineSegment(sketch, "E1107.MirrorCS", {"start": v(-912.6, 136.56) * mm, "end": v(-887.2, 180.55) * mm});
            skPoint(sketch, "E1108.MirrorP", {"position": v(-889.12, 181.67) * mm});
            skLineSegment(sketch, "E1109", {"start": v(-967.24, 319.2) * mm, "end": v(-916.44, 319.2) * mm});
            skLineSegment(sketch, "E1110", {"start": v(-967.24, 323.65) * mm, "end": v(-967.24, 319.2) * mm});
            skLineSegment(sketch, "E1111", {"start": v(-916.44, 323.65) * mm, "end": v(-916.44, 319.2) * mm});
            skLineSegment(sketch, "E1112", {"start": v(-992.64, 275.21) * mm, "end": v(-891.04, 275.21) * mm, "construction": true});
            skPoint(sketch, "E1113.endSnap0", {"position": v(-916.44, 321.43) * mm});
            skLineSegment(sketch, "E1114", {"start": v(-967.24, 321.43) * mm, "end": v(-916.44, 321.43) * mm, "construction": true});
            skLineSegment(sketch, "E1115", {"start": v(-967.24, 323.65) * mm, "end": v(-916.44, 323.65) * mm});
            skLineSegment(sketch, "E1116", {"start": v(-996.49, 277.43) * mm, "end": v(-992.64, 275.21) * mm});
            skLineSegment(sketch, "E1117.left", {"start": v(-920.25, 319.84) * mm, "end": v(-920.25, 323.01) * mm});
            skLineSegment(sketch, "E1117.right", {"start": v(-963.43, 319.84) * mm, "end": v(-963.43, 323.01) * mm});
            skPoint(sketch, "E1117.middle", {"position": v(-941.84, 321.43) * mm});
            skLineSegment(sketch, "E1118", {"start": v(-941.84, 323.01) * mm, "end": v(-941.84, 319.84) * mm, "construction": true});
            skLineSegment(sketch, "E1119", {"start": v(-950.73, 323.01) * mm, "end": v(-950.73, 319.84) * mm});
            skLineSegment(sketch, "E1120.MirrorCS", {"start": v(-932.95, 323.01) * mm, "end": v(-932.95, 319.84) * mm});
            skLineSegment(sketch, "E1121", {"start": v(-948.2, 323.01) * mm, "end": v(-948.2, 319.84) * mm});
            skLineSegment(sketch, "E1122.MirrorCS", {"start": v(-935.5, 323.01) * mm, "end": v(-935.5, 319.84) * mm});
            skLineSegment(sketch, "E1123", {"start": v(-963.43, 323.01) * mm, "end": v(-950.73, 323.01) * mm});
            skLineSegment(sketch, "E1124", {"start": v(-963.43, 319.84) * mm, "end": v(-950.73, 319.84) * mm});
            skLineSegment(sketch, "E1125", {"start": v(-948.2, 319.84) * mm, "end": v(-941.84, 319.84) * mm});
            skLineSegment(sketch, "E1126", {"start": v(-948.2, 323.01) * mm, "end": v(-941.84, 323.01) * mm});
            skLineSegment(sketch, "E1127", {"start": v(-941.84, 323.01) * mm, "end": v(-935.5, 323.01) * mm});
            skLineSegment(sketch, "E1128", {"start": v(-941.84, 319.84) * mm, "end": v(-935.5, 319.84) * mm});
            skLineSegment(sketch, "E1129", {"start": v(-932.95, 323.01) * mm, "end": v(-920.25, 323.01) * mm});
            skLineSegment(sketch, "E1130", {"start": v(-932.95, 319.84) * mm, "end": v(-920.25, 319.84) * mm});
            skLineSegment(sketch, "E1131", {"start": v(-916.44, 319.2) * mm, "end": v(-891.04, 275.21) * mm});
            skLineSegment(sketch, "E1132", {"start": v(-912.6, 321.43) * mm, "end": v(-916.44, 319.2) * mm});
            skPoint(sketch, "E1133.endSnap0", {"position": v(-889.12, 276.32) * mm});
            skLineSegment(sketch, "E1134", {"start": v(-912.6, 321.43) * mm, "end": v(-887.2, 277.43) * mm});
            skLineSegment(sketch, "E1135.left", {"start": v(-892.4, 278.83) * mm, "end": v(-889.65, 280.41) * mm});
            skLineSegment(sketch, "E1135.right", {"start": v(-913.99, 316.22) * mm, "end": v(-911.24, 317.8) * mm});
            skPoint(sketch, "E1135.middle", {"position": v(-901.82, 298.32) * mm});
            skLineSegment(sketch, "E1136", {"start": v(-900.44, 299.11) * mm, "end": v(-903.2, 297.52) * mm, "construction": true});
            skLineSegment(sketch, "E1137", {"start": v(-904.89, 306.81) * mm, "end": v(-907.64, 305.22) * mm});
            skLineSegment(sketch, "E1138.MirrorCS", {"start": v(-896, 291.41) * mm, "end": v(-898.75, 289.83) * mm});
            skLineSegment(sketch, "E1139", {"start": v(-903.62, 304.61) * mm, "end": v(-906.37, 303.02) * mm});
            skLineSegment(sketch, "E1140.MirrorCS", {"start": v(-897.27, 293.61) * mm, "end": v(-900.02, 292.03) * mm});
            skLineSegment(sketch, "E1141", {"start": v(-911.24, 317.8) * mm, "end": v(-904.89, 306.81) * mm});
            skLineSegment(sketch, "E1142", {"start": v(-913.99, 316.22) * mm, "end": v(-907.64, 305.22) * mm});
            skLineSegment(sketch, "E1143", {"start": v(-906.37, 303.02) * mm, "end": v(-903.2, 297.52) * mm});
            skLineSegment(sketch, "E1144", {"start": v(-903.62, 304.61) * mm, "end": v(-900.44, 299.11) * mm});
            skLineSegment(sketch, "E1145", {"start": v(-900.44, 299.11) * mm, "end": v(-897.27, 293.61) * mm});
            skLineSegment(sketch, "E1146", {"start": v(-903.2, 297.52) * mm, "end": v(-900.02, 292.03) * mm});
            skLineSegment(sketch, "E1147", {"start": v(-896, 291.41) * mm, "end": v(-889.65, 280.41) * mm});
            skLineSegment(sketch, "E1148", {"start": v(-898.75, 289.83) * mm, "end": v(-892.4, 278.83) * mm});
            skLineSegment(sketch, "E1149", {"start": v(-992.64, 275.21) * mm, "end": v(-967.24, 319.2) * mm});
            skLineSegment(sketch, "E1150", {"start": v(-971.09, 321.43) * mm, "end": v(-967.24, 319.2) * mm});
            skPoint(sketch, "E1151.endSnap0", {"position": v(-969.17, 320.32) * mm});
            skLineSegment(sketch, "E1152", {"start": v(-996.49, 277.43) * mm, "end": v(-971.09, 321.43) * mm});
            skLineSegment(sketch, "E1153.left", {"start": v(-969.7, 316.22) * mm, "end": v(-972.44, 317.8) * mm});
            skLineSegment(sketch, "E1153.right", {"start": v(-991.29, 278.83) * mm, "end": v(-994.03, 280.41) * mm});
            skPoint(sketch, "E1153.middle", {"position": v(-981.87, 298.32) * mm});
            skLineSegment(sketch, "E1154", {"start": v(-983.24, 299.11) * mm, "end": v(-980.5, 297.52) * mm, "construction": true});
            skLineSegment(sketch, "E1155", {"start": v(-987.68, 291.41) * mm, "end": v(-984.94, 289.83) * mm});
            skLineSegment(sketch, "E1156.MirrorCS", {"start": v(-978.8, 306.81) * mm, "end": v(-976.05, 305.22) * mm});
            skLineSegment(sketch, "E1157", {"start": v(-986.41, 293.61) * mm, "end": v(-983.67, 292.03) * mm});
            skLineSegment(sketch, "E1158.MirrorCS", {"start": v(-980.06, 304.61) * mm, "end": v(-977.32, 303.02) * mm});
            skLineSegment(sketch, "E1159", {"start": v(-994.03, 280.41) * mm, "end": v(-987.68, 291.41) * mm});
            skLineSegment(sketch, "E1160", {"start": v(-991.29, 278.83) * mm, "end": v(-984.94, 289.83) * mm});
            skLineSegment(sketch, "E1161", {"start": v(-983.67, 292.03) * mm, "end": v(-980.5, 297.52) * mm});
            skLineSegment(sketch, "E1162", {"start": v(-986.41, 293.61) * mm, "end": v(-983.24, 299.11) * mm});
            skLineSegment(sketch, "E1163", {"start": v(-983.24, 299.11) * mm, "end": v(-980.06, 304.61) * mm});
            skLineSegment(sketch, "E1164", {"start": v(-980.5, 297.52) * mm, "end": v(-977.32, 303.02) * mm});
            skLineSegment(sketch, "E1165", {"start": v(-978.8, 306.81) * mm, "end": v(-972.44, 317.8) * mm});
            skLineSegment(sketch, "E1166", {"start": v(-976.05, 305.22) * mm, "end": v(-969.7, 316.22) * mm});
            skLineSegment(sketch, "E1167.0", {"start": v(-967.24, 319.2) * mm, "end": v(-971.09, 321.43) * mm, "construction": true});
            skLineSegment(sketch, "E1168", {"start": v(-891.04, 275.21) * mm, "end": v(-887.2, 277.43) * mm});
            skLineSegment(sketch, "E1169.MirrorCS", {"start": v(-900.44, 251.3) * mm, "end": v(-903.2, 252.9) * mm, "construction": true});
            skLineSegment(sketch, "E1170.MirrorCS", {"start": v(-983.24, 251.3) * mm, "end": v(-980.5, 252.9) * mm, "construction": true});
            skLineSegment(sketch, "E1171.MirrorCS", {"start": v(-941.84, 227.4) * mm, "end": v(-941.84, 230.58) * mm, "construction": true});
            skLineSegment(sketch, "E1172.MirrorCS", {"start": v(-967.24, 231.22) * mm, "end": v(-971.09, 229) * mm, "construction": true});
            skLineSegment(sketch, "E1173.MirrorCS", {"start": v(-912.6, 229) * mm, "end": v(-916.44, 231.22) * mm});
            skLineSegment(sketch, "E1174.MirrorCS", {"start": v(-913.99, 234.2) * mm, "end": v(-911.24, 232.61) * mm});
            skLineSegment(sketch, "E1175.MirrorCS", {"start": v(-980.06, 245.8) * mm, "end": v(-977.32, 247.4) * mm});
            skLineSegment(sketch, "E1176.MirrorCS", {"start": v(-935.5, 227.4) * mm, "end": v(-935.5, 230.58) * mm});
            skLineSegment(sketch, "E1177.MirrorCS", {"start": v(-916.44, 226.77) * mm, "end": v(-916.44, 231.22) * mm});
            skLineSegment(sketch, "E1178.MirrorCS", {"start": v(-950.73, 227.4) * mm, "end": v(-950.73, 230.58) * mm});
            skLineSegment(sketch, "E1179.MirrorCS", {"start": v(-904.89, 243.6) * mm, "end": v(-907.64, 245.2) * mm});
            skLineSegment(sketch, "E1180.MirrorCS", {"start": v(-948.2, 227.4) * mm, "end": v(-948.2, 230.58) * mm});
            skLineSegment(sketch, "E1181.MirrorCS", {"start": v(-969.7, 234.2) * mm, "end": v(-972.44, 232.61) * mm});
            skLineSegment(sketch, "E1182.MirrorCS", {"start": v(-991.29, 271.6) * mm, "end": v(-994.03, 270) * mm});
            skLineSegment(sketch, "E1183.MirrorCS", {"start": v(-986.41, 256.8) * mm, "end": v(-983.67, 258.4) * mm});
            skLineSegment(sketch, "E1184.MirrorCS", {"start": v(-996.49, 272.99) * mm, "end": v(-992.64, 275.21) * mm});
            skLineSegment(sketch, "E1185.MirrorCS", {"start": v(-903.62, 245.8) * mm, "end": v(-906.37, 247.4) * mm});
            skLineSegment(sketch, "E1186.MirrorCS", {"start": v(-932.95, 227.4) * mm, "end": v(-932.95, 230.58) * mm});
            skLineSegment(sketch, "E1187.MirrorCS", {"start": v(-987.68, 259) * mm, "end": v(-984.94, 260.6) * mm});
            skLineSegment(sketch, "E1188.MirrorCS", {"start": v(-892.4, 271.6) * mm, "end": v(-889.65, 270) * mm});
            skLineSegment(sketch, "E1189.MirrorCS", {"start": v(-963.43, 230.58) * mm, "end": v(-963.43, 227.4) * mm});
            skLineSegment(sketch, "E1190.MirrorCS", {"start": v(-896, 259) * mm, "end": v(-898.75, 260.6) * mm});
            skLineSegment(sketch, "E1191.MirrorCS", {"start": v(-891.04, 275.21) * mm, "end": v(-887.2, 272.99) * mm});
            skLineSegment(sketch, "E1192.MirrorCS", {"start": v(-897.27, 256.8) * mm, "end": v(-900.02, 258.4) * mm});
            skLineSegment(sketch, "E1193.MirrorCS", {"start": v(-978.8, 243.6) * mm, "end": v(-976.05, 245.2) * mm});
            skLineSegment(sketch, "E1194.MirrorCS", {"start": v(-920.25, 230.58) * mm, "end": v(-920.25, 227.4) * mm});
            skLineSegment(sketch, "E1195.MirrorCS", {"start": v(-906.37, 247.4) * mm, "end": v(-903.2, 252.9) * mm});
            skLineSegment(sketch, "E1196.MirrorCS", {"start": v(-900.44, 251.3) * mm, "end": v(-897.27, 256.8) * mm});
            skLineSegment(sketch, "E1197.MirrorCS", {"start": v(-967.24, 226.77) * mm, "end": v(-967.24, 231.22) * mm});
            skLineSegment(sketch, "E1198.MirrorCS", {"start": v(-903.2, 252.9) * mm, "end": v(-900.02, 258.4) * mm});
            skLineSegment(sketch, "E1199.MirrorCS", {"start": v(-903.62, 245.8) * mm, "end": v(-900.44, 251.3) * mm});
            skLineSegment(sketch, "E1200.MirrorCS", {"start": v(-898.75, 260.6) * mm, "end": v(-892.4, 271.6) * mm});
            skLineSegment(sketch, "E1201.MirrorCS", {"start": v(-916.44, 231.22) * mm, "end": v(-891.04, 275.21) * mm});
            skLineSegment(sketch, "E1202.MirrorCS", {"start": v(-911.24, 232.61) * mm, "end": v(-904.89, 243.6) * mm});
            skPoint(sketch, "E1203.MirrorP", {"position": v(-901.82, 252.1) * mm});
            skLineSegment(sketch, "E1204.MirrorCS", {"start": v(-896, 259) * mm, "end": v(-889.65, 270) * mm});
            skLineSegment(sketch, "E1205.MirrorCS", {"start": v(-913.99, 234.2) * mm, "end": v(-907.64, 245.2) * mm});
            skLineSegment(sketch, "E1206.MirrorCS", {"start": v(-912.6, 229) * mm, "end": v(-887.2, 272.99) * mm});
            skPoint(sketch, "E1207.MirrorP", {"position": v(-889.12, 274.1) * mm});
            skLineSegment(sketch, "E1208", {"start": v(-887.2, 88.12) * mm, "end": v(-836.4, 88.12) * mm});
            skLineSegment(sketch, "E1209", {"start": v(-887.2, 92.57) * mm, "end": v(-887.2, 88.12) * mm});
            skLineSegment(sketch, "E1210", {"start": v(-836.4, 92.57) * mm, "end": v(-836.4, 88.12) * mm});
            skLineSegment(sketch, "E1211", {"start": v(-912.6, 44.13) * mm, "end": v(-811, 44.13) * mm, "construction": true});
            skPoint(sketch, "E1212.endSnap0", {"position": v(-836.4, 90.34) * mm});
            skLineSegment(sketch, "E1213", {"start": v(-887.2, 90.34) * mm, "end": v(-836.4, 90.34) * mm, "construction": true});
            skLineSegment(sketch, "E1214", {"start": v(-887.2, 92.57) * mm, "end": v(-836.4, 92.57) * mm});
            skLineSegment(sketch, "E1215", {"start": v(-916.44, 46.35) * mm, "end": v(-912.6, 44.13) * mm});
            skLineSegment(sketch, "E1216.left", {"start": v(-840.2, 88.76) * mm, "end": v(-840.2, 91.93) * mm});
            skLineSegment(sketch, "E1216.right", {"start": v(-883.38, 88.76) * mm, "end": v(-883.38, 91.93) * mm});
            skPoint(sketch, "E1216.middle", {"position": v(-861.8, 90.34) * mm});
            skLineSegment(sketch, "E1217", {"start": v(-861.8, 91.93) * mm, "end": v(-861.8, 88.76) * mm, "construction": true});
            skLineSegment(sketch, "E1218", {"start": v(-870.68, 91.93) * mm, "end": v(-870.68, 88.76) * mm});
            skLineSegment(sketch, "E1219.MirrorCS", {"start": v(-852.9, 91.93) * mm, "end": v(-852.9, 88.76) * mm});
            skLineSegment(sketch, "E1220", {"start": v(-868.14, 91.93) * mm, "end": v(-868.14, 88.76) * mm});
            skLineSegment(sketch, "E1221.MirrorCS", {"start": v(-855.44, 91.93) * mm, "end": v(-855.44, 88.76) * mm});
            skLineSegment(sketch, "E1222", {"start": v(-883.38, 91.93) * mm, "end": v(-870.68, 91.93) * mm});
            skLineSegment(sketch, "E1223", {"start": v(-883.38, 88.76) * mm, "end": v(-870.68, 88.76) * mm});
            skLineSegment(sketch, "E1224", {"start": v(-868.14, 88.76) * mm, "end": v(-861.8, 88.76) * mm});
            skLineSegment(sketch, "E1225", {"start": v(-868.14, 91.93) * mm, "end": v(-861.8, 91.93) * mm});
            skLineSegment(sketch, "E1226", {"start": v(-861.8, 91.93) * mm, "end": v(-855.44, 91.93) * mm});
            skLineSegment(sketch, "E1227", {"start": v(-861.8, 88.76) * mm, "end": v(-855.44, 88.76) * mm});
            skLineSegment(sketch, "E1228", {"start": v(-852.9, 91.93) * mm, "end": v(-840.2, 91.93) * mm});
            skLineSegment(sketch, "E1229", {"start": v(-852.9, 88.76) * mm, "end": v(-840.2, 88.76) * mm});
            skLineSegment(sketch, "E1230", {"start": v(-836.4, 88.12) * mm, "end": v(-811, 44.13) * mm});
            skLineSegment(sketch, "E1231", {"start": v(-832.54, 90.34) * mm, "end": v(-836.4, 88.12) * mm});
            skPoint(sketch, "E1232.endSnap0", {"position": v(-809.07, 45.24) * mm});
            skLineSegment(sketch, "E1233", {"start": v(-832.54, 90.34) * mm, "end": v(-807.14, 46.35) * mm});
            skLineSegment(sketch, "E1234.left", {"start": v(-812.35, 47.74) * mm, "end": v(-809.6, 49.33) * mm});
            skLineSegment(sketch, "E1234.right", {"start": v(-833.94, 85.14) * mm, "end": v(-831.19, 86.73) * mm});
            skPoint(sketch, "E1234.middle", {"position": v(-821.77, 67.24) * mm});
            skLineSegment(sketch, "E1235", {"start": v(-820.4, 68.03) * mm, "end": v(-823.14, 66.44) * mm, "construction": true});
            skLineSegment(sketch, "E1236", {"start": v(-824.84, 75.73) * mm, "end": v(-827.59, 74.14) * mm});
            skLineSegment(sketch, "E1237.MirrorCS", {"start": v(-815.95, 60.33) * mm, "end": v(-818.7, 58.74) * mm});
            skLineSegment(sketch, "E1238", {"start": v(-823.57, 73.53) * mm, "end": v(-826.32, 71.94) * mm});
            skLineSegment(sketch, "E1239.MirrorCS", {"start": v(-817.22, 62.53) * mm, "end": v(-819.97, 60.94) * mm});
            skLineSegment(sketch, "E1240", {"start": v(-831.19, 86.73) * mm, "end": v(-824.84, 75.73) * mm});
            skLineSegment(sketch, "E1241", {"start": v(-833.94, 85.14) * mm, "end": v(-827.59, 74.14) * mm});
            skLineSegment(sketch, "E1242", {"start": v(-826.32, 71.94) * mm, "end": v(-823.14, 66.44) * mm});
            skLineSegment(sketch, "E1243", {"start": v(-823.57, 73.53) * mm, "end": v(-820.4, 68.03) * mm});
            skLineSegment(sketch, "E1244", {"start": v(-820.4, 68.03) * mm, "end": v(-817.22, 62.53) * mm});
            skLineSegment(sketch, "E1245", {"start": v(-823.14, 66.44) * mm, "end": v(-819.97, 60.94) * mm});
            skLineSegment(sketch, "E1246", {"start": v(-815.95, 60.33) * mm, "end": v(-809.6, 49.33) * mm});
            skLineSegment(sketch, "E1247", {"start": v(-818.7, 58.74) * mm, "end": v(-812.35, 47.74) * mm});
            skLineSegment(sketch, "E1248.left", {"start": v(-889.65, 85.14) * mm, "end": v(-892.4, 86.73) * mm});
            skLineSegment(sketch, "E1248.right", {"start": v(-911.24, 47.74) * mm, "end": v(-913.99, 49.33) * mm});
            skLineSegment(sketch, "E1249", {"start": v(-903.2, 68.03) * mm, "end": v(-900.44, 66.44) * mm, "construction": true});
            skLineSegment(sketch, "E1250", {"start": v(-907.64, 60.33) * mm, "end": v(-904.89, 58.74) * mm});
            skLineSegment(sketch, "E1251.MirrorCS", {"start": v(-898.75, 75.73) * mm, "end": v(-896, 74.14) * mm});
            skLineSegment(sketch, "E1252", {"start": v(-906.37, 62.53) * mm, "end": v(-903.62, 60.94) * mm});
            skLineSegment(sketch, "E1253.MirrorCS", {"start": v(-900.02, 73.53) * mm, "end": v(-897.27, 71.94) * mm});
            skLineSegment(sketch, "E1254.0", {"start": v(-887.2, 88.12) * mm, "end": v(-891.04, 90.34) * mm, "construction": true});
            skLineSegment(sketch, "E1255", {"start": v(-811, 44.13) * mm, "end": v(-807.14, 46.35) * mm});
            skLineSegment(sketch, "E1256.MirrorCS", {"start": v(-891.04, -2.09) * mm, "end": v(-887.2, 0.13) * mm});
            skLineSegment(sketch, "E1257.MirrorCS", {"start": v(-820.4, 20.23) * mm, "end": v(-823.14, 21.81) * mm, "construction": true});
            skLineSegment(sketch, "E1258.MirrorCS", {"start": v(-903.2, 20.23) * mm, "end": v(-900.44, 21.81) * mm, "construction": true});
            skLineSegment(sketch, "E1259.MirrorCS", {"start": v(-861.8, -3.68) * mm, "end": v(-861.8, -0.5) * mm, "construction": true});
            skLineSegment(sketch, "E1260.MirrorCS", {"start": v(-887.2, 0.13) * mm, "end": v(-891.04, -2.09) * mm, "construction": true});
            skLineSegment(sketch, "E1261.MirrorCS", {"start": v(-832.54, -2.09) * mm, "end": v(-836.4, 0.13) * mm});
            skLineSegment(sketch, "E1262.MirrorCS", {"start": v(-833.94, 3.12) * mm, "end": v(-831.19, 1.53) * mm});
            skLineSegment(sketch, "E1263.MirrorCS", {"start": v(-900.02, 14.73) * mm, "end": v(-897.27, 16.31) * mm});
            skLineSegment(sketch, "E1264.MirrorCS", {"start": v(-855.44, -3.68) * mm, "end": v(-855.44, -0.5) * mm});
            skLineSegment(sketch, "E1265.MirrorCS", {"start": v(-836.4, -4.31) * mm, "end": v(-836.4, 0.13) * mm});
            skLineSegment(sketch, "E1266.MirrorCS", {"start": v(-870.68, -3.68) * mm, "end": v(-870.68, -0.5) * mm});
            skLineSegment(sketch, "E1267.MirrorCS", {"start": v(-824.84, 12.53) * mm, "end": v(-827.59, 14.11) * mm});
            skLineSegment(sketch, "E1268.MirrorCS", {"start": v(-868.14, -3.68) * mm, "end": v(-868.14, -0.5) * mm});
            skLineSegment(sketch, "E1269.MirrorCS", {"start": v(-889.65, 3.12) * mm, "end": v(-892.4, 1.53) * mm});
            skLineSegment(sketch, "E1270.MirrorCS", {"start": v(-911.24, 40.51) * mm, "end": v(-913.99, 38.92) * mm});
            skLineSegment(sketch, "E1271.MirrorCS", {"start": v(-906.37, 25.72) * mm, "end": v(-903.62, 27.31) * mm});
            skLineSegment(sketch, "E1272.MirrorCS", {"start": v(-916.44, 41.9) * mm, "end": v(-912.6, 44.13) * mm});
            skLineSegment(sketch, "E1273.MirrorCS", {"start": v(-823.57, 14.73) * mm, "end": v(-826.32, 16.31) * mm});
            skLineSegment(sketch, "E1274.MirrorCS", {"start": v(-852.9, -3.68) * mm, "end": v(-852.9, -0.5) * mm});
            skLineSegment(sketch, "E1275.MirrorCS", {"start": v(-907.64, 27.92) * mm, "end": v(-904.89, 29.51) * mm});
            skLineSegment(sketch, "E1276.MirrorCS", {"start": v(-812.35, 40.51) * mm, "end": v(-809.6, 38.92) * mm});
            skLineSegment(sketch, "E1277.MirrorCS", {"start": v(-883.38, -0.5) * mm, "end": v(-883.38, -3.68) * mm});
            skLineSegment(sketch, "E1278.MirrorCS", {"start": v(-815.95, 27.92) * mm, "end": v(-818.7, 29.51) * mm});
            skLineSegment(sketch, "E1279.MirrorCS", {"start": v(-811, 44.13) * mm, "end": v(-807.14, 41.9) * mm});
            skLineSegment(sketch, "E1280.MirrorCS", {"start": v(-817.22, 25.72) * mm, "end": v(-819.97, 27.31) * mm});
            skLineSegment(sketch, "E1281.MirrorCS", {"start": v(-898.75, 12.53) * mm, "end": v(-896, 14.11) * mm});
            skLineSegment(sketch, "E1282.MirrorCS", {"start": v(-840.2, -0.5) * mm, "end": v(-840.2, -3.68) * mm});
            skLineSegment(sketch, "E1283.MirrorCS", {"start": v(-826.32, 16.31) * mm, "end": v(-823.14, 21.81) * mm});
            skLineSegment(sketch, "E1284.MirrorCS", {"start": v(-868.14, -0.5) * mm, "end": v(-861.8, -0.5) * mm});
            skLineSegment(sketch, "E1285.MirrorCS", {"start": v(-903.62, 27.31) * mm, "end": v(-900.44, 21.81) * mm});
            skLineSegment(sketch, "E1286.MirrorCS", {"start": v(-820.4, 20.23) * mm, "end": v(-817.22, 25.72) * mm});
            skLineSegment(sketch, "E1287.MirrorCS", {"start": v(-887.2, -4.31) * mm, "end": v(-887.2, 0.13) * mm});
            skLineSegment(sketch, "E1288.MirrorCS", {"start": v(-861.8, -3.68) * mm, "end": v(-855.44, -3.68) * mm});
            skLineSegment(sketch, "E1289.MirrorCS", {"start": v(-823.14, 21.81) * mm, "end": v(-819.97, 27.31) * mm});
            skPoint(sketch, "E1290.MirrorP", {"position": v(-861.8, -2.09) * mm});
            skLineSegment(sketch, "E1291.MirrorCS", {"start": v(-861.8, -0.5) * mm, "end": v(-855.44, -0.5) * mm});
            skLineSegment(sketch, "E1292.MirrorCS", {"start": v(-823.57, 14.73) * mm, "end": v(-820.4, 20.23) * mm});
            skLineSegment(sketch, "E1293.MirrorCS", {"start": v(-900.44, 21.81) * mm, "end": v(-897.27, 16.31) * mm});
            skLineSegment(sketch, "E1294.MirrorCS", {"start": v(-868.14, -3.68) * mm, "end": v(-861.8, -3.68) * mm});
            skLineSegment(sketch, "E1295.MirrorCS", {"start": v(-818.7, 29.51) * mm, "end": v(-812.35, 40.51) * mm});
            skLineSegment(sketch, "E1296.MirrorCS", {"start": v(-916.44, 41.9) * mm, "end": v(-891.04, -2.09) * mm});
            skLineSegment(sketch, "E1297.MirrorCS", {"start": v(-852.9, -3.68) * mm, "end": v(-840.2, -3.68) * mm});
            skLineSegment(sketch, "E1298.MirrorCS", {"start": v(-836.4, 0.13) * mm, "end": v(-811, 44.13) * mm});
            skLineSegment(sketch, "E1299.MirrorCS", {"start": v(-831.19, 1.53) * mm, "end": v(-824.84, 12.53) * mm});
            skLineSegment(sketch, "E1300.MirrorCS", {"start": v(-911.24, 40.51) * mm, "end": v(-904.89, 29.51) * mm});
            skLineSegment(sketch, "E1301.MirrorCS", {"start": v(-896, 14.11) * mm, "end": v(-889.65, 3.12) * mm});
            skLineSegment(sketch, "E1302.MirrorCS", {"start": v(-852.9, -0.5) * mm, "end": v(-840.2, -0.5) * mm});
            skPoint(sketch, "E1303.MirrorP", {"position": v(-821.77, 21.02) * mm});
            skLineSegment(sketch, "E1304.MirrorCS", {"start": v(-815.95, 27.92) * mm, "end": v(-809.6, 38.92) * mm});
            skLineSegment(sketch, "E1305.MirrorCS", {"start": v(-887.2, 0.13) * mm, "end": v(-836.4, 0.13) * mm});
            skPoint(sketch, "E1306.MirrorP", {"position": v(-836.4, -2.09) * mm});
            skPoint(sketch, "E1307.MirrorP", {"position": v(-889.12, -0.98) * mm});
            skLineSegment(sketch, "E1308.MirrorCS", {"start": v(-906.37, 25.72) * mm, "end": v(-903.2, 20.23) * mm});
            skLineSegment(sketch, "E1309.MirrorCS", {"start": v(-887.2, -4.31) * mm, "end": v(-836.4, -4.31) * mm});
            skLineSegment(sketch, "E1310.MirrorCS", {"start": v(-883.38, -0.5) * mm, "end": v(-870.68, -0.5) * mm});
            skPoint(sketch, "E1311.MirrorP", {"position": v(-901.82, 21.02) * mm});
            skLineSegment(sketch, "E1312.MirrorCS", {"start": v(-887.2, -2.09) * mm, "end": v(-836.4, -2.09) * mm, "construction": true});
            skLineSegment(sketch, "E1313.MirrorCS", {"start": v(-833.94, 3.12) * mm, "end": v(-827.59, 14.11) * mm});
            skLineSegment(sketch, "E1314.MirrorCS", {"start": v(-832.54, -2.09) * mm, "end": v(-807.14, 41.9) * mm});
            skLineSegment(sketch, "E1315.MirrorCS", {"start": v(-883.38, -3.68) * mm, "end": v(-870.68, -3.68) * mm});
            skLineSegment(sketch, "E1316.MirrorCS", {"start": v(-912.6, 44.13) * mm, "end": v(-887.2, 0.13) * mm});
            skLineSegment(sketch, "E1317.MirrorCS", {"start": v(-898.75, 12.53) * mm, "end": v(-892.4, 1.53) * mm});
            skLineSegment(sketch, "E1318.MirrorCS", {"start": v(-913.99, 38.92) * mm, "end": v(-907.64, 27.92) * mm});
            skLineSegment(sketch, "E1319.MirrorCS", {"start": v(-903.2, 20.23) * mm, "end": v(-900.02, 14.73) * mm});
            skPoint(sketch, "E1320.MirrorP", {"position": v(-809.07, 43.02) * mm});
            skLineSegment(sketch, "E1321", {"start": v(-887.2, 180.55) * mm, "end": v(-836.4, 180.55) * mm});
            skLineSegment(sketch, "E1322", {"start": v(-887.2, 185) * mm, "end": v(-887.2, 180.55) * mm});
            skLineSegment(sketch, "E1323", {"start": v(-836.4, 185) * mm, "end": v(-836.4, 180.55) * mm});
            skLineSegment(sketch, "E1324", {"start": v(-912.6, 136.56) * mm, "end": v(-811, 136.56) * mm, "construction": true});
            skPoint(sketch, "E1325.endSnap0", {"position": v(-836.4, 182.78) * mm});
            skLineSegment(sketch, "E1326", {"start": v(-887.2, 182.78) * mm, "end": v(-836.4, 182.78) * mm, "construction": true});
            skLineSegment(sketch, "E1327", {"start": v(-887.2, 185) * mm, "end": v(-836.4, 185) * mm});
            skLineSegment(sketch, "E1328", {"start": v(-916.44, 138.78) * mm, "end": v(-912.6, 136.56) * mm});
            skLineSegment(sketch, "E1329.left", {"start": v(-840.2, 181.19) * mm, "end": v(-840.2, 184.36) * mm});
            skLineSegment(sketch, "E1329.right", {"start": v(-883.38, 181.19) * mm, "end": v(-883.38, 184.36) * mm});
            skPoint(sketch, "E1329.middle", {"position": v(-861.8, 182.78) * mm});
            skLineSegment(sketch, "E1330", {"start": v(-861.8, 184.36) * mm, "end": v(-861.8, 181.19) * mm, "construction": true});
            skLineSegment(sketch, "E1331", {"start": v(-870.68, 184.36) * mm, "end": v(-870.68, 181.19) * mm});
            skLineSegment(sketch, "E1332.MirrorCS", {"start": v(-852.9, 184.36) * mm, "end": v(-852.9, 181.19) * mm});
            skLineSegment(sketch, "E1333", {"start": v(-868.14, 184.36) * mm, "end": v(-868.14, 181.19) * mm});
            skLineSegment(sketch, "E1334.MirrorCS", {"start": v(-855.44, 184.36) * mm, "end": v(-855.44, 181.19) * mm});
            skLineSegment(sketch, "E1335", {"start": v(-883.38, 184.36) * mm, "end": v(-870.68, 184.36) * mm});
            skLineSegment(sketch, "E1336", {"start": v(-883.38, 181.19) * mm, "end": v(-870.68, 181.19) * mm});
            skLineSegment(sketch, "E1337", {"start": v(-868.14, 181.19) * mm, "end": v(-861.8, 181.19) * mm});
            skLineSegment(sketch, "E1338", {"start": v(-868.14, 184.36) * mm, "end": v(-861.8, 184.36) * mm});
            skLineSegment(sketch, "E1339", {"start": v(-861.8, 184.36) * mm, "end": v(-855.44, 184.36) * mm});
            skLineSegment(sketch, "E1340", {"start": v(-861.8, 181.19) * mm, "end": v(-855.44, 181.19) * mm});
            skLineSegment(sketch, "E1341", {"start": v(-852.9, 184.36) * mm, "end": v(-840.2, 184.36) * mm});
            skLineSegment(sketch, "E1342", {"start": v(-852.9, 181.19) * mm, "end": v(-840.2, 181.19) * mm});
            skLineSegment(sketch, "E1343", {"start": v(-836.4, 180.55) * mm, "end": v(-811, 136.56) * mm});
            skLineSegment(sketch, "E1344", {"start": v(-832.54, 182.78) * mm, "end": v(-836.4, 180.55) * mm});
            skPoint(sketch, "E1345.endSnap0", {"position": v(-809.07, 137.67) * mm});
            skLineSegment(sketch, "E1346", {"start": v(-832.54, 182.78) * mm, "end": v(-807.14, 138.78) * mm});
            skLineSegment(sketch, "E1347.left", {"start": v(-812.35, 140.18) * mm, "end": v(-809.6, 141.76) * mm});
            skLineSegment(sketch, "E1347.right", {"start": v(-833.94, 177.57) * mm, "end": v(-831.19, 179.16) * mm});
            skPoint(sketch, "E1347.middle", {"position": v(-821.77, 159.67) * mm});
            skLineSegment(sketch, "E1348", {"start": v(-820.4, 160.46) * mm, "end": v(-823.14, 158.87) * mm, "construction": true});
            skLineSegment(sketch, "E1349", {"start": v(-824.84, 168.16) * mm, "end": v(-827.59, 166.57) * mm});
            skLineSegment(sketch, "E1350.MirrorCS", {"start": v(-815.95, 152.76) * mm, "end": v(-818.7, 151.18) * mm});
            skLineSegment(sketch, "E1351", {"start": v(-823.57, 165.96) * mm, "end": v(-826.32, 164.37) * mm});
            skLineSegment(sketch, "E1352.MirrorCS", {"start": v(-817.22, 154.96) * mm, "end": v(-819.97, 153.38) * mm});
            skLineSegment(sketch, "E1353", {"start": v(-831.19, 179.16) * mm, "end": v(-824.84, 168.16) * mm});
            skLineSegment(sketch, "E1354", {"start": v(-833.94, 177.57) * mm, "end": v(-827.59, 166.57) * mm});
            skLineSegment(sketch, "E1355", {"start": v(-826.32, 164.37) * mm, "end": v(-823.14, 158.87) * mm});
            skLineSegment(sketch, "E1356", {"start": v(-823.57, 165.96) * mm, "end": v(-820.4, 160.46) * mm});
            skLineSegment(sketch, "E1357", {"start": v(-820.4, 160.46) * mm, "end": v(-817.22, 154.96) * mm});
            skLineSegment(sketch, "E1358", {"start": v(-823.14, 158.87) * mm, "end": v(-819.97, 153.38) * mm});
            skLineSegment(sketch, "E1359", {"start": v(-815.95, 152.76) * mm, "end": v(-809.6, 141.76) * mm});
            skLineSegment(sketch, "E1360", {"start": v(-818.7, 151.18) * mm, "end": v(-812.35, 140.18) * mm});
            skLineSegment(sketch, "E1361.left", {"start": v(-889.65, 177.57) * mm, "end": v(-892.4, 179.16) * mm});
            skLineSegment(sketch, "E1361.right", {"start": v(-911.24, 140.18) * mm, "end": v(-913.99, 141.76) * mm});
            skLineSegment(sketch, "E1362", {"start": v(-903.2, 160.46) * mm, "end": v(-900.44, 158.87) * mm, "construction": true});
            skLineSegment(sketch, "E1363", {"start": v(-907.64, 152.76) * mm, "end": v(-904.89, 151.18) * mm});
            skLineSegment(sketch, "E1364.MirrorCS", {"start": v(-898.75, 168.16) * mm, "end": v(-896, 166.57) * mm});
            skLineSegment(sketch, "E1365", {"start": v(-906.37, 154.96) * mm, "end": v(-903.62, 153.38) * mm});
            skLineSegment(sketch, "E1366.MirrorCS", {"start": v(-900.02, 165.96) * mm, "end": v(-897.27, 164.37) * mm});
            skLineSegment(sketch, "E1367.0", {"start": v(-887.2, 180.55) * mm, "end": v(-891.04, 182.78) * mm, "construction": true});
            skLineSegment(sketch, "E1368", {"start": v(-811, 136.56) * mm, "end": v(-807.14, 138.78) * mm});
            skLineSegment(sketch, "E1369.MirrorCS", {"start": v(-820.4, 112.66) * mm, "end": v(-823.14, 114.25) * mm, "construction": true});
            skLineSegment(sketch, "E1370.MirrorCS", {"start": v(-903.2, 112.66) * mm, "end": v(-900.44, 114.25) * mm, "construction": true});
            skLineSegment(sketch, "E1371.MirrorCS", {"start": v(-861.8, 88.76) * mm, "end": v(-861.8, 91.93) * mm, "construction": true});
            skLineSegment(sketch, "E1372.MirrorCS", {"start": v(-887.2, 92.57) * mm, "end": v(-891.04, 90.34) * mm, "construction": true});
            skLineSegment(sketch, "E1373.MirrorCS", {"start": v(-832.54, 90.34) * mm, "end": v(-836.4, 92.57) * mm});
            skLineSegment(sketch, "E1374.MirrorCS", {"start": v(-833.94, 95.55) * mm, "end": v(-831.19, 93.96) * mm});
            skLineSegment(sketch, "E1375.MirrorCS", {"start": v(-900.02, 107.16) * mm, "end": v(-897.27, 108.75) * mm});
            skLineSegment(sketch, "E1376.MirrorCS", {"start": v(-855.44, 88.76) * mm, "end": v(-855.44, 91.93) * mm});
            skLineSegment(sketch, "E1377.MirrorCS", {"start": v(-836.4, 88.12) * mm, "end": v(-836.4, 92.57) * mm});
            skLineSegment(sketch, "E1378.MirrorCS", {"start": v(-870.68, 88.76) * mm, "end": v(-870.68, 91.93) * mm});
            skLineSegment(sketch, "E1379.MirrorCS", {"start": v(-824.84, 104.96) * mm, "end": v(-827.59, 106.55) * mm});
            skLineSegment(sketch, "E1380.MirrorCS", {"start": v(-868.14, 88.76) * mm, "end": v(-868.14, 91.93) * mm});
            skLineSegment(sketch, "E1381.MirrorCS", {"start": v(-889.65, 95.55) * mm, "end": v(-892.4, 93.96) * mm});
            skLineSegment(sketch, "E1382.MirrorCS", {"start": v(-911.24, 132.94) * mm, "end": v(-913.99, 131.36) * mm});
            skLineSegment(sketch, "E1383.MirrorCS", {"start": v(-906.37, 118.16) * mm, "end": v(-903.62, 119.75) * mm});
            skLineSegment(sketch, "E1384.MirrorCS", {"start": v(-916.44, 134.34) * mm, "end": v(-912.6, 136.56) * mm});
            skLineSegment(sketch, "E1385.MirrorCS", {"start": v(-823.57, 107.16) * mm, "end": v(-826.32, 108.75) * mm});
            skLineSegment(sketch, "E1386.MirrorCS", {"start": v(-852.9, 88.76) * mm, "end": v(-852.9, 91.93) * mm});
            skLineSegment(sketch, "E1387.MirrorCS", {"start": v(-907.64, 120.36) * mm, "end": v(-904.89, 121.94) * mm});
            skLineSegment(sketch, "E1388.MirrorCS", {"start": v(-812.35, 132.94) * mm, "end": v(-809.6, 131.36) * mm});
            skLineSegment(sketch, "E1389.MirrorCS", {"start": v(-883.38, 91.93) * mm, "end": v(-883.38, 88.76) * mm});
            skLineSegment(sketch, "E1390.MirrorCS", {"start": v(-815.95, 120.36) * mm, "end": v(-818.7, 121.94) * mm});
            skLineSegment(sketch, "E1391.MirrorCS", {"start": v(-811, 136.56) * mm, "end": v(-807.14, 134.34) * mm});
            skLineSegment(sketch, "E1392.MirrorCS", {"start": v(-817.22, 118.16) * mm, "end": v(-819.97, 119.75) * mm});
            skLineSegment(sketch, "E1393.MirrorCS", {"start": v(-898.75, 104.96) * mm, "end": v(-896, 106.55) * mm});
            skLineSegment(sketch, "E1394.MirrorCS", {"start": v(-840.2, 91.93) * mm, "end": v(-840.2, 88.76) * mm});
            skLineSegment(sketch, "E1395.MirrorCS", {"start": v(-826.32, 108.75) * mm, "end": v(-823.14, 114.25) * mm});
            skLineSegment(sketch, "E1396.MirrorCS", {"start": v(-820.4, 112.66) * mm, "end": v(-817.22, 118.16) * mm});
            skLineSegment(sketch, "E1397.MirrorCS", {"start": v(-887.2, 88.12) * mm, "end": v(-887.2, 92.57) * mm});
            skLineSegment(sketch, "E1398.MirrorCS", {"start": v(-823.14, 114.25) * mm, "end": v(-819.97, 119.75) * mm});
            skLineSegment(sketch, "E1399.MirrorCS", {"start": v(-823.57, 107.16) * mm, "end": v(-820.4, 112.66) * mm});
            skLineSegment(sketch, "E1400.MirrorCS", {"start": v(-818.7, 121.94) * mm, "end": v(-812.35, 132.94) * mm});
            skLineSegment(sketch, "E1401.MirrorCS", {"start": v(-836.4, 92.57) * mm, "end": v(-811, 136.56) * mm});
            skLineSegment(sketch, "E1402.MirrorCS", {"start": v(-831.19, 93.96) * mm, "end": v(-824.84, 104.96) * mm});
            skPoint(sketch, "E1403.MirrorP", {"position": v(-821.77, 113.45) * mm});
            skLineSegment(sketch, "E1404.MirrorCS", {"start": v(-815.95, 120.36) * mm, "end": v(-809.6, 131.36) * mm});
            skLineSegment(sketch, "E1405.MirrorCS", {"start": v(-833.94, 95.55) * mm, "end": v(-827.59, 106.55) * mm});
            skLineSegment(sketch, "E1406.MirrorCS", {"start": v(-832.54, 90.34) * mm, "end": v(-807.14, 134.34) * mm});
            skPoint(sketch, "E1407.MirrorP", {"position": v(-809.07, 135.45) * mm});
            skLineSegment(sketch, "E1408", {"start": v(-887.2, 272.99) * mm, "end": v(-836.4, 272.99) * mm});
            skLineSegment(sketch, "E1409", {"start": v(-887.2, 277.43) * mm, "end": v(-887.2, 272.99) * mm});
            skLineSegment(sketch, "E1410", {"start": v(-836.4, 277.43) * mm, "end": v(-836.4, 272.99) * mm});
            skLineSegment(sketch, "E1411", {"start": v(-912.6, 229) * mm, "end": v(-811, 229) * mm, "construction": true});
            skPoint(sketch, "E1412.endSnap0", {"position": v(-836.4, 275.21) * mm});
            skLineSegment(sketch, "E1413", {"start": v(-887.2, 275.21) * mm, "end": v(-836.4, 275.21) * mm, "construction": true});
            skLineSegment(sketch, "E1414", {"start": v(-887.2, 277.43) * mm, "end": v(-836.4, 277.43) * mm});
            skLineSegment(sketch, "E1415", {"start": v(-916.44, 231.22) * mm, "end": v(-912.6, 229) * mm});
            skLineSegment(sketch, "E1416.left", {"start": v(-840.2, 273.62) * mm, "end": v(-840.2, 276.8) * mm});
            skLineSegment(sketch, "E1416.right", {"start": v(-883.38, 273.62) * mm, "end": v(-883.38, 276.8) * mm});
            skPoint(sketch, "E1416.middle", {"position": v(-861.8, 275.21) * mm});
            skLineSegment(sketch, "E1417", {"start": v(-861.8, 276.8) * mm, "end": v(-861.8, 273.62) * mm, "construction": true});
            skLineSegment(sketch, "E1418", {"start": v(-870.68, 276.8) * mm, "end": v(-870.68, 273.62) * mm});
            skLineSegment(sketch, "E1419.MirrorCS", {"start": v(-852.9, 276.8) * mm, "end": v(-852.9, 273.62) * mm});
            skLineSegment(sketch, "E1420", {"start": v(-868.14, 276.8) * mm, "end": v(-868.14, 273.62) * mm});
            skLineSegment(sketch, "E1421.MirrorCS", {"start": v(-855.44, 276.8) * mm, "end": v(-855.44, 273.62) * mm});
            skLineSegment(sketch, "E1422", {"start": v(-883.38, 276.8) * mm, "end": v(-870.68, 276.8) * mm});
            skLineSegment(sketch, "E1423", {"start": v(-883.38, 273.62) * mm, "end": v(-870.68, 273.62) * mm});
            skLineSegment(sketch, "E1424", {"start": v(-868.14, 273.62) * mm, "end": v(-861.8, 273.62) * mm});
            skLineSegment(sketch, "E1425", {"start": v(-868.14, 276.8) * mm, "end": v(-861.8, 276.8) * mm});
            skLineSegment(sketch, "E1426", {"start": v(-861.8, 276.8) * mm, "end": v(-855.44, 276.8) * mm});
            skLineSegment(sketch, "E1427", {"start": v(-861.8, 273.62) * mm, "end": v(-855.44, 273.62) * mm});
            skLineSegment(sketch, "E1428", {"start": v(-852.9, 276.8) * mm, "end": v(-840.2, 276.8) * mm});
            skLineSegment(sketch, "E1429", {"start": v(-852.9, 273.62) * mm, "end": v(-840.2, 273.62) * mm});
            skLineSegment(sketch, "E1430", {"start": v(-836.4, 272.99) * mm, "end": v(-811, 229) * mm});
            skLineSegment(sketch, "E1431", {"start": v(-832.54, 275.21) * mm, "end": v(-836.4, 272.99) * mm});
            skPoint(sketch, "E1432.endSnap0", {"position": v(-809.07, 230.1) * mm});
            skLineSegment(sketch, "E1433", {"start": v(-832.54, 275.21) * mm, "end": v(-807.14, 231.22) * mm});
            skLineSegment(sketch, "E1434.left", {"start": v(-812.35, 232.61) * mm, "end": v(-809.6, 234.2) * mm});
            skLineSegment(sketch, "E1434.right", {"start": v(-833.94, 270) * mm, "end": v(-831.19, 271.6) * mm});
            skPoint(sketch, "E1434.middle", {"position": v(-821.77, 252.1) * mm});
            skLineSegment(sketch, "E1435", {"start": v(-820.4, 252.9) * mm, "end": v(-823.14, 251.3) * mm, "construction": true});
            skLineSegment(sketch, "E1436", {"start": v(-824.84, 260.6) * mm, "end": v(-827.59, 259) * mm});
            skLineSegment(sketch, "E1437.MirrorCS", {"start": v(-815.95, 245.2) * mm, "end": v(-818.7, 243.6) * mm});
            skLineSegment(sketch, "E1438", {"start": v(-823.57, 258.4) * mm, "end": v(-826.32, 256.8) * mm});
            skLineSegment(sketch, "E1439.MirrorCS", {"start": v(-817.22, 247.4) * mm, "end": v(-819.97, 245.8) * mm});
            skLineSegment(sketch, "E1440", {"start": v(-831.19, 271.6) * mm, "end": v(-824.84, 260.6) * mm});
            skLineSegment(sketch, "E1441", {"start": v(-833.94, 270) * mm, "end": v(-827.59, 259) * mm});
            skLineSegment(sketch, "E1442", {"start": v(-826.32, 256.8) * mm, "end": v(-823.14, 251.3) * mm});
            skLineSegment(sketch, "E1443", {"start": v(-823.57, 258.4) * mm, "end": v(-820.4, 252.9) * mm});
            skLineSegment(sketch, "E1444", {"start": v(-820.4, 252.9) * mm, "end": v(-817.22, 247.4) * mm});
            skLineSegment(sketch, "E1445", {"start": v(-823.14, 251.3) * mm, "end": v(-819.97, 245.8) * mm});
            skLineSegment(sketch, "E1446", {"start": v(-815.95, 245.2) * mm, "end": v(-809.6, 234.2) * mm});
            skLineSegment(sketch, "E1447", {"start": v(-818.7, 243.6) * mm, "end": v(-812.35, 232.61) * mm});
            skLineSegment(sketch, "E1448.left", {"start": v(-889.65, 270) * mm, "end": v(-892.4, 271.6) * mm});
            skLineSegment(sketch, "E1448.right", {"start": v(-911.24, 232.61) * mm, "end": v(-913.99, 234.2) * mm});
            skLineSegment(sketch, "E1449", {"start": v(-903.2, 252.9) * mm, "end": v(-900.44, 251.3) * mm, "construction": true});
            skLineSegment(sketch, "E1450", {"start": v(-907.64, 245.2) * mm, "end": v(-904.89, 243.6) * mm});
            skLineSegment(sketch, "E1451.MirrorCS", {"start": v(-898.75, 260.6) * mm, "end": v(-896, 259) * mm});
            skLineSegment(sketch, "E1452", {"start": v(-906.37, 247.4) * mm, "end": v(-903.62, 245.8) * mm});
            skLineSegment(sketch, "E1453.MirrorCS", {"start": v(-900.02, 258.4) * mm, "end": v(-897.27, 256.8) * mm});
            skLineSegment(sketch, "E1454.0", {"start": v(-887.2, 272.99) * mm, "end": v(-891.04, 275.21) * mm, "construction": true});
            skLineSegment(sketch, "E1455", {"start": v(-811, 229) * mm, "end": v(-807.14, 231.22) * mm});
            skLineSegment(sketch, "E1456.MirrorCS", {"start": v(-820.4, 205.1) * mm, "end": v(-823.14, 206.68) * mm, "construction": true});
            skLineSegment(sketch, "E1457.MirrorCS", {"start": v(-903.2, 205.1) * mm, "end": v(-900.44, 206.68) * mm, "construction": true});
            skLineSegment(sketch, "E1458.MirrorCS", {"start": v(-861.8, 181.19) * mm, "end": v(-861.8, 184.36) * mm, "construction": true});
            skLineSegment(sketch, "E1459.MirrorCS", {"start": v(-887.2, 185) * mm, "end": v(-891.04, 182.78) * mm, "construction": true});
            skLineSegment(sketch, "E1460.MirrorCS", {"start": v(-832.54, 182.78) * mm, "end": v(-836.4, 185) * mm});
            skLineSegment(sketch, "E1461.MirrorCS", {"start": v(-833.94, 187.98) * mm, "end": v(-831.19, 186.4) * mm});
            skLineSegment(sketch, "E1462.MirrorCS", {"start": v(-900.02, 199.6) * mm, "end": v(-897.27, 201.18) * mm});
            skLineSegment(sketch, "E1463.MirrorCS", {"start": v(-855.44, 181.19) * mm, "end": v(-855.44, 184.36) * mm});
            skLineSegment(sketch, "E1464.MirrorCS", {"start": v(-836.4, 180.55) * mm, "end": v(-836.4, 185) * mm});
            skLineSegment(sketch, "E1465.MirrorCS", {"start": v(-870.68, 181.19) * mm, "end": v(-870.68, 184.36) * mm});
            skLineSegment(sketch, "E1466.MirrorCS", {"start": v(-824.84, 197.4) * mm, "end": v(-827.59, 198.98) * mm});
            skLineSegment(sketch, "E1467.MirrorCS", {"start": v(-868.14, 181.19) * mm, "end": v(-868.14, 184.36) * mm});
            skLineSegment(sketch, "E1468.MirrorCS", {"start": v(-889.65, 187.98) * mm, "end": v(-892.4, 186.4) * mm});
            skLineSegment(sketch, "E1469.MirrorCS", {"start": v(-911.24, 225.38) * mm, "end": v(-913.99, 223.79) * mm});
            skLineSegment(sketch, "E1470.MirrorCS", {"start": v(-906.37, 210.6) * mm, "end": v(-903.62, 212.18) * mm});
            skLineSegment(sketch, "E1471.MirrorCS", {"start": v(-916.44, 226.77) * mm, "end": v(-912.6, 229) * mm});
            skLineSegment(sketch, "E1472.MirrorCS", {"start": v(-823.57, 199.6) * mm, "end": v(-826.32, 201.18) * mm});
            skLineSegment(sketch, "E1473.MirrorCS", {"start": v(-852.9, 181.19) * mm, "end": v(-852.9, 184.36) * mm});
            skLineSegment(sketch, "E1474.MirrorCS", {"start": v(-907.64, 212.8) * mm, "end": v(-904.89, 214.38) * mm});
            skLineSegment(sketch, "E1475.MirrorCS", {"start": v(-812.35, 225.38) * mm, "end": v(-809.6, 223.79) * mm});
            skLineSegment(sketch, "E1476.MirrorCS", {"start": v(-883.38, 184.36) * mm, "end": v(-883.38, 181.19) * mm});
            skLineSegment(sketch, "E1477.MirrorCS", {"start": v(-815.95, 212.8) * mm, "end": v(-818.7, 214.38) * mm});
            skLineSegment(sketch, "E1478.MirrorCS", {"start": v(-811, 229) * mm, "end": v(-807.14, 226.77) * mm});
            skLineSegment(sketch, "E1479.MirrorCS", {"start": v(-817.22, 210.6) * mm, "end": v(-819.97, 212.18) * mm});
            skLineSegment(sketch, "E1480.MirrorCS", {"start": v(-898.75, 197.4) * mm, "end": v(-896, 198.98) * mm});
            skLineSegment(sketch, "E1481.MirrorCS", {"start": v(-840.2, 184.36) * mm, "end": v(-840.2, 181.19) * mm});
            skLineSegment(sketch, "E1482.MirrorCS", {"start": v(-826.32, 201.18) * mm, "end": v(-823.14, 206.68) * mm});
            skLineSegment(sketch, "E1483.MirrorCS", {"start": v(-820.4, 205.1) * mm, "end": v(-817.22, 210.6) * mm});
            skLineSegment(sketch, "E1484.MirrorCS", {"start": v(-887.2, 180.55) * mm, "end": v(-887.2, 185) * mm});
            skLineSegment(sketch, "E1485.MirrorCS", {"start": v(-823.14, 206.68) * mm, "end": v(-819.97, 212.18) * mm});
            skLineSegment(sketch, "E1486.MirrorCS", {"start": v(-823.57, 199.6) * mm, "end": v(-820.4, 205.1) * mm});
            skLineSegment(sketch, "E1487.MirrorCS", {"start": v(-818.7, 214.38) * mm, "end": v(-812.35, 225.38) * mm});
            skLineSegment(sketch, "E1488.MirrorCS", {"start": v(-836.4, 185) * mm, "end": v(-811, 229) * mm});
            skLineSegment(sketch, "E1489.MirrorCS", {"start": v(-831.19, 186.4) * mm, "end": v(-824.84, 197.4) * mm});
            skPoint(sketch, "E1490.MirrorP", {"position": v(-821.77, 205.89) * mm});
            skLineSegment(sketch, "E1491.MirrorCS", {"start": v(-815.95, 212.8) * mm, "end": v(-809.6, 223.79) * mm});
            skLineSegment(sketch, "E1492.MirrorCS", {"start": v(-833.94, 187.98) * mm, "end": v(-827.59, 198.98) * mm});
            skLineSegment(sketch, "E1493.MirrorCS", {"start": v(-832.54, 182.78) * mm, "end": v(-807.14, 226.77) * mm});
            skPoint(sketch, "E1494.MirrorP", {"position": v(-809.07, 227.88) * mm});
            skLineSegment(sketch, "E1495", {"start": v(-1236.64, 231.22) * mm, "end": v(-1236.64, 226.77) * mm});
            skLineSegment(sketch, "E1496", {"start": v(-1207.39, 277.43) * mm, "end": v(-1211.24, 275.21) * mm});
            skLineSegment(sketch, "E1497", {"start": v(-1127.34, 323.65) * mm, "end": v(-1131.19, 321.43) * mm});
            skLineSegment(sketch, "E1498", {"start": v(-1076.54, 323.65) * mm, "end": v(-1072.69, 321.43) * mm});
            skLineSegment(sketch, "E1499", {"start": v(-971.09, 321.43) * mm, "end": v(-967.24, 323.65) * mm});
            skLineSegment(sketch, "E1500", {"start": v(-916.44, 323.65) * mm, "end": v(-912.6, 321.43) * mm});
            skLineSegment(sketch, "E1501", {"start": v(-836.4, 277.43) * mm, "end": v(-832.54, 275.21) * mm});
            skLineSegment(sketch, "E1502", {"start": v(-807.14, 231.22) * mm, "end": v(-807.14, 226.77) * mm});
            skLineSegment(sketch, "E1503", {"start": v(-807.14, 138.78) * mm, "end": v(-807.14, 134.34) * mm});
            skLineSegment(sketch, "E1504", {"start": v(-807.14, 46.35) * mm, "end": v(-807.14, 41.9) * mm});
            skLineSegment(sketch, "E1505", {"start": v(-832.54, -2.09) * mm, "end": v(-836.4, -4.31) * mm});
            skLineSegment(sketch, "E1506", {"start": v(-887.2, -4.31) * mm, "end": v(-891.04, -2.09) * mm});
            skLineSegment(sketch, "E1507", {"start": v(-992.64, -2.09) * mm, "end": v(-996.49, -4.31) * mm});
            skLineSegment(sketch, "E1508", {"start": v(-1047.29, -4.31) * mm, "end": v(-1051.14, -2.09) * mm});
            skLineSegment(sketch, "E1509", {"start": v(-1152.74, -2.09) * mm, "end": v(-1156.59, -4.31) * mm});
            skLineSegment(sketch, "E1510", {"start": v(-1207.39, -4.31) * mm, "end": v(-1211.24, -2.09) * mm});
            skLineSegment(sketch, "E1511", {"start": v(-1236.64, 41.9) * mm, "end": v(-1236.64, 46.35) * mm});
            skLineSegment(sketch, "E1512", {"start": v(-1236.64, 134.34) * mm, "end": v(-1236.64, 138.78) * mm});
            skSolve(sketch);
        }
        {
            var Q0;
            Q0=makeQuery(id+"F0.imprint","IMPRINT",FACE,{"disambiguationData":[TD([[makeQuery(id+"F0.imprint","IMPRINT",EDGE,{"derivedFrom":sQuery(id+"F0.wireOp",EDGE,"E244")}),1.0]])]});
            var Q1;
            Q1=makeQuery(id+"F0.imprint","IMPRINT",FACE,{"disambiguationData":[TD([[makeQuery(id+"F0.imprint","IMPRINT",EDGE,{"derivedFrom":sQuery(id+"F0.wireOp",EDGE,"E237")}),1.0]])]});
            var Q2;
            Q2=makeQuery(id+"F0.imprint","IMPRINT",FACE,{"disambiguationData":[TD([[makeQuery(id+"F0.imprint","IMPRINT",EDGE,{"derivedFrom":sQuery(id+"F0.wireOp",EDGE,"E297.MirrorCS")}),1.0]])]});
            var Q3;
            Q3=makeQuery(id+"F0.imprint","IMPRINT",FACE,{"disambiguationData":[TD([[makeQuery(id+"F0.imprint","IMPRINT",EDGE,{"derivedFrom":sQuery(id+"F0.wireOp",EDGE,"E237")}),-1.0]])]});
            var Q4;
            Q4=makeQuery(id+"F0.imprint","IMPRINT",FACE,{"disambiguationData":[TD([[makeQuery(id+"F0.imprint","IMPRINT",EDGE,{"derivedFrom":sQuery(id+"F0.wireOp",EDGE,"E536")}),-1.0]])]});
            var Q5;
            Q5=makeQuery(id+"F0.imprint","IMPRINT",FACE,{"disambiguationData":[TD([[makeQuery(id+"F0.imprint","IMPRINT",EDGE,{"derivedFrom":sQuery(id+"F0.wireOp",EDGE,"E296")}),1.0]])]});
            var Q6;
            Q6=makeQuery(id+"F0.imprint","IMPRINT",FACE,{"disambiguationData":[TD([[makeQuery(id+"F0.imprint","IMPRINT",EDGE,{"derivedFrom":sQuery(id+"F0.wireOp",EDGE,"E543")}),1.0]])]});
            var Q7;
            Q7=makeQuery(id+"F0.imprint","IMPRINT",FACE,{"disambiguationData":[TD([[makeQuery(id+"F0.imprint","IMPRINT",EDGE,{"derivedFrom":sQuery(id+"F0.wireOp",EDGE,"E456")}),1.0]])]});
            var Q8;
            Q8=makeQuery(id+"F0.imprint","IMPRINT",FACE,{"disambiguationData":[TD([[makeQuery(id+"F0.imprint","IMPRINT",EDGE,{"derivedFrom":sQuery(id+"F0.wireOp",EDGE,"E603.MirrorCS")}),-1.0]])]});
            var Q9;
            Q9=makeQuery(id+"F0.imprint","IMPRINT",FACE,{"disambiguationData":[TD([[makeQuery(id+"F0.imprint","IMPRINT",EDGE,{"derivedFrom":sQuery(id+"F0.wireOp",EDGE,"E343.MirrorCS")}),-1.0]])]});
            var Q10;
            Q10=makeQuery(id+"F0.imprint","IMPRINT",FACE,{"disambiguationData":[TD([[makeQuery(id+"F0.imprint","IMPRINT",EDGE,{"derivedFrom":sQuery(id+"F0.wireOp",EDGE,"E165")}),-1.0]])]});
            var Q11;
            Q11=makeQuery(id+"F0.imprint","IMPRINT",FACE,{"disambiguationData":[TD([[makeQuery(id+"F0.imprint","IMPRINT",EDGE,{"derivedFrom":sQuery(id+"F0.wireOp",EDGE,"E132")}),1.0]])]});
            var Q12;
            Q12=makeQuery(id+"F0.imprint","IMPRINT",FACE,{"disambiguationData":[TD([[makeQuery(id+"F0.imprint","IMPRINT",EDGE,{"derivedFrom":sQuery(id+"F0.wireOp",EDGE,"E305.MirrorCS")}),-1.0]])]});
            var Q13;
            Q13=makeQuery(id+"F0.imprint","IMPRINT",FACE,{"disambiguationData":[TD([[makeQuery(id+"F0.imprint","IMPRINT",EDGE,{"derivedFrom":sQuery(id+"F0.wireOp",EDGE,"E184")}),1.0]])]});
            var Q14;
            Q14=makeQuery(id+"F0.imprint","IMPRINT",FACE,{"disambiguationData":[TD([[makeQuery(id+"F0.imprint","IMPRINT",EDGE,{"derivedFrom":sQuery(id+"F0.wireOp",EDGE,"E356")}),1.0]])]});
            var Q15;
            Q15=makeQuery(id+"F0.imprint","IMPRINT",FACE,{"disambiguationData":[TD([[makeQuery(id+"F0.imprint","IMPRINT",EDGE,{"derivedFrom":sQuery(id+"F0.wireOp",EDGE,"E231.MirrorCS")}),-1.0]])]});
            var Q16;
            Q16=makeQuery(id+"F0.imprint","IMPRINT",FACE,{"disambiguationData":[TD([[makeQuery(id+"F0.imprint","IMPRINT",EDGE,{"derivedFrom":sQuery(id+"F0.wireOp",EDGE,"E504.MirrorCS")}),-1.0]])]});
            var Q17;
            Q17=makeQuery(id+"F0.imprint","IMPRINT",FACE,{"disambiguationData":[TD([[makeQuery(id+"F0.imprint","IMPRINT",EDGE,{"derivedFrom":sQuery(id+"F0.wireOp",EDGE,"E185.MirrorCS")}),1.0]])]});
            var Q18;
            Q18=makeQuery(id+"F0.imprint","IMPRINT",FACE,{"disambiguationData":[TD([[makeQuery(id+"F0.imprint","IMPRINT",EDGE,{"derivedFrom":sQuery(id+"F0.wireOp",EDGE,"E40")}),-1.0]])]});
            var Q19;
            Q19=makeQuery(id+"F0.imprint","IMPRINT",FACE,{"disambiguationData":[TD([[makeQuery(id+"F0.imprint","IMPRINT",EDGE,{"derivedFrom":sQuery(id+"F0.wireOp",EDGE,"E193.MirrorCS")}),-1.0]])]});
            var Q20;
            Q20=makeQuery(id+"F0.imprint","IMPRINT",FACE,{"disambiguationData":[TD([[makeQuery(id+"F0.imprint","IMPRINT",EDGE,{"derivedFrom":sQuery(id+"F0.wireOp",EDGE,"E7")}),1.0]])]});
            var Q21;
            Q21=makeQuery(id+"F0.imprint","IMPRINT",FACE,{"disambiguationData":[TD([[makeQuery(id+"F0.imprint","IMPRINT",EDGE,{"derivedFrom":sQuery(id+"F0.wireOp",EDGE,"E60.MirrorCS")}),1.0]])]});
            var Q22;
            Q22=makeQuery(id+"F0.imprint","IMPRINT",FACE,{"disambiguationData":[TD([[makeQuery(id+"F0.imprint","IMPRINT",EDGE,{"derivedFrom":sQuery(id+"F0.wireOp",EDGE,"E59")}),1.0]])]});
            var Q23;
            Q23=makeQuery(id+"F0.imprint","IMPRINT",FACE,{"disambiguationData":[TD([[makeQuery(id+"F0.imprint","IMPRINT",EDGE,{"derivedFrom":sQuery(id+"F0.wireOp",EDGE,"E65.MirrorCS")}),-1.0]])]});
            var Q24;
            Q24=makeQuery(id+"F0.imprint","IMPRINT",FACE,{"disambiguationData":[TD([[makeQuery(id+"F0.imprint","IMPRINT",EDGE,{"derivedFrom":sQuery(id+"F0.wireOp",EDGE,"E404.MirrorCS")}),-1.0]])]});
            var Q25;
            Q25=makeQuery(id+"F0.imprint","IMPRINT",FACE,{"disambiguationData":[TD([[makeQuery(id+"F0.imprint","IMPRINT",EDGE,{"derivedFrom":sQuery(id+"F0.wireOp",EDGE,"E68.MirrorCS")}),-1.0]])]});
            var Q26;
            Q26=makeQuery(id+"F0.imprint","IMPRINT",FACE,{"disambiguationData":[TD([[makeQuery(id+"F0.imprint","IMPRINT",EDGE,{"derivedFrom":sQuery(id+"F0.wireOp",EDGE,"E642")}),1.0]])]});
            var Q27;
            Q27=makeQuery(id+"F0.imprint","IMPRINT",FACE,{"disambiguationData":[TD([[makeQuery(id+"F0.imprint","IMPRINT",EDGE,{"derivedFrom":sQuery(id+"F0.wireOp",EDGE,"E803.MirrorCS")}),-1.0]])]});
            var Q28;
            Q28=makeQuery(id+"F0.imprint","IMPRINT",FACE,{"disambiguationData":[TD([[makeQuery(id+"F0.imprint","IMPRINT",EDGE,{"derivedFrom":sQuery(id+"F0.wireOp",EDGE,"E446.MirrorCS")}),-1.0]])]});
            var Q29;
            Q29=makeQuery(id+"F0.imprint","IMPRINT",FACE,{"disambiguationData":[TD([[makeQuery(id+"F0.imprint","IMPRINT",EDGE,{"derivedFrom":sQuery(id+"F0.wireOp",EDGE,"E683.MirrorCS")}),1.0]])]});
            var Q30;
            Q30=makeQuery(id+"F0.imprint","IMPRINT",FACE,{"disambiguationData":[TD([[makeQuery(id+"F0.imprint","IMPRINT",EDGE,{"derivedFrom":sQuery(id+"F0.wireOp",EDGE,"E688.MirrorCS")}),-1.0]])]});
            var Q31;
            Q31=makeQuery(id+"F0.imprint","IMPRINT",FACE,{"disambiguationData":[TD([[makeQuery(id+"F0.imprint","IMPRINT",EDGE,{"derivedFrom":sQuery(id+"F0.wireOp",EDGE,"E691.MirrorCS")}),-1.0]])]});
            var Q32;
            Q32=makeQuery(id+"F0.imprint","IMPRINT",FACE,{"disambiguationData":[TD([[makeQuery(id+"F0.imprint","IMPRINT",EDGE,{"derivedFrom":sQuery(id+"F0.wireOp",EDGE,"E977.MirrorCS")}),-1.0]])]});
            var Q33;
            Q33=makeQuery(id+"F0.imprint","IMPRINT",FACE,{"disambiguationData":[TD([[makeQuery(id+"F0.imprint","IMPRINT",EDGE,{"derivedFrom":sQuery(id+"F0.wireOp",EDGE,"E682")}),1.0]])]});
            var Q34;
            Q34=makeQuery(id+"F0.imprint","IMPRINT",FACE,{"disambiguationData":[TD([[makeQuery(id+"F0.imprint","IMPRINT",EDGE,{"derivedFrom":sQuery(id+"F0.wireOp",EDGE,"E833.MirrorCS")}),-1.0]])]});
            var Q35;
            Q35=makeQuery(id+"F0.imprint","IMPRINT",FACE,{"disambiguationData":[TD([[makeQuery(id+"F0.imprint","IMPRINT",EDGE,{"derivedFrom":sQuery(id+"F0.wireOp",EDGE,"E534.MirrorCS")}),-1.0]])]});
            var Q36;
            Q36=makeQuery(id+"F0.imprint","IMPRINT",FACE,{"disambiguationData":[TD([[makeQuery(id+"F0.imprint","IMPRINT",EDGE,{"derivedFrom":sQuery(id+"F0.wireOp",EDGE,"E929")}),1.0]])]});
            var Q37;
            Q37=makeQuery(id+"F0.imprint","IMPRINT",FACE,{"disambiguationData":[TD([[makeQuery(id+"F0.imprint","IMPRINT",EDGE,{"derivedFrom":sQuery(id+"F0.wireOp",EDGE,"E396")}),1.0]])]});
            var Q38;
            Q38=makeQuery(id+"F0.imprint","IMPRINT",FACE,{"disambiguationData":[TD([[makeQuery(id+"F0.imprint","IMPRINT",EDGE,{"derivedFrom":sQuery(id+"F0.wireOp",EDGE,"E1264.MirrorCS")}),-1.0]])]});
            var Q39;
            Q39=makeQuery(id+"F0.imprint","IMPRINT",FACE,{"disambiguationData":[TD([[makeQuery(id+"F0.imprint","IMPRINT",EDGE,{"derivedFrom":sQuery(id+"F0.wireOp",EDGE,"E1261.MirrorCS")}),-1.0]])]});
            var Q40;
            Q40=makeQuery(id+"F0.imprint","IMPRINT",FACE,{"disambiguationData":[TD([[makeQuery(id+"F0.imprint","IMPRINT",EDGE,{"derivedFrom":sQuery(id+"F0.wireOp",EDGE,"E1256.MirrorCS")}),1.0]])]});
            var Q41;
            Q41=makeQuery(id+"F0.imprint","IMPRINT",FACE,{"disambiguationData":[TD([[makeQuery(id+"F0.imprint","IMPRINT",EDGE,{"derivedFrom":sQuery(id+"F0.wireOp",EDGE,"E1230")}),-1.0]])]});
            var Q42;
            Q42=makeQuery(id+"F0.imprint","IMPRINT",FACE,{"disambiguationData":[TD([[makeQuery(id+"F0.imprint","IMPRINT",EDGE,{"derivedFrom":sQuery(id+"F0.wireOp",EDGE,"E1215")}),1.0]])]});
            var Q43;
            Q43=makeQuery(id+"F0.imprint","IMPRINT",FACE,{"disambiguationData":[TD([[makeQuery(id+"F0.imprint","IMPRINT",EDGE,{"derivedFrom":sQuery(id+"F0.wireOp",EDGE,"E1376.MirrorCS")}),-1.0]])]});
            var Q44;
            Q44=makeQuery(id+"F0.imprint","IMPRINT",FACE,{"disambiguationData":[TD([[makeQuery(id+"F0.imprint","IMPRINT",EDGE,{"derivedFrom":sQuery(id+"F0.wireOp",EDGE,"E1230")}),1.0]])]});
            var Q45;
            Q45=makeQuery(id+"F0.imprint","IMPRINT",FACE,{"disambiguationData":[TD([[makeQuery(id+"F0.imprint","IMPRINT",EDGE,{"derivedFrom":sQuery(id+"F0.wireOp",EDGE,"E1343")}),-1.0]])]});
            var Q46;
            Q46=makeQuery(id+"F0.imprint","IMPRINT",FACE,{"disambiguationData":[TD([[makeQuery(id+"F0.imprint","IMPRINT",EDGE,{"derivedFrom":sQuery(id+"F0.wireOp",EDGE,"E1408")}),-1.0]])]});
            var Q47;
            Q47=makeQuery(id+"F0.imprint","IMPRINT",FACE,{"disambiguationData":[TD([[makeQuery(id+"F0.imprint","IMPRINT",EDGE,{"derivedFrom":sQuery(id+"F0.wireOp",EDGE,"E920.MirrorCS")}),-1.0]])]});
            var Q48;
            Q48=makeQuery(id+"F0.imprint","IMPRINT",FACE,{"disambiguationData":[TD([[makeQuery(id+"F0.imprint","IMPRINT",EDGE,{"derivedFrom":sQuery(id+"F0.wireOp",EDGE,"E1109")}),-1.0]])]});
            var Q49;
            Q49=makeQuery(id+"F0.imprint","IMPRINT",FACE,{"disambiguationData":[TD([[makeQuery(id+"F0.imprint","IMPRINT",EDGE,{"derivedFrom":sQuery(id+"F0.wireOp",EDGE,"E835")}),-1.0]])]});
            var Q50;
            Q50=makeQuery(id+"F0.imprint","IMPRINT",FACE,{"disambiguationData":[TD([[makeQuery(id+"F0.imprint","IMPRINT",EDGE,{"derivedFrom":sQuery(id+"F0.wireOp",EDGE,"E1069")}),1.0]])]});
            var Q51;
            Q51=makeQuery(id+"F0.imprint","IMPRINT",FACE,{"disambiguationData":[TD([[makeQuery(id+"F0.imprint","IMPRINT",EDGE,{"derivedFrom":sQuery(id+"F0.wireOp",EDGE,"E1463.MirrorCS")}),-1.0]])]});
            var Q52;
            Q52=makeQuery(id+"F0.imprint","IMPRINT",FACE,{"disambiguationData":[TD([[makeQuery(id+"F0.imprint","IMPRINT",EDGE,{"derivedFrom":sQuery(id+"F0.wireOp",EDGE,"E1328")}),1.0]])]});
            var Q53;
            Q53=makeQuery(id+"F0.imprint","IMPRINT",FACE,{"disambiguationData":[TD([[makeQuery(id+"F0.imprint","IMPRINT",EDGE,{"derivedFrom":sQuery(id+"F0.wireOp",EDGE,"E1343")}),1.0]])]});
            var Q54;
            Q54=makeQuery(id+"F0.imprint","IMPRINT",FACE,{"disambiguationData":[TD([[makeQuery(id+"F0.imprint","IMPRINT",EDGE,{"derivedFrom":sQuery(id+"F0.wireOp",EDGE,"E1460.MirrorCS")}),-1.0]])]});
            var Q55;
            Q55=makeQuery(id+"F0.imprint","IMPRINT",FACE,{"disambiguationData":[TD([[makeQuery(id+"F0.imprint","IMPRINT",EDGE,{"derivedFrom":sQuery(id+"F0.wireOp",EDGE,"E1373.MirrorCS")}),-1.0]])]});
            var Q56;
            Q56=makeQuery(id+"F0.imprint","IMPRINT",FACE,{"disambiguationData":[TD([[makeQuery(id+"F0.imprint","IMPRINT",EDGE,{"derivedFrom":sQuery(id+"F0.wireOp",EDGE,"E1430")}),1.0]])]});
            var Q57;
            Q57=makeQuery(id+"F0.imprint","IMPRINT",FACE,{"disambiguationData":[TD([[makeQuery(id+"F0.imprint","IMPRINT",EDGE,{"derivedFrom":sQuery(id+"F0.wireOp",EDGE,"E1415")}),1.0]])]});
            var Q58;
            Q58=makeQuery(id+"F0.imprint","IMPRINT",FACE,{"disambiguationData":[TD([[makeQuery(id+"F0.imprint","IMPRINT",EDGE,{"derivedFrom":sQuery(id+"F0.wireOp",EDGE,"E969")}),1.0]])]});
            var Q59;
            Q59=makeQuery(id+"F0.imprint","IMPRINT",FACE,{"disambiguationData":[TD([[makeQuery(id+"F0.imprint","IMPRINT",EDGE,{"derivedFrom":sQuery(id+"F0.wireOp",EDGE,"E1077.MirrorCS")}),-1.0]])]});
            var Q60;
            Q60=makeQuery(id+"F0.imprint","IMPRINT",FACE,{"disambiguationData":[TD([[makeQuery(id+"F0.imprint","IMPRINT",EDGE,{"derivedFrom":sQuery(id+"F0.wireOp",EDGE,"E795")}),1.0]])]});
            var Q61;
            Q61=makeQuery(id+"F0.imprint","IMPRINT",FACE,{"disambiguationData":[TD([[makeQuery(id+"F0.imprint","IMPRINT",EDGE,{"derivedFrom":sQuery(id+"F0.wireOp",EDGE,"E1029")}),1.0]])]});
            var Q62;
            Q62=makeQuery(id+"F0.imprint","IMPRINT",FACE,{"disambiguationData":[TD([[makeQuery(id+"F0.imprint","IMPRINT",EDGE,{"derivedFrom":sQuery(id+"F0.wireOp",EDGE,"E1131")}),1.0]])]});
            var Q63;
            Q63=makeQuery(id+"F0.imprint","IMPRINT",FACE,{"disambiguationData":[TD([[makeQuery(id+"F0.imprint","IMPRINT",EDGE,{"derivedFrom":sQuery(id+"F0.wireOp",EDGE,"E1408")}),1.0]])]});
            var Q64;
            Q64=makeQuery(id+"F0.imprint","IMPRINT",FACE,{"disambiguationData":[TD([[makeQuery(id+"F0.imprint","IMPRINT",EDGE,{"derivedFrom":sQuery(id+"F0.wireOp",EDGE,"E1176.MirrorCS")}),-1.0]])]});
            var Q65;
            Q65=makeQuery(id+"F0.imprint","IMPRINT",FACE,{"disambiguationData":[TD([[makeQuery(id+"F0.imprint","IMPRINT",EDGE,{"derivedFrom":sQuery(id+"F0.wireOp",EDGE,"E882")}),1.0]])]});
            var Q66;
            Q66=makeQuery(id+"F0.imprint","IMPRINT",FACE,{"disambiguationData":[TD([[makeQuery(id+"F0.imprint","IMPRINT",EDGE,{"derivedFrom":sQuery(id+"F0.wireOp",EDGE,"E1116")}),1.0]])]});
            var Q67;
            Q67=makeQuery(id+"F0.imprint","IMPRINT",FACE,{"disambiguationData":[TD([[makeQuery(id+"F0.imprint","IMPRINT",EDGE,{"derivedFrom":sQuery(id+"F0.wireOp",EDGE,"E1109")}),1.0]])]});
            var Q68;
            Q68=makeQuery(id+"F0.imprint","IMPRINT",FACE,{"disambiguationData":[TD([[makeQuery(id+"F0.imprint","IMPRINT",EDGE,{"derivedFrom":sQuery(id+"F0.wireOp",EDGE,"E835")}),1.0]])]});
            var Q69;
            Q69=makeQuery(id+"F0.imprint","IMPRINT",FACE,{"disambiguationData":[TD([[makeQuery(id+"F0.imprint","IMPRINT",EDGE,{"derivedFrom":sQuery(id+"F0.wireOp",EDGE,"E842")}),1.0]])]});
            var Q70;
            Q70=makeQuery(id+"F0.imprint","IMPRINT",FACE,{"disambiguationData":[TD([[makeQuery(id+"F0.imprint","IMPRINT",EDGE,{"derivedFrom":sQuery(id+"F0.wireOp",EDGE,"E496")}),1.0]])]});
            var Q71;
            Q71=makeQuery(id+"F0.imprint","IMPRINT",FACE,{"disambiguationData":[TD([[makeQuery(id+"F0.imprint","IMPRINT",EDGE,{"derivedFrom":sQuery(id+"F0.wireOp",EDGE,"E558")}),1.0]])]});
            var Q72;
            Q72=makeQuery(id+"F0.imprint","IMPRINT",FACE,{"disambiguationData":[TD([[makeQuery(id+"F0.imprint","IMPRINT",EDGE,{"derivedFrom":sQuery(id+"F0.wireOp",EDGE,"E536")}),1.0]])]});
            var Q73;
            Q73=makeQuery(id+"F0.imprint","IMPRINT",FACE,{"disambiguationData":[TD([[makeQuery(id+"F0.imprint","IMPRINT",EDGE,{"derivedFrom":sQuery(id+"F0.wireOp",EDGE,"E890.MirrorCS")}),-1.0]])]});
            var Q74;
            Q74=makeQuery(id+"F0.imprint","IMPRINT",FACE,{"disambiguationData":[TD([[makeQuery(id+"F0.imprint","IMPRINT",EDGE,{"derivedFrom":sQuery(id+"F0.wireOp",EDGE,"E755")}),1.0]])]});
            var Q75;
            Q75=makeQuery(id+"F0.imprint","IMPRINT",FACE,{"disambiguationData":[TD([[makeQuery(id+"F0.imprint","IMPRINT",EDGE,{"derivedFrom":sQuery(id+"F0.wireOp",EDGE,"E166")}),1.0]])]});
            var Q76;
            Q76=makeQuery(id+"F0.imprint","IMPRINT",FACE,{"disambiguationData":[TD([[makeQuery(id+"F0.imprint","IMPRINT",EDGE,{"derivedFrom":sQuery(id+"F0.wireOp",EDGE,"E306.MirrorCS")}),-1.0]])]});
            var Q77;
            Q77=makeQuery(id+"F0.imprint","IMPRINT",FACE,{"disambiguationData":[TD([[makeQuery(id+"F0.imprint","IMPRINT",EDGE,{"derivedFrom":sQuery(id+"F0.wireOp",EDGE,"E239")}),1.0]])]});
            var Q78;
            Q78=makeQuery(id+"F0.imprint","IMPRINT",FACE,{"disambiguationData":[TD([[makeQuery(id+"F0.imprint","IMPRINT",EDGE,{"derivedFrom":sQuery(id+"F0.wireOp",EDGE,"E320.MirrorCS")}),1.0]])]});
            var Q79;
            Q79=makeQuery(id+"F0.imprint","IMPRINT",FACE,{"disambiguationData":[TD([[makeQuery(id+"F0.imprint","IMPRINT",EDGE,{"derivedFrom":sQuery(id+"F0.wireOp",EDGE,"E604.MirrorCS")}),-1.0]])]});
            var Q80;
            Q80=makeQuery(id+"F0.imprint","IMPRINT",FACE,{"disambiguationData":[TD([[makeQuery(id+"F0.imprint","IMPRINT",EDGE,{"derivedFrom":sQuery(id+"F0.wireOp",EDGE,"E595")}),-1.0]])]});
            var Q81;
            Q81=makeQuery(id+"F0.imprint","IMPRINT",FACE,{"disambiguationData":[TD([[makeQuery(id+"F0.imprint","IMPRINT",EDGE,{"derivedFrom":sQuery(id+"F0.wireOp",EDGE,"E837")}),1.0]])]});
            var Q82;
            Q82=makeQuery(id+"F0.imprint","IMPRINT",FACE,{"disambiguationData":[TD([[makeQuery(id+"F0.imprint","IMPRINT",EDGE,{"derivedFrom":sQuery(id+"F0.wireOp",EDGE,"E905.MirrorCS")}),1.0]])]});
            var Q83;
            Q83=makeQuery(id+"F0.imprint","IMPRINT",FACE,{"disambiguationData":[TD([[makeQuery(id+"F0.imprint","IMPRINT",EDGE,{"derivedFrom":sQuery(id+"F0.wireOp",EDGE,"E519.MirrorCS")}),1.0]])]});
            var Q84;
            Q84=makeQuery(id+"F0.imprint","IMPRINT",FACE,{"disambiguationData":[TD([[makeQuery(id+"F0.imprint","IMPRINT",EDGE,{"derivedFrom":sQuery(id+"F0.wireOp",EDGE,"E891.MirrorCS")}),-1.0]])]});
            var Q85;
            Q85=makeQuery(id+"F0.imprint","IMPRINT",FACE,{"disambiguationData":[TD([[makeQuery(id+"F0.imprint","IMPRINT",EDGE,{"derivedFrom":sQuery(id+"F0.wireOp",EDGE,"E1168")}),-1.0]])]});
            var Q86;
            Q86=makeQuery(id+"F0.imprint","IMPRINT",FACE,{"disambiguationData":[TD([[makeQuery(id+"F0.imprint","IMPRINT",EDGE,{"derivedFrom":sQuery(id+"F0.wireOp",EDGE,"E1177.MirrorCS")}),-1.0]])]});
            var Q87;
            Q87=makeQuery(id+"F0.imprint","IMPRINT",FACE,{"disambiguationData":[TD([[makeQuery(id+"F0.imprint","IMPRINT",EDGE,{"derivedFrom":sQuery(id+"F0.wireOp",EDGE,"E1092.MirrorCS")}),1.0]])]});
            var Q88;
            Q88=makeQuery(id+"F0.imprint","IMPRINT",FACE,{"disambiguationData":[TD([[makeQuery(id+"F0.imprint","IMPRINT",EDGE,{"derivedFrom":sQuery(id+"F0.wireOp",EDGE,"E1344")}),-1.0]])]});
            var Q89;
            Q89=makeQuery(id+"F0.imprint","IMPRINT",FACE,{"disambiguationData":[TD([[makeQuery(id+"F0.imprint","IMPRINT",EDGE,{"derivedFrom":sQuery(id+"F0.wireOp",EDGE,"E1231")}),-1.0]])]});
            var Q90;
            Q90=makeQuery(id+"F0.imprint","IMPRINT",FACE,{"disambiguationData":[TD([[makeQuery(id+"F0.imprint","IMPRINT",EDGE,{"derivedFrom":sQuery(id+"F0.wireOp",EDGE,"E992.MirrorCS")}),1.0]])]});
            var Q91;
            Q91=makeQuery(id+"F0.imprint","IMPRINT",FACE,{"disambiguationData":[TD([[makeQuery(id+"F0.imprint","IMPRINT",EDGE,{"derivedFrom":sQuery(id+"F0.wireOp",EDGE,"E1078.MirrorCS")}),-1.0]])]});
            var Q92;
            Q92=makeQuery(id+"F0.imprint","IMPRINT",FACE,{"disambiguationData":[TD([[makeQuery(id+"F0.imprint","IMPRINT",EDGE,{"derivedFrom":sQuery(id+"F0.wireOp",EDGE,"E818.MirrorCS")}),1.0]])]});
            var Q93;
            Q93=makeQuery(id+"F0.imprint","IMPRINT",FACE,{"disambiguationData":[TD([[makeQuery(id+"F0.imprint","IMPRINT",EDGE,{"derivedFrom":sQuery(id+"F0.wireOp",EDGE,"E804.MirrorCS")}),-1.0]])]});
            var Q94;
            Q94=makeQuery(id+"F0.imprint","IMPRINT",FACE,{"disambiguationData":[TD([[makeQuery(id+"F0.imprint","IMPRINT",EDGE,{"derivedFrom":sQuery(id+"F0.wireOp",EDGE,"E706.MirrorCS")}),1.0]])]});
            var Q95;
            Q95=makeQuery(id+"F0.imprint","IMPRINT",FACE,{"disambiguationData":[TD([[makeQuery(id+"F0.imprint","IMPRINT",EDGE,{"derivedFrom":sQuery(id+"F0.wireOp",EDGE,"E978.MirrorCS")}),-1.0]])]});
            var Q96;
            Q96=makeQuery(id+"F0.imprint","IMPRINT",FACE,{"disambiguationData":[TD([[makeQuery(id+"F0.imprint","IMPRINT",EDGE,{"derivedFrom":sQuery(id+"F0.wireOp",EDGE,"E405.MirrorCS")}),-1.0]])]});
            var Q97;
            Q97=makeQuery(id+"F0.imprint","IMPRINT",FACE,{"disambiguationData":[TD([[makeQuery(id+"F0.imprint","IMPRINT",EDGE,{"derivedFrom":sQuery(id+"F0.wireOp",EDGE,"E419.MirrorCS")}),1.0]])]});
            var Q98;
            Q98=makeQuery(id+"F0.imprint","IMPRINT",FACE,{"disambiguationData":[TD([[makeQuery(id+"F0.imprint","IMPRINT",EDGE,{"derivedFrom":sQuery(id+"F0.wireOp",EDGE,"E505.MirrorCS")}),-1.0]])]});
            var Q99;
            Q99=makeQuery(id+"F0.imprint","IMPRINT",FACE,{"disambiguationData":[TD([[makeQuery(id+"F0.imprint","IMPRINT",EDGE,{"derivedFrom":sQuery(id+"F0.wireOp",EDGE,"E194.MirrorCS")}),-1.0]])]});
            var Q100;
            Q100=makeQuery(id+"F0.imprint","IMPRINT",FACE,{"disambiguationData":[TD([[makeQuery(id+"F0.imprint","IMPRINT",EDGE,{"derivedFrom":sQuery(id+"F0.wireOp",EDGE,"E83.MirrorCS")}),1.0]])]});
            var Q101;
            Q101=makeQuery(id+"F0.imprint","IMPRINT",FACE,{"disambiguationData":[TD([[makeQuery(id+"F0.imprint","IMPRINT",EDGE,{"derivedFrom":sQuery(id+"F0.wireOp",EDGE,"E208.MirrorCS")}),1.0]])]});
            var Q102;
            Q102=makeQuery(id+"F0.imprint","IMPRINT",FACE,{"disambiguationData":[TD([[makeQuery(id+"F0.imprint","IMPRINT",EDGE,{"derivedFrom":sQuery(id+"F0.wireOp",EDGE,"E41")}),1.0]])]});
            var Q103;
            Q103=makeQuery(id+"F0.imprint","IMPRINT",FACE,{"disambiguationData":[TD([[makeQuery(id+"F0.imprint","IMPRINT",EDGE,{"derivedFrom":sQuery(id+"F0.wireOp",EDGE,"E244")}),-1.0]])]});
            var Q104;
            Q104=makeQuery(id+"F0.imprint","IMPRINT",FACE,{"disambiguationData":[TD([[makeQuery(id+"F0.imprint","IMPRINT",EDGE,{"derivedFrom":sQuery(id+"F0.wireOp",EDGE,"E238")}),-1.0]])]});
            var Q105;
            Q105=makeQuery(id+"F0.imprint","IMPRINT",FACE,{"disambiguationData":[TD([[makeQuery(id+"F0.imprint","IMPRINT",EDGE,{"derivedFrom":sQuery(id+"F0.wireOp",EDGE,"E537")}),-1.0]])]});
            var Q106;
            Q106=makeQuery(id+"F0.imprint","IMPRINT",FACE,{"disambiguationData":[TD([[makeQuery(id+"F0.imprint","IMPRINT",EDGE,{"derivedFrom":sQuery(id+"F0.wireOp",EDGE,"E538")}),1.0]])]});
            var Q107;
            Q107=makeQuery(id+"F0.imprint","IMPRINT",FACE,{"disambiguationData":[TD([[makeQuery(id+"F0.imprint","IMPRINT",EDGE,{"derivedFrom":sQuery(id+"F0.wireOp",EDGE,"E1110")}),-1.0]])]});
            var Q108;
            Q108=makeQuery(id+"F0.imprint","IMPRINT",FACE,{"disambiguationData":[TD([[makeQuery(id+"F0.imprint","IMPRINT",EDGE,{"derivedFrom":sQuery(id+"F0.wireOp",EDGE,"E1111")}),1.0]])]});
            var Q109;
            Q109=makeQuery(id+"F0.imprint","IMPRINT",FACE,{"disambiguationData":[TD([[makeQuery(id+"F0.imprint","IMPRINT",EDGE,{"derivedFrom":sQuery(id+"F0.wireOp",EDGE,"E1410")}),1.0]])]});
            var Q110;
            Q110=makeQuery(id+"F0.imprint","IMPRINT",FACE,{"disambiguationData":[TD([[makeQuery(id+"F0.imprint","IMPRINT",EDGE,{"derivedFrom":sQuery(id+"F0.wireOp",EDGE,"E1455")}),-1.0]])]});
            var Q111;
            Q111=makeQuery(id+"F0.imprint","IMPRINT",FACE,{"disambiguationData":[TD([[makeQuery(id+"F0.imprint","IMPRINT",EDGE,{"derivedFrom":sQuery(id+"F0.wireOp",EDGE,"E1368")}),-1.0]])]});
            var Q112;
            Q112=makeQuery(id+"F0.imprint","IMPRINT",FACE,{"disambiguationData":[TD([[makeQuery(id+"F0.imprint","IMPRINT",EDGE,{"derivedFrom":sQuery(id+"F0.wireOp",EDGE,"E1255")}),-1.0]])]});
            var Q113;
            Q113=makeQuery(id+"F0.imprint","IMPRINT",FACE,{"disambiguationData":[TD([[makeQuery(id+"F0.imprint","IMPRINT",EDGE,{"derivedFrom":sQuery(id+"F0.wireOp",EDGE,"E1261.MirrorCS")}),1.0]])]});
            var Q114;
            Q114=makeQuery(id+"F0.imprint","IMPRINT",FACE,{"disambiguationData":[TD([[makeQuery(id+"F0.imprint","IMPRINT",EDGE,{"derivedFrom":sQuery(id+"F0.wireOp",EDGE,"E1256.MirrorCS")}),-1.0]])]});
            var Q115;
            Q115=makeQuery(id+"F0.imprint","IMPRINT",FACE,{"disambiguationData":[TD([[makeQuery(id+"F0.imprint","IMPRINT",EDGE,{"derivedFrom":sQuery(id+"F0.wireOp",EDGE,"E688.MirrorCS")}),1.0]])]});
            var Q116;
            Q116=makeQuery(id+"F0.imprint","IMPRINT",FACE,{"disambiguationData":[TD([[makeQuery(id+"F0.imprint","IMPRINT",EDGE,{"derivedFrom":sQuery(id+"F0.wireOp",EDGE,"E683.MirrorCS")}),-1.0]])]});
            var Q117;
            Q117=makeQuery(id+"F0.imprint","IMPRINT",FACE,{"disambiguationData":[TD([[makeQuery(id+"F0.imprint","IMPRINT",EDGE,{"derivedFrom":sQuery(id+"F0.wireOp",EDGE,"E65.MirrorCS")}),1.0]])]});
            var Q118;
            Q118=makeQuery(id+"F0.imprint","IMPRINT",FACE,{"disambiguationData":[TD([[makeQuery(id+"F0.imprint","IMPRINT",EDGE,{"derivedFrom":sQuery(id+"F0.wireOp",EDGE,"E60.MirrorCS")}),-1.0]])]});
            var Q119;
            Q119=makeQuery(id+"F0.imprint","IMPRINT",FACE,{"disambiguationData":[TD([[makeQuery(id+"F0.imprint","IMPRINT",EDGE,{"derivedFrom":sQuery(id+"F0.wireOp",EDGE,"E7")}),-1.0]])]});
            var Q120;
            Q120=makeQuery(id+"F0.imprint","IMPRINT",FACE,{"disambiguationData":[TD([[makeQuery(id+"F0.imprint","IMPRINT",EDGE,{"derivedFrom":sQuery(id+"F0.wireOp",EDGE,"E132")}),-1.0]])]});
            extrude(context, id + "F1", {"entities" : qUnion([Q0, Q1, Q2, Q3, Q4, Q5, Q6, Q7, Q8, Q9, Q10, Q11, Q12, Q13, Q14, Q15, Q16, Q17, Q18, Q19, Q20, Q21, Q22, Q23, Q24, Q25, Q26, Q27, Q28, Q29, Q30, Q31, Q32, Q33, Q34, Q35, Q36, Q37, Q38, Q39, Q40, Q41, Q42, Q43, Q44, Q45, Q46, Q47, Q48, Q49, Q50, Q51, Q52, Q53, Q54, Q55, Q56, Q57, Q58, Q59, Q60, Q61, Q62, Q63, Q64, Q65, Q66, Q67, Q68, Q69, Q70, Q71, Q72, Q73, Q74, Q75, Q76, Q77, Q78, Q79, Q80, Q81, Q82, Q83, Q84, Q85, Q86, Q87, Q88, Q89, Q90, Q91, Q92, Q93, Q94, Q95, Q96, Q97, Q98, Q99, Q100, Q101, Q102, Q103, Q104, Q105, Q106, Q107, Q108, Q109, Q110, Q111, Q112, Q113, Q114, Q115, Q116, Q117, Q118, Q119, Q120]), "depth" : 3.17 * mm, "offsetDistance" : 25.4 * mm});
        }
    });
